FCSTD DOCUMENT  (FreeCAD 0.21R33668 +7 (Git))
Label: salorNodes_Oct23_2023
License: All rights reserved
LicenseURL: http://en.wikipedia.org/wiki/All_rights_reserved
objects: Part::Feature×157, Part::Cylinder×106, Part::MultiFuse×81, Sketcher::SketchObject×71, Part::Fillet×46, Part::Cut×34, Part::Extrusion×24, Part::Loft×22, App::Part×19, Part::Box×10, Part::FeaturePython×10, Part::Sphere×5, Part::Compound×2, Mesh::Feature×2, Part::Cone×2, PartDesign::Pad×2, PartDesign::Body×2, PartDesign::AdditiveBox×1, Part::Mirroring×1
note: 579 computed .brp shape members not serialized (recipe doc carries the construction recipe); baked Part::Feature solids carry a one-line shape summary decoded from their .brp

FEATURE [Part::Feature] Part__Feature  label="PH Pan head screw M2x0.40 x 6"
  Placement = pos=(101.945,-83.8381,-1.82512) rot=(0,0,1;3.14159rad)
  shape: bbox 4.006 x 4.006 x 7.57 mm, 32 faces (baked)
FEATURE [Part::Feature] Part__Feature001  label="Part 8"
  Placement = pos=(178.445,24.1619,-39.4251) rot=(0,1,0;3.14159rad)
  shape: bbox 166 x 27.4 x 2 mm, 14 faces (baked)
FEATURE [Part::Feature] Part__Feature002  label="event gore PMF100320"
  Placement = pos=(79.1369,-76.58,11.5741) rot=(0,-1,0;0.037482rad)
  shape: bbox 2.468 x 15.31 x 15.29 mm, 4 faces (baked)
FEATURE [Part::Feature] Part__Feature003  label="event gore PMF100321"
  Placement = pos=(79.1369,-76.58,11.5741) rot=(0,-1,0;0.037482rad)
  shape: bbox 15.95 x 18.27 x 18.26 mm, 114 faces (baked)
FEATURE [Part::Feature] Part__Feature004  label="PH Pan head screw M2x0.40 x 007"
  Placement = pos=(101.945,24.1619,-1.82512) rot=(0,0,1;0rad)
  shape: bbox 4.006 x 4.006 x 7.57 mm, 32 faces (baked)
FEATURE [Part::Feature] Part__Feature005  label="WPB20-28-7_3D"
  Placement = pos=(178.445,24.1619,30.5749) rot=(0,0,1;0rad)
  shape: bbox 200.6 x 280.6 x 46.01 mm, 1035 faces (baked)
FEATURE [Part::Feature] Part__Feature006  label="PH Pan head screw M2x0.40 x 008"
  Placement = pos=(254.945,-83.8381,-1.82512) rot=(0,0,1;3.14159rad)
  shape: bbox 4.006 x 4.006 x 7.57 mm, 32 faces (baked)
FEATURE [Part::Feature] Part__Feature007  label="Cable Gland PG7-PG19 Lock Nut_PG13.5"
  Placement = pos=(223.445,-112.627,11.6686) rot=(1,0,0;0.037482rad)
  shape: bbox 29.02 x 6.449 x 29 mm, 29 faces (baked)
FEATURE [Part::Feature] Part__Feature008  label="Cable Gland PG7-PG19 Body_PG13.5"
  Placement = pos=(223.445,-118.923,11.4325) rot=(0,-0.01874,0.999824;3.14159rad)
  shape: bbox 25.06 x 36.36 x 23.18 mm, 156 faces (baked)
FEATURE [Part::Feature] Part__Feature009  label="Cable Gland PG7-PG19 Washer_PG13.5"
  Placement = pos=(223.445,-115.725,11.5524) rot=(0,-0.01874,0.999824;3.14159rad)
  shape: bbox 25 x 2.136 x 25.03 mm, 4 faces (baked)
FEATURE [Part::Feature] Part__Feature010  label="Cable Gland PG7-PG19 Gland Nut_PG13.5"
  Placement = pos=(223.445,-132.014,10.9416) rot=(0.825324,-0.010582,0.56456;3.17253rad)
  shape: bbox 25.82 x 20.19 x 25.8 mm, 50 faces (baked)
FEATURE [Part::Feature] Part__Feature011  label="Cable Gland PG7-PG19 Sleeve_PG13.5"
  Placement = pos=(223.445,-137.51,10.7355) rot=(0,-0.01874,0.999824;3.14159rad)
  shape: bbox 15.7 x 8.583 x 15.99 mm, 4 faces (baked)
FEATURE [App::Part] Cable_Gland_PG7_PG19__PG13_5__1_  label="Cable Gland PG7-PG19, PG13.5 <1>"
  Group = -> [Part__Feature007,Part__Feature008,Part__Feature009,Part__Feature010,Part__Feature011]
  Origin = -> Origin
FEATURE [Part::Feature] Part__Feature012  label="WPMB-M4-2"
  Placement = pos=(178.445,24.1619,-13.4251) rot=(0,1,0;3.14159rad)
  shape: bbox 91.99 x 91.99 x 12.05 mm, 899 faces (baked)
FEATURE [Part::Feature] Part__Feature013  label="Micro_USB_Plug v10"
  Placement = pos=(255.557,33.7719,7.31475) rot=(0.577351,0.577352,-0.577348;4.18879rad)
  shape: bbox 4.78 x 0.2 x 0.4672 mm, 14 faces (baked)
FEATURE [Part::Feature] Part__Feature014  label="Micro_USB_Plug_Connector"
  Placement = pos=(255.557,33.7719,7.31475) rot=(0.577351,0.577352,-0.577348;4.18879rad)
  shape: bbox 7.5 x 6.85 x 1.85 mm, 68 faces (baked)
FEATURE [Part::Feature] Part__Feature015  label="Micro_USB_Plug v011"
  Placement = pos=(255.557,33.7719,7.31475) rot=(0.577351,0.577352,-0.577348;4.18879rad)
  shape: bbox 4.78 x 0.2 x 0.4672 mm, 14 faces (baked)
FEATURE [Part::Feature] Part__Feature016  label="Micro_USB_Plug_Connector001"
  Placement = pos=(255.557,33.7719,7.31475) rot=(0.577351,0.577352,-0.577348;4.18879rad)
  shape: bbox 4.574 x 0.32 x 1.625 mm, 11 faces (baked)
FEATURE [Part::Feature] Part__Feature017  label="micro_usb_plug rt angle"
  Placement = pos=(255.557,33.7719,7.31475) rot=(0.577351,0.577352,-0.577348;4.18879rad)
  shape: bbox 12.25 x 19.75 x 7.006 mm, 151 faces (baked)
FEATURE [Part::Feature] Part__Feature018  label="Micro_USB_Plug v012"
  Placement = pos=(255.557,33.7719,7.31475) rot=(0.577351,0.577352,-0.577348;4.18879rad)
  shape: bbox 4.78 x 0.2 x 0.4672 mm, 14 faces (baked)
FEATURE [Part::Feature] Part__Feature019  label="Micro_USB_Plug v013"
  Placement = pos=(255.557,33.7719,7.31475) rot=(0.577351,0.577352,-0.577348;4.18879rad)
  shape: bbox 4.78 x 0.2 x 0.4672 mm, 14 faces (baked)
FEATURE [Part::Feature] Part__Feature020  label="Wire"
  Placement = pos=(255.557,33.7719,7.31475) rot=(0.577351,0.577352,-0.577348;4.18879rad)
  shape: bbox 3.2 x 9.5 x 3.2 mm, 3 faces (baked)
FEATURE [Part::Feature] Part__Feature021  label="Micro_USB_Plug_Connector002"
  Placement = pos=(255.557,33.7719,7.31475) rot=(0.577351,0.577352,-0.577348;4.18879rad)
  shape: bbox 4.7 x 0.32 x 1.625 mm, 11 faces (baked)
FEATURE [Part::Feature] Part__Feature022  label="Micro_USB_Plug v014"
  Placement = pos=(255.557,33.7719,7.31475) rot=(0.577351,0.577352,-0.577348;4.18879rad)
  shape: bbox 4.78 x 0.2 x 0.4672 mm, 14 faces (baked)
FEATURE [Part::Feature] Part__Feature023  label="Micro_USB_Plug_Connector003"
  Placement = pos=(255.557,33.7719,7.31475) rot=(0.577351,0.577352,-0.577348;4.18879rad)
  shape: bbox 7.5 x 6.35 x 1.35 mm, 54 faces (baked)
FEATURE [Part::Feature] Part__Feature024  label="2_C_3_4_6_1_1"
  Placement = pos=(205.099,-19.2281,8.57488) rot=(-1,-3e-06,-3e-06;1.57079rad)
  shape: bbox 73.52 x 148.2 x 33.63 mm, 876 faces (baked)
FEATURE [Part::Feature] Part__Feature025  label="2_BAT_3_4_6_1_1"
  Placement = pos=(205.099,-19.2281,8.57488) rot=(-1,-3e-06,-3e-06;1.57079rad)
  shape: bbox 14.36 x 15.32 x 64.97 mm, 83 faces (baked)
FEATURE [Part::Feature] Part__Feature026  label="2_B_3_4_6_1_1"
  Placement = pos=(205.099,-19.2281,8.57488) rot=(-1,-3e-06,-3e-06;1.57079rad)
  shape: bbox 78.1 x 152 x 64.86 mm, 1086 faces (baked)
FEATURE [Part::Feature] Part__Feature027  label="2_A_3_4_6_2_1"
  Placement = pos=(205.099,-19.2281,8.57488) rot=(-1,-3e-06,-3e-06;1.57079rad)
  shape: bbox 73.51 x 148.2 x 58.23 mm, 268 faces (baked)
FEATURE [App::Part] V75_ASM__1_  label="V75 ASM <1>"
  Group = -> [Part__Feature013,Part__Feature014,Part__Feature015,Part__Feature016,Part__Feature017,Part__Feature018,Part__Feature019,Part__Feature020,Part__Feature021,Part__Feature022,Part__Feature023,Part__Feature024,Part__Feature025,Part__Feature026,Part__Feature027]
  Origin = -> Origin001
  Placement = pos=(6,15.97,20) rot=(0,0,1;0rad)
FEATURE [Part::Feature] Part__Feature028  label="PH Pan head screw M2x0.40 x 009"
  Placement = pos=(254.945,24.1619,-1.82512) rot=(0,0,1;0rad)
  shape: bbox 4.006 x 4.006 x 7.57 mm, 32 faces (baked)
FEATURE [Part::Feature] Part__Feature029  label="Part 009"
  Placement = pos=(178.445,-83.8381,-39.4251) rot=(1,0,0;3.14159rad)
  shape: bbox 166 x 27.4 x 2 mm, 14 faces (baked)
FEATURE [Part::Feature] Part__Feature030  label="WPC20-28_3D"
  Placement = pos=(178.435,24.1794,31.5749) rot=(0,0,1;0rad)
  shape: bbox 201.1 x 281.1 x 21.57 mm, 1217 faces (baked)
FEATURE [Part::Feature] Part__Feature031  label="Cable Gland PG7-PG19 Sleeve_PG9"
  Placement = pos=(133.445,-133.413,10.8891) rot=(0,-0.01874,0.999824;3.14159rad)
  shape: bbox 11 x 8.207 x 11.28 mm, 4 faces (baked)
FEATURE [Part::Feature] Part__Feature032  label="Cable Gland PG7-PG19 Washer_PG9"
  Placement = pos=(133.445,-115.725,11.5524) rot=(0,-0.01874,0.999824;3.14159rad)
  shape: bbox 19.7 x 1.937 x 19.73 mm, 4 faces (baked)
FEATURE [Part::Feature] Part__Feature033  label="Cable Gland PG7-PG19 Lock Nut_PG9"
  Placement = pos=(133.445,-112.627,11.6686) rot=(1,0,0;0.037482rad)
  shape: bbox 24.34 x 6.322 x 24.32 mm, 29 faces (baked)
FEATURE [Part::Feature] Part__Feature034  label="Cable Gland PG7-PG19 Body_PG9"
  Placement = pos=(133.445,-118.823,11.4362) rot=(0,-0.01874,0.999824;3.14159rad)
  shape: bbox 19.4 x 32.49 x 17.68 mm, 129 faces (baked)
FEATURE [Part::Feature] Part__Feature035  label="Cable Gland PG7-PG19 Gland Nut_PG9"
  Placement = pos=(133.445,-130.065,11.0147) rot=(0.825324,-0.010582,0.56456;3.17253rad)
  shape: bbox 20.81 x 16.04 x 20.8 mm, 48 faces (baked)
FEATURE [App::Part] Cable_Gland_PG7_PG19__PG9__1_  label="Cable Gland PG7-PG19, PG9 <1>"
  Group = -> [Part__Feature031,Part__Feature032,Part__Feature033,Part__Feature034,Part__Feature035]
  Origin = -> Origin002
FEATURE [App::Part] E305__20x28x7cm_  label="box"
  Group = -> [Part__Feature,Part__Feature001,Part__Feature002,Part__Feature003,Part__Feature004,Part__Feature005,Part__Feature006,Cable_Gland_PG7_PG19__PG13_5__1_,Part__Feature012,V75_ASM__1_,Part__Feature028,Part__Feature029,Part__Feature030,Cable_Gland_PG7_PG19__PG9__1_]
  Origin = -> Origin003
  Placement = pos=(175.533,-124.11,-130.152) rot=(0,-0.939693,-0.34202;3.14159rad)
FEATURE [Part::Feature] Part__Feature036  label="id2"
  shape: bbox 274 x 229.5 x 2.5 mm, 53 faces (baked)
FEATURE [Part::Feature] Part__Feature037  label="id5"
  shape: bbox 251.2 x 70.58 x 83.44 mm, 48 faces (baked)
FEATURE [Part::Feature] Part__Feature038  label="id8"
  shape: bbox 253.5 x 2.737 x 2.883 mm, 6 faces (baked)
FEATURE [Part::MultiFuse] Fusion  label="solarPanelMount"
  Placement = pos=(0,0,0) rot=(1,0,0;0.698132rad)
  Shapes = -> [Part__Feature036,Part__Feature037,Part__Feature038]
FEATURE [Part::Feature] Part__Feature039  label="Part 2"
  Placement = pos=(-0.595807,44.562,74.9733) rot=(1,0,0;3.14159rad)
  shape: bbox 272 x 434 x 1.1 mm, 24 faces (baked)
FEATURE [Part::Feature] Part__Feature041  label="id16"
  Placement = pos=(-0.595807,44.562,69.8733) rot=(0,0,1;0rad)
  shape: bbox 4 x 8.79 x 2 mm, 10 faces (baked)
FEATURE [Part::Feature] Part__Feature042  label="id21"
  Placement = pos=(-0.595807,44.562,69.8733) rot=(0,0,1;0rad)
  shape: bbox 125 x 42.28 x 0.1 mm, 8 faces (baked)
FEATURE [Part::Feature] Part__Feature043  label="id26"
  Placement = pos=(-0.595807,44.562,69.8733) rot=(0,0,1;0rad)
  shape: bbox 125 x 42.28 x 0.1 mm, 8 faces (baked)
FEATURE [Part::Feature] Part__Feature044  label="id31"
  Placement = pos=(-0.595807,44.562,69.8733) rot=(0,0,1;0rad)
  shape: bbox 4 x 8.79 x 2 mm, 10 faces (baked)
FEATURE [Part::Feature] Part__Feature045  label="id36"
  Placement = pos=(-0.595807,44.562,69.8733) rot=(0,0,1;0rad)
  shape: bbox 125 x 42.28 x 0.1 mm, 8 faces (baked)
FEATURE [Part::Feature] Part__Feature046  label="id41"
  Placement = pos=(-0.595807,44.562,69.8733) rot=(0,0,1;0rad)
  shape: bbox 4 x 4 x 2 mm, 4 faces (baked)
FEATURE [Part::Feature] Part__Feature047  label="id46"
  Placement = pos=(-0.595807,44.562,69.8733) rot=(0,0,1;0rad)
  shape: bbox 4 x 4 x 2 mm, 4 faces (baked)
FEATURE [Part::Feature] Part__Feature048  label="id51"
  Placement = pos=(-0.595807,44.562,69.8733) rot=(0,0,1;0rad)
  shape: bbox 125 x 42.28 x 0.1 mm, 8 faces (baked)
FEATURE [Part::Feature] Part__Feature049  label="id56"
  Placement = pos=(-0.595807,44.562,69.8733) rot=(0,0,1;0rad)
  shape: bbox 125 x 42.28 x 0.1 mm, 8 faces (baked)
FEATURE [Part::Feature] Part__Feature050  label="id61"
  Placement = pos=(-0.595807,44.562,69.8733) rot=(0,0,1;0rad)
  shape: bbox 4 x 4 x 2 mm, 4 faces (baked)
FEATURE [Part::Feature] Part__Feature051  label="id66"
  Placement = pos=(-0.595807,44.562,69.8733) rot=(0,0,1;0rad)
  shape: bbox 125 x 42.28 x 0.1 mm, 8 faces (baked)
FEATURE [Part::Feature] Part__Feature052  label="id71"
  Placement = pos=(-0.595807,44.562,69.8733) rot=(0,0,1;0rad)
  shape: bbox 125 x 40.44 x 0.1 mm, 6 faces (baked)
FEATURE [Part::Feature] Part__Feature053  label="id76"
  Placement = pos=(-0.595807,44.562,69.8733) rot=(0,0,1;0rad)
  shape: bbox 125 x 40.44 x 0.1 mm, 6 faces (baked)
FEATURE [Part::Feature] Part__Feature054  label="id81"
  Placement = pos=(-0.595807,44.562,69.8733) rot=(0,0,1;0rad)
  shape: bbox 125 x 42.28 x 0.1 mm, 8 faces (baked)
FEATURE [Part::Feature] Part__Feature055  label="id86"
  Placement = pos=(-0.595807,44.562,69.8733) rot=(0,0,1;0rad)
  shape: bbox 125 x 42.28 x 0.1 mm, 8 faces (baked)
FEATURE [Part::Feature] Part__Feature056  label="id91"
  Placement = pos=(-0.595807,44.562,69.8733) rot=(0,0,1;0rad)
  shape: bbox 125 x 42.28 x 0.1 mm, 8 faces (baked)
FEATURE [Part::Feature] Part__Feature057  label="id96"
  Placement = pos=(-0.595807,44.562,69.8733) rot=(0,0,1;0rad)
  shape: bbox 272 x 434 x 2 mm, 24 faces (baked)
FEATURE [Part::Feature] Part__Feature058  label="id101"
  Placement = pos=(-0.595807,44.562,69.8733) rot=(0,0,1;0rad)
  shape: bbox 125 x 42.28 x 0.1 mm, 8 faces (baked)
FEATURE [Part::Feature] Part__Feature059  label="id106"
  Placement = pos=(-0.595807,44.562,69.8733) rot=(0,0,1;0rad)
  shape: bbox 125 x 42.28 x 0.1 mm, 8 faces (baked)
FEATURE [Part::Feature] Part__Feature060  label="id111"
  Placement = pos=(-0.595807,44.562,69.8733) rot=(0,0,1;0rad)
  shape: bbox 125 x 42.28 x 0.1 mm, 8 faces (baked)
FEATURE [Part::Feature] Part__Feature061  label="id116"
  Placement = pos=(-0.595807,44.562,69.8733) rot=(0,0,1;0rad)
  shape: bbox 4 x 4 x 2 mm, 4 faces (baked)
FEATURE [Part::Feature] Part__Feature062  label="id121"
  Placement = pos=(-0.595807,44.562,69.8733) rot=(0,0,1;0rad)
  shape: bbox 4 x 4 x 2 mm, 4 faces (baked)
FEATURE [Part::Feature] Part__Feature063  label="id126"
  Placement = pos=(-0.595807,44.562,69.8733) rot=(0,0,1;0rad)
  shape: bbox 125 x 42.28 x 0.1 mm, 8 faces (baked)
FEATURE [Part::Feature] Part__Feature064  label="id131"
  Placement = pos=(-0.595807,44.562,69.8733) rot=(0,0,1;0rad)
  shape: bbox 4 x 4 x 2 mm, 4 faces (baked)
FEATURE [Part::Feature] Part__Feature065  label="id136"
  Placement = pos=(-0.595807,44.562,69.8733) rot=(0,0,1;0rad)
  shape: bbox 125 x 40.44 x 0.1 mm, 6 faces (baked)
FEATURE [Part::Feature] Part__Feature066  label="id141"
  Placement = pos=(-0.595807,44.562,69.8733) rot=(0,0,1;0rad)
  shape: bbox 274 x 436 x 2 mm, 18 faces (baked)
FEATURE [Part::Feature] Part__Feature067  label="id146"
  Placement = pos=(-0.595807,44.562,69.8733) rot=(0,0,1;0rad)
  shape: bbox 125 x 42.28 x 0.1 mm, 8 faces (baked)
FEATURE [Part::Feature] Part__Feature068  label="id151"
  Placement = pos=(-0.595807,44.562,69.8733) rot=(0,0,1;0rad)
  shape: bbox 125 x 42.28 x 0.1 mm, 8 faces (baked)
FEATURE [Part::Feature] Part__Feature069  label="id156"
  Placement = pos=(-0.595807,44.562,69.8733) rot=(0,0,1;0rad)
  shape: bbox 125 x 42.28 x 0.1 mm, 8 faces (baked)
FEATURE [Part::Feature] Part__Feature070  label="id161"
  Placement = pos=(-0.595807,44.562,69.8733) rot=(0,0,1;0rad)
  shape: bbox 125 x 40.44 x 0.1 mm, 6 faces (baked)
FEATURE [Part::Feature] Part__Feature076  label="Part 1"
  Placement = pos=(-0.595807,44.562,74.9733) rot=(1,0,0;3.14159rad)
  shape: bbox 274 x 436 x 1.1 mm, 18 faces (baked)
FEATURE [Part::Feature] Part__Feature077  label="JBox - 30 mm"
  Placement = pos=(-50.5959,-43.7114,69.8733) rot=(0,1,0;3.14159rad)
  shape: bbox 30.01 x 30.09 x 5.866 mm, 175 faces (baked)
FEATURE [App::Part] P120  label="solarPanel"
  Group = -> [Part__Feature039,Part__Feature041,Part__Feature042,Part__Feature043,Part__Feature044,Part__Feature045,Part__Feature046,Part__Feature047,Part__Feature048,Part__Feature049,Part__Feature050,Part__Feature051,Part__Feature052,Part__Feature053,Part__Feature054,Part__Feature055,Part__Feature056,Part__Feature057,Part__Feature058,Part__Feature059,Part__Feature060,Part__Feature061,Part__Feature062,+10 more]
  Origin = -> Origin004
  Placement = pos=(0.5,-120,-180) rot=(1,0,0;0.698132rad)
FEATURE [Part::Feature] Part__Feature078  label="Open CASCADE STEP translator 7.4 2.1.1"
  shape: bbox 8.3 x 1.9 x 1 mm, 10 faces, 0 solids (baked)
FEATURE [Part::Feature] Part__Feature079  label="Open CASCADE STEP translator 7.4 2.1.2"
  shape: bbox 12.5 x 10 x 1.5 mm, 6 faces, 0 solids (baked)
FEATURE [Part::Feature] Part__Feature080  label="Open CASCADE STEP translator 7.4 2.1.3"
  shape: bbox 12.5 x 10 x 1.5 mm, 6 faces, 0 solids (baked)
FEATURE [Part::Feature] Part__Feature081  label="Open CASCADE STEP translator 7.4 2.1.4"
  shape: bbox 12.5 x 10 x 1.5 mm, 6 faces, 0 solids (baked)
FEATURE [Part::Feature] Part__Feature082  label="Open CASCADE STEP translator 7.4 2.1.5"
  shape: bbox 12.5 x 10 x 1.5 mm, 6 faces, 0 solids (baked)
FEATURE [Part::Feature] Part__Feature083  label="Open CASCADE STEP translator 7.4 2.1.6"
  shape: bbox 89.5 x 57.1 x 20.65 mm, 2741 faces, 0 solids (baked)
FEATURE [App::Part] Open_CASCADE_STEP_translator_7_4_2_1  label="Open CASCADE STEP translator 7.4 2.1"
  Group = -> [Part__Feature078,Part__Feature079,Part__Feature080,Part__Feature081,Part__Feature082,Part__Feature083]
  Origin = -> Origin005
FEATURE [Part::Feature] Part__Feature084  label="m312mm"
  Placement = pos=(63.5,-7,61.5) rot=(0,0.707107,0.707107;3.14159rad)
  shape: bbox 6.201 x 15.54 x 6.201 mm, 70 faces (baked)
FEATURE [Part::Feature] Part__Feature085  label="m312mm001"
  Placement = pos=(14.5,-7,61.5) rot=(-1,0,0;1.5708rad)
  shape: bbox 6.201 x 15.54 x 6.201 mm, 70 faces (baked)
FEATURE [Part::MultiFuse] Fusion003
  Shapes = -> [Part__Feature085,Part__Feature084]
FEATURE [Part::Feature] Part__Feature086  label="m312mm002"
  Placement = pos=(14.5,-7,61.5) rot=(-1,0,0;1.5708rad)
  shape: bbox 6.201 x 15.54 x 6.201 mm, 70 faces (baked)
FEATURE [Part::Feature] Part__Feature087  label="m312mm003"
  Placement = pos=(63.5,-7,61.5) rot=(0,0.707107,0.707107;3.14159rad)
  shape: bbox 6.201 x 15.54 x 6.201 mm, 70 faces (baked)
FEATURE [Part::MultiFuse] Fusion004
  Placement = pos=(0,0,-58) rot=(0,0,1;0rad)
  Shapes = -> [Part__Feature086,Part__Feature087]
FEATURE [Part::MultiFuse] Fusion005  label="m3s"
  Placement = pos=(0.1,-1,0) rot=(0,0,1;0rad)
  Shapes = -> [Fusion004,Fusion003]
FEATURE [App::Part] Open_CASCADE_STEP_translator_7_4_2  label="C4"
  Group = -> [Open_CASCADE_STEP_translator_7_4_2_1,Part__Feature084,Part__Feature085,Fusion003,Part__Feature086,Part__Feature087,Fusion004,Fusion005]
  Origin = -> Origin006
  Placement = pos=(-15,-5,-224) rot=(0.57735,-0.57735,0.57735;2.0944rad)
FEATURE [Part::Feature] Part__Feature088  label="MainBoard"
  shape: bbox 50 x 23 x 1.8 mm, 90 faces (baked)
FEATURE [Part::Feature] Part__Feature089  label="USB Type C Port (SMD Type)"
  Placement = pos=(-18.7,0.12,3.4) rot=(0.707107,-0.707107,0;3.14159rad)
  shape: bbox 7.901 x 8.941 x 4.201 mm, 394 faces, 24 solids (baked)
FEATURE [Part::Feature] Part__Feature090  label="LoRaSTM32Chip"
  Placement = pos=(8.97,0,1.8) rot=(0,0,1;0rad)
  shape: bbox 12 x 12 x 2.5 mm, 68 faces (baked)
FEATURE [Part::Feature] Part__Feature091  label="E10_433M_SMA122"
  Placement = pos=(13,-2.15,1.4) rot=(0,0,1;0rad)
  shape: bbox 11.33 x 1.55 x 1.55 mm, 34 faces (baked)
FEATURE [Part::Feature] Part__Feature092  label="E10_433M_SMA123"
  Placement = pos=(13,-2.15,1.4) rot=(0,0,1;0rad)
  shape: bbox 13.33 x 6.493 x 6.493 mm, 59 faces (baked)
FEATURE [Part::Feature] Part__Feature093  label="CP2012"
  Placement = pos=(-8.75,0.13,1.82) rot=(0,0,1;0rad)
  shape: bbox 4 x 4 x 0.7 mm, 6 faces (baked)
FEATURE [Part::Feature] Part__Feature094  label="u.Fl Antenna Connector - 523-A-1JB"
  Placement = pos=(24.2,5.8,1.8) rot=(0,0.707107,0.707107;3.14159rad)
  shape: bbox 3.1 x 3 x 1.25 mm, 82 faces, 5 solids (baked)
FEATURE [Part::Feature] Part__Feature095  label="Top Traces"
  shape: bbox 49.4 x 23 x 0.02 mm, 7906 faces, 207 solids (baked)
FEATURE [App::Part] LoRa_E5_Mini  label="LoRa-E5-Mini"
  Group = -> [Part__Feature088,Part__Feature089,Part__Feature090,Part__Feature091,Part__Feature092,Part__Feature093,Part__Feature094,Part__Feature095]
  Origin = -> Origin007
  Placement = pos=(-44,0,-220) rot=(0.57735,0.57735,-0.57735;2.0944rad)
FEATURE [Part::Feature] Part__Feature096  label="nanoSupport001"
  Placement = pos=(-30,0,-97) rot=(0.57735,-0.57735,0.57735;2.0944rad)
  shape: bbox 56 x 30 x 43 mm, 8 faces (baked)
FEATURE [Sketcher::SketchObject] Sketch
  FullyConstrained = true
  MapMode = 3
  Placement = pos=(178.445,24.1619,-13.4251) rot=(0,0.707107,-0.707107;3.14159rad)
  Support = -> [Part__Feature012]
  sketch-geometry (32):
    g0: LineSegment StartX=99 StartY=265 StartZ=0 EndX=261 EndY=265 EndZ=0
    g1: LineSegment StartX=261 StartY=265 StartZ=0 EndX=261 EndY=40 EndZ=0
    g2: LineSegment StartX=261 StartY=40 StartZ=0 EndX=99 EndY=40 EndZ=0
    g3: LineSegment StartX=99 StartY=40 StartZ=0 EndX=99 EndY=265 EndZ=0
    g4: Circle CenterX=103.5 CenterY=260.4 CenterZ=0 NormalX=0 NormalY=0 NormalZ=1 AngleXU=0 Radius=1.25
    g5: Circle CenterX=256.5 CenterY=260.4 CenterZ=0 NormalX=0 NormalY=0 NormalZ=1 AngleXU=0 Radius=1.25
    g6: Circle CenterX=103.5 CenterY=152.4 CenterZ=0 NormalX=0 NormalY=0 NormalZ=1 AngleXU=0 Radius=1.25
    g7: Circle CenterX=103.5 CenterY=44.4 CenterZ=0 NormalX=0 NormalY=0 NormalZ=1 AngleXU=0 Radius=1.25
    g8: Circle CenterX=256.5 CenterY=44.4 CenterZ=0 NormalX=0 NormalY=0 NormalZ=1 AngleXU=0 Radius=1.25
    g9: Circle CenterX=256.5 CenterY=152.4 CenterZ=0 NormalX=0 NormalY=0 NormalZ=1 AngleXU=0 Radius=1.25
    g10: Circle CenterX=213.46 CenterY=229.1 CenterZ=0 NormalX=0 NormalY=0 NormalZ=1 AngleXU=0 Radius=1.25
    g11: Circle CenterX=231.46 CenterY=229.1 CenterZ=0 NormalX=0 NormalY=0 NormalZ=1 AngleXU=0 Radius=1.25
    g12: Circle CenterX=213.46 CenterY=194.1 CenterZ=0 NormalX=0 NormalY=0 NormalZ=1 AngleXU=0 Radius=1.25
    g13: Circle CenterX=231.46 CenterY=194.1 CenterZ=0 NormalX=0 NormalY=0 NormalZ=1 AngleXU=0 Radius=1.25
    g14: Circle CenterX=245.95 CenterY=207.08 CenterZ=0 NormalX=0 NormalY=0 NormalZ=1 AngleXU=0 Radius=1.625
    g15: Circle CenterX=196.95 CenterY=207.08 CenterZ=0 NormalX=0 NormalY=0 NormalZ=1 AngleXU=0 Radius=1.625
    g16: Circle CenterX=245.95 CenterY=149.08 CenterZ=0 NormalX=0 NormalY=0 NormalZ=1 AngleXU=0 Radius=1.625
    g17: Circle CenterX=196.95 CenterY=149.08 CenterZ=0 NormalX=0 NormalY=0 NormalZ=1 AngleXU=0 Radius=1.625
    g18: Circle CenterX=208.2 CenterY=101.58 CenterZ=0 NormalX=0 NormalY=0 NormalZ=1 AngleXU=0 Radius=1.25
    g19: Circle CenterX=208.2 CenterY=94.58 CenterZ=0 NormalX=0 NormalY=0 NormalZ=1 AngleXU=0 Radius=1.25
    g20: Circle CenterX=238.2 CenterY=101.58 CenterZ=0 NormalX=0 NormalY=0 NormalZ=1 AngleXU=0 Radius=1.25
    g21: Circle CenterX=246.2 CenterY=62.1 CenterZ=0 NormalX=0 NormalY=0 NormalZ=1 AngleXU=0 Radius=1.625
    g22: Circle CenterX=200.7 CenterY=62.1 CenterZ=0 NormalX=0 NormalY=0 NormalZ=1 AngleXU=0 Radius=1.625
    g23: Circle CenterX=238.2 CenterY=94.58 CenterZ=0 NormalX=0 NormalY=0 NormalZ=1 AngleXU=0 Radius=1.25
    g24: Circle CenterX=138 CenterY=105 CenterZ=0 NormalX=0 NormalY=0 NormalZ=1 AngleXU=0 Radius=5
    g25: Circle CenterX=156.7 CenterY=105 CenterZ=0 NormalX=0 NormalY=0 NormalZ=1 AngleXU=0 Radius=5
    g26: Circle CenterX=138 CenterY=255 CenterZ=0 NormalX=0 NormalY=0 NormalZ=1 AngleXU=0 Radius=5
    g27: Circle CenterX=156.7 CenterY=255 CenterZ=0 NormalX=0 NormalY=0 NormalZ=1 AngleXU=0 Radius=5
    g28: Circle CenterX=110 CenterY=220 CenterZ=0 NormalX=0 NormalY=0 NormalZ=1 AngleXU=0 Radius=5
    g29: Circle CenterX=184.8 CenterY=220 CenterZ=0 NormalX=0 NormalY=0 NormalZ=1 AngleXU=0 Radius=5
    g30: Circle CenterX=110 CenterY=170 CenterZ=0 NormalX=0 NormalY=0 NormalZ=1 AngleXU=0 Radius=5
    g31: Circle CenterX=184.8 CenterY=170 CenterZ=0 NormalX=0 NormalY=0 NormalZ=1 AngleXU=0 Radius=5
  constraints (86):
    c: Coincident(g0,g1)
    c: Coincident(g1,g2)
    c: Coincident(g2,g3)
    c: Coincident(g3,g0)
    c: Horizontal(g0)
    c: Horizontal(g2)
    c: Vertical(g1)
    c: Vertical(g3)
    c: DistanceX(g2) = 99
    c: DistanceX(g1) = 261
    c: DistanceY(g2) = 40
    c: DistanceY(g0) = 265
    c: Equal(g18,g19)
    c: Equal(g18,g20)
    c: Equal(g18,g23)
    c: Equal(g18,g9)
    c: Equal(g18, g4-g8) x5
    c: Equal(g18, g10-g13) x4
    c: Radius(g18) = 1.25
    c: DistanceX(g7) = 103.5
    c: DistanceY(g7) = 44.4
    c: DistanceX(g7,g6) = 0
    c: DistanceX(g4,g6) = 0
    c: DistanceX(g7,g8) = 153
    c: DistanceY(g7,g8) = 0
    c: DistanceY(g6,g9) = 0
    c: DistanceY(g5,g4) = 0
    c: DistanceX(g8,g9) = 0
    c: DistanceX(g9,g5) = 0
    c: DistanceX(g17) = 196.95
    c: DistanceY(g17) = 149.08
    c: Equal(g14,g16)
    c: Equal(g14,g17)
    c: Equal(g14,g15)
    c: Diameter(g14) = 3.25
    c: DistanceX(g17,g16) = 49
    c: DistanceY(g17,g16) = 0
    c: DistanceY(g17,g15) = 58
    c: DistanceX(g17,g15) = 0
    c: DistanceY(g14,g15) = 0
    c: DistanceX(g14,g16) = 0
    c: DistanceX(g12) = 213.46
    c: DistanceY(g12) = 194.1
    c: DistanceY(g13,g12) = 0
    c: DistanceX(g12,g13) = 18
    c: DistanceX(g10,g12) = 0
    c: DistanceX(g11,g13) = 0
    c: DistanceY(g12,g10) = 35
    c: DistanceY(g11,g10) = 0
    c: Equal(g24,g25)
    c: Equal(g24,g30)
    c: Equal(g24,g31)
    c: Equal(g24, g26-g29) x4
    c: Diameter(g24) = 10
    c: DistanceY(g24) = 105
    c: DistanceY(g25,g24) = 0
    c: DistanceX(g24) = 138
    c: DistanceX(g24,g25) = 18.7
    c: DistanceY(g24,g26) = 150
    c: DistanceX(g26,g24) = 0
    c: DistanceX(g27,g25) = 0
    c: DistanceY(g26,g27) = 0
    c: DistanceX(g30) = 110
    c: DistanceY(g30) = 170
    c: DistanceY(g30,g31) = 0
    c: DistanceX(g30,g31) = 74.8
    c: DistanceY(g30,g28) = 50
    c: DistanceY(g28,g29) = 0
    c: DistanceX(g28,g30) = 0
    c: DistanceX(g31,g29) = 0
    c: DistanceY(g7,g4) = 216
    c: DistanceX(g7,g22) = 97.2
    c: DistanceY(g22,g21) = 0
    c: DistanceX(g22,g21) = 45.5
    c: DistanceY(g22) = 62.1
    c: DistanceX(g7,g19) = 104.7
    c: DistanceY(g19) = 94.58
    c: DistanceX(g18,g19) = 0
    c: DistanceY(g19,g18) = 7
    c: DistanceX(g19,g23) = 30
    c: DistanceY(g23,g19) = 0
    c: DistanceX(g23,g20) = 0
    c: DistanceY(g18,g20) = 0
    c: Equal(g22,g21)
    c: Diameter(g22) = 3.25
    c: DistanceY(g7,g6) = 108
FEATURE [Part::Box] Box007  label="Cube007"
  AttacherType = Attacher::AttachEngine3D
  Height = 17
  Length = 36.5
  Width = 3
FEATURE [Part::Cylinder] Cylinder012  label="m2s"
  Angle = 360
  AttacherType = Attacher::AttachEngine3D
  FirstAngle = 0
  Height = 10
  Placement = pos=(0,0,0) rot=(1,0,0;1.5708rad)
  Radius = 1.2
  SecondAngle = 0
FEATURE [Part::Cylinder] Cylinder014  label="m2s001"
  Angle = 360
  AttacherType = Attacher::AttachEngine3D
  FirstAngle = 0
  Height = 10
  Placement = pos=(30,0,0) rot=(1,0,0;1.5708rad)
  Radius = 1.2
  SecondAngle = 0
FEATURE [Part::Cylinder] Cylinder015  label="m2s002"
  Angle = 360
  AttacherType = Attacher::AttachEngine3D
  FirstAngle = 0
  Height = 10
  Placement = pos=(0,0,0) rot=(1,0,0;1.5708rad)
  Radius = 1.2
  SecondAngle = 0
FEATURE [Part::Cylinder] Cylinder016  label="m2s003"
  Angle = 360
  AttacherType = Attacher::AttachEngine3D
  FirstAngle = 0
  Height = 10
  Placement = pos=(30,0,0) rot=(1,0,0;1.5708rad)
  Radius = 1.2
  SecondAngle = 0
FEATURE [Part::MultiFuse] Fusion017
  Placement = pos=(3.25,0,0) rot=(0,0,1;0rad)
  Shapes = -> [Cylinder014,Cylinder012]
FEATURE [Part::MultiFuse] Fusion018
  Placement = pos=(3.25,0,7) rot=(0,0,1;0rad)
  Shapes = -> [Cylinder016,Cylinder015]
FEATURE [Part::MultiFuse] Fusion019
  Placement = pos=(0,3,5) rot=(0,0,1;0rad)
  Shapes = -> [Fusion017,Fusion018]
FEATURE [Part::Cut] Cut003
  Base = -> Box007
  Tool = -> Fusion019
FEATURE [Part::Fillet] Fillet008  label="converterSupport"
  Base = -> Cut003
  Edges = 4 edges r=2: [Edge2,Edge4,Edge13,Edge20]
  Placement = pos=(-63,5,-120) rot=(0,0,1;0rad)
FEATURE [Part::Extrusion] Extrude
  Base = -> Sketch
  Dir = (0,-1,2e-16)
  DirMode = 2
  FaceMakerClass = Part::FaceMakerBullseye
  LengthFwd = 4
  LengthRev = 0
  Solid = true
  Symmetric = false
FEATURE [Part::Feature] Part__Feature097  label="WPMB-M4-003"
  Placement = pos=(178.445,24.1619,-13.4251) rot=(0,1,0;3.14159rad)
  shape: bbox 91.99 x 91.99 x 12.05 mm, 899 faces (baked)
FEATURE [Sketcher::SketchObject] Sketch001
  FullyConstrained = true
  MapMode = 3
  Placement = pos=(178.445,24.1619,-13.4251) rot=(0,0.707107,-0.707107;3.14159rad)
  Support = -> [Part__Feature097]
  sketch-geometry (32):
    g0: LineSegment StartX=99 StartY=265 StartZ=0 EndX=261 EndY=265 EndZ=0
    g1: LineSegment StartX=261 StartY=265 StartZ=0 EndX=261 EndY=40 EndZ=0
    g2: LineSegment StartX=261 StartY=40 StartZ=0 EndX=99 EndY=40 EndZ=0
    g3: LineSegment StartX=99 StartY=40 StartZ=0 EndX=99 EndY=265 EndZ=0
    g4: Circle CenterX=103.5 CenterY=260.4 CenterZ=0 NormalX=0 NormalY=0 NormalZ=1 AngleXU=0 Radius=1.25
    g5: Circle CenterX=256.5 CenterY=260.4 CenterZ=0 NormalX=0 NormalY=0 NormalZ=1 AngleXU=0 Radius=1.25
    g6: Circle CenterX=103.5 CenterY=152.4 CenterZ=0 NormalX=0 NormalY=0 NormalZ=1 AngleXU=0 Radius=1.25
    g7: Circle CenterX=103.5 CenterY=44.4 CenterZ=0 NormalX=0 NormalY=0 NormalZ=1 AngleXU=0 Radius=1.25
    g8: Circle CenterX=256.5 CenterY=44.4 CenterZ=0 NormalX=0 NormalY=0 NormalZ=1 AngleXU=0 Radius=1.25
    g9: Circle CenterX=256.5 CenterY=152.4 CenterZ=0 NormalX=0 NormalY=0 NormalZ=1 AngleXU=0 Radius=1.25
    g10: Circle CenterX=213.46 CenterY=229.1 CenterZ=0 NormalX=0 NormalY=0 NormalZ=1 AngleXU=0 Radius=1.25
    g11: Circle CenterX=231.46 CenterY=229.1 CenterZ=0 NormalX=0 NormalY=0 NormalZ=1 AngleXU=0 Radius=1.25
    g12: Circle CenterX=213.46 CenterY=194.1 CenterZ=0 NormalX=0 NormalY=0 NormalZ=1 AngleXU=0 Radius=1.25
    g13: Circle CenterX=231.46 CenterY=194.1 CenterZ=0 NormalX=0 NormalY=0 NormalZ=1 AngleXU=0 Radius=1.25
    g14: Circle CenterX=245.95 CenterY=207.08 CenterZ=0 NormalX=0 NormalY=0 NormalZ=1 AngleXU=0 Radius=1.625
    g15: Circle CenterX=196.95 CenterY=207.08 CenterZ=0 NormalX=0 NormalY=0 NormalZ=1 AngleXU=0 Radius=1.625
    g16: Circle CenterX=245.95 CenterY=149.08 CenterZ=0 NormalX=0 NormalY=0 NormalZ=1 AngleXU=0 Radius=1.625
    g17: Circle CenterX=196.95 CenterY=149.08 CenterZ=0 NormalX=0 NormalY=0 NormalZ=1 AngleXU=0 Radius=1.625
    g18: Circle CenterX=208.2 CenterY=101.58 CenterZ=0 NormalX=0 NormalY=0 NormalZ=1 AngleXU=0 Radius=1.25
    g19: Circle CenterX=208.2 CenterY=94.58 CenterZ=0 NormalX=0 NormalY=0 NormalZ=1 AngleXU=0 Radius=1.25
    g20: Circle CenterX=238.2 CenterY=101.58 CenterZ=0 NormalX=0 NormalY=0 NormalZ=1 AngleXU=0 Radius=1.25
    g21: Circle CenterX=246.2 CenterY=62.1 CenterZ=0 NormalX=0 NormalY=0 NormalZ=1 AngleXU=0 Radius=1.625
    g22: Circle CenterX=200.7 CenterY=62.1 CenterZ=0 NormalX=0 NormalY=0 NormalZ=1 AngleXU=0 Radius=1.625
    g23: Circle CenterX=238.2 CenterY=94.58 CenterZ=0 NormalX=0 NormalY=0 NormalZ=1 AngleXU=0 Radius=1.25
    g24: Circle CenterX=138 CenterY=105 CenterZ=0 NormalX=0 NormalY=0 NormalZ=1 AngleXU=0 Radius=5
    g25: Circle CenterX=156.7 CenterY=105 CenterZ=0 NormalX=0 NormalY=0 NormalZ=1 AngleXU=0 Radius=5
    g26: Circle CenterX=138 CenterY=255 CenterZ=0 NormalX=0 NormalY=0 NormalZ=1 AngleXU=0 Radius=5
    g27: Circle CenterX=156.7 CenterY=255 CenterZ=0 NormalX=0 NormalY=0 NormalZ=1 AngleXU=0 Radius=5
    g28: Circle CenterX=110 CenterY=220 CenterZ=0 NormalX=0 NormalY=0 NormalZ=1 AngleXU=0 Radius=5
    g29: Circle CenterX=184.8 CenterY=220 CenterZ=0 NormalX=0 NormalY=0 NormalZ=1 AngleXU=0 Radius=5
    g30: Circle CenterX=110 CenterY=170 CenterZ=0 NormalX=0 NormalY=0 NormalZ=1 AngleXU=0 Radius=5
    g31: Circle CenterX=184.8 CenterY=170 CenterZ=0 NormalX=0 NormalY=0 NormalZ=1 AngleXU=0 Radius=5
  constraints (86):
    c: Coincident(g0,g1)
    c: Coincident(g1,g2)
    c: Coincident(g2,g3)
    c: Coincident(g3,g0)
    c: Horizontal(g0)
    c: Horizontal(g2)
    c: Vertical(g1)
    c: Vertical(g3)
    c: DistanceX(g2) = 99
    c: DistanceX(g1) = 261
    c: DistanceY(g2) = 40
    c: DistanceY(g0) = 265
    c: Equal(g18,g19)
    c: Equal(g18,g20)
    c: Equal(g18,g23)
    c: Equal(g18,g9)
    c: Equal(g18, g4-g8) x5
    c: Equal(g18, g10-g13) x4
    c: Radius(g18) = 1.25
    c: DistanceX(g7) = 103.5
    c: DistanceY(g7) = 44.4
    c: DistanceX(g7,g6) = 0
    c: DistanceX(g4,g6) = 0
    c: DistanceX(g7,g8) = 153
    c: DistanceY(g7,g8) = 0
    c: DistanceY(g6,g9) = 0
    c: DistanceY(g5,g4) = 0
    c: DistanceX(g8,g9) = 0
    c: DistanceX(g9,g5) = 0
    c: DistanceX(g17) = 196.95
    c: DistanceY(g17) = 149.08
    c: Equal(g14,g16)
    c: Equal(g14,g17)
    c: Equal(g14,g15)
    c: Diameter(g14) = 3.25
    c: DistanceX(g17,g16) = 49
    c: DistanceY(g17,g16) = 0
    c: DistanceY(g17,g15) = 58
    c: DistanceX(g17,g15) = 0
    c: DistanceY(g14,g15) = 0
    c: DistanceX(g14,g16) = 0
    c: DistanceX(g12) = 213.46
    c: DistanceY(g12) = 194.1
    c: DistanceY(g13,g12) = 0
    c: DistanceX(g12,g13) = 18
    c: DistanceX(g10,g12) = 0
    c: DistanceX(g11,g13) = 0
    c: DistanceY(g12,g10) = 35
    c: DistanceY(g11,g10) = 0
    c: Equal(g24,g25)
    c: Equal(g24,g30)
    c: Equal(g24,g31)
    c: Equal(g24, g26-g29) x4
    c: Diameter(g24) = 10
    c: DistanceY(g24) = 105
    c: DistanceY(g25,g24) = 0
    c: DistanceX(g24) = 138
    c: DistanceX(g24,g25) = 18.7
    c: DistanceY(g24,g26) = 150
    c: DistanceX(g26,g24) = 0
    c: DistanceX(g27,g25) = 0
    c: DistanceY(g26,g27) = 0
    c: DistanceX(g30) = 110
    c: DistanceY(g30) = 170
    c: DistanceY(g30,g31) = 0
    c: DistanceX(g30,g31) = 74.8
    c: DistanceY(g30,g28) = 50
    c: DistanceY(g28,g29) = 0
    c: DistanceX(g28,g30) = 0
    c: DistanceX(g31,g29) = 0
    c: DistanceY(g7,g4) = 216
    c: DistanceX(g7,g22) = 97.2
    c: DistanceY(g22,g21) = 0
    c: DistanceX(g22,g21) = 45.5
    c: DistanceY(g22) = 62.1
    c: DistanceX(g7,g19) = 104.7
    c: DistanceY(g19) = 94.58
    c: DistanceX(g18,g19) = 0
    c: DistanceY(g19,g18) = 7
    c: DistanceX(g19,g23) = 30
    c: DistanceY(g23,g19) = 0
    c: DistanceX(g23,g20) = 0
    c: DistanceY(g18,g20) = 0
    c: Equal(g22,g21)
    c: Diameter(g22) = 3.25
    c: DistanceY(g7,g6) = 108
FEATURE [Part::Extrusion] Extrude001
  Base = -> Sketch001
  Dir = (0,-1,-2e-16)
  DirMode = 2
  FaceMakerClass = Part::FaceMakerBullseye
  LengthFwd = 4
  LengthRev = 0
  Placement = pos=(0,0,0) rot=(1,0,0;1.5708rad)
  Solid = true
  Symmetric = false
FEATURE [Part::Feature] Part__Feature098  label="47065T801_T-Slotted Framing001"
  Placement = pos=(0,0,-360) rot=(1,0,0;1.5708rad)
  shape: bbox 25.4 x 152.4 x 25.4 mm, 108 faces (baked)
FEATURE [Part::Feature] Part__Feature099  label="47065T801_T-Slotted Framing002"
  Placement = pos=(0,-300,-360) rot=(1,0,0;1.5708rad)
  shape: bbox 25.4 x 152.4 x 25.4 mm, 108 faces (baked)
FEATURE [Part::Feature] Part__Feature100  label="47065T801_T-Slotted Framing003"
  Placement = pos=(0,-151,-360) rot=(1,0,0;1.5708rad)
  shape: bbox 25.4 x 152.4 x 25.4 mm, 108 faces (baked)
FEATURE [Part::MultiFuse] Fusion020  label="tSlotFrame"
  Placement = pos=(0,0,40) rot=(0,0,1;0rad)
  Shapes = -> [Part__Feature100,Part__Feature098,Part__Feature099]
FEATURE [Part::Box] Box041  label="Cube029"
  AttacherType = Attacher::AttachEngine3D
  Height = 15
  Length = 28
  Placement = pos=(60,-103.5,-81) rot=(0,0,1;0rad)
  Width = 54
FEATURE [Part::Cylinder] Cylinder055
  Angle = 360
  AttacherType = Attacher::AttachEngine3D
  FirstAngle = 0
  Height = 15
  Placement = pos=(73.5,-135,-81) rot=(0,0,1;0rad)
  Radius = 35
  SecondAngle = 0
FEATURE [Part::Sphere] Sphere002  label="rainDome"
  Angle1 = -90
  Angle2 = 90
  Angle3 = 180
  AttacherType = Attacher::AttachEngine3D
  Placement = pos=(73.5,-135,-66) rot=(0.57735,0.57735,0.57735;2.0944rad)
  Radius = 35
FEATURE [Part::MultiFuse] Fusion034  label="rainModule"
  Placement = pos=(300.11,179.11,0) rot=(0,0,1;0.785398rad)
  Shapes = -> [Sphere002,Cylinder055,Box041]
FEATURE [Part::Sphere] Sphere  label="lightDome"
  Angle1 = -90
  Angle2 = 90
  Angle3 = 180
  AttacherType = Attacher::AttachEngine3D
  Placement = pos=(0,-379,-299) rot=(1,0,0;1.5708rad)
  Radius = 30
FEATURE [Part::Feature] Part__Feature101  label="ANT-868-PW-QW-UFL-BODY001"
  shape: bbox 15.69 x 84 x 15.69 mm, 56 faces (baked)
FEATURE [Part::Feature] Part__Feature102  label="Screw001"
  Placement = pos=(0,-7.05,0) rot=(0,0,1;0rad)
  shape: bbox 7.002 x 7.052 x 7.002 mm, 20 faces (baked)
FEATURE [Part::Feature] Part__Feature103  label="Ring001"
  shape: bbox 9.2 x 6 x 9.2 mm, 8 faces, 2 solids (baked)
FEATURE [Part::Compound] Compound002  label="loraAntenna"
  Links = -> [Part__Feature103,Part__Feature101,Part__Feature102]
  Placement = pos=(-0.5,-512,-305.5) rot=(0.57735,-0.57735,-0.57735;2.0944rad)
FEATURE [Part::Feature] Part__Feature104  label="ips7100"
  Placement = pos=(-24,0,222) rot=(0.999993,-0.003655,0;3.14159rad)
  shape: bbox 48.14 x 14.05 x 44.14 mm, 1935 faces (baked)
FEATURE [Part::Compound] Compound  label="ips7100s"
  Links = -> [Part__Feature104]
  Placement = pos=(24,-268,-308) rot=(0,0,1;0.006109rad)
FEATURE [Part::Feature] Part__Feature105  label="Printed Circuit Board"
  shape: bbox 25.4 x 17.78 x 1.6 mm, 42 faces (baked)
FEATURE [Part::Feature] Part__Feature106  label="EAHC2835WD6"
  shape: bbox 3.513 x 2.813 x 0.7485 mm, 108 faces, 4 solids (baked)
FEATURE [Part::Feature] Part__Feature107  label="AS7341 v2"
  Placement = pos=(0,-0.339822,1.6) rot=(0,0,1;0rad)
  shape: bbox 2 x 3.1 x 1.1 mm, 267 faces, 26 solids (baked)
FEATURE [Part::Feature] Part__Feature108  label="CAPC-0805-T0.95-BN v1"
  Placement = pos=(-5.01759,-3.15294,1.6) rot=(0,0,1;0rad)
  shape: bbox 2.1 x 1.35 x 0.95 mm, 42 faces (baked)
FEATURE [Part::Feature] Part__Feature109  label="CAPC-0805-T0.95-BN v002"
  Placement = pos=(-5.48627,2.66154,1.6) rot=(0,0,-1;1.5708rad)
  shape: bbox 1.35 x 2.1 x 0.95 mm, 42 faces (baked)
FEATURE [Part::Feature] Part__Feature110  label="CAPC-0805-T0.95-BN v003"
  Placement = pos=(-3.43627,2.66154,1.6) rot=(0,0,-1;1.5708rad)
  shape: bbox 1.35 x 2.1 x 0.95 mm, 42 faces (baked)
FEATURE [Part::Feature] Part__Feature111  label="CAPC-0603-T0.9-BN v1"
  Placement = pos=(-1.69987,-3.28475,1.6) rot=(0,0,1;0rad)
  shape: bbox 1.7 x 0.9 x 0.9 mm, 42 faces (baked)
FEATURE [Part::Feature] Part__Feature112  label="BODY_MF06A"
  Placement = pos=(0,0,0.762) rot=(0.57735,-0.57735,-0.57735;2.0944rad)
  shape: bbox 1.601 x 2.921 x 1.016 mm, 42 faces (baked)
FEATURE [Part::Feature] Part__Feature113  label="LEAD_MF06A"
  Placement = pos=(-0.9652,-0.9525,0.1016) rot=(0.57735,-0.57735,-0.57735;2.0944rad)
  shape: bbox 0.6223 x 0.3749 x 0.8636 mm, 14 faces (baked)
FEATURE [Part::Feature] Part__Feature114  label="LEAD_MF06A001"
  Placement = pos=(-0.9652,0,0.1016) rot=(0.57735,-0.57735,-0.57735;2.0944rad)
  shape: bbox 0.6223 x 0.3749 x 0.8636 mm, 14 faces (baked)
FEATURE [Part::Feature] Part__Feature115  label="LEAD_MF06A002"
  Placement = pos=(-0.9652,0.9525,0.1016) rot=(0.57735,-0.57735,-0.57735;2.0944rad)
  shape: bbox 0.6223 x 0.3749 x 0.8636 mm, 14 faces (baked)
FEATURE [Part::Feature] Part__Feature116  label="LEAD_MF06A003"
  Placement = pos=(0.9652,-0.9525,0.1016) rot=(0.57735,0.57735,0.57735;2.0944rad)
  shape: bbox 0.6223 x 0.3749 x 0.8636 mm, 14 faces (baked)
FEATURE [Part::Feature] Part__Feature117  label="LEAD_MF06A004"
  Placement = pos=(0.9652,0,0.1016) rot=(0.57735,0.57735,0.57735;2.0944rad)
  shape: bbox 0.6223 x 0.3749 x 0.8636 mm, 14 faces (baked)
FEATURE [Part::Feature] Part__Feature118  label="LEAD_MF06A005"
  Placement = pos=(0.9652,0.9525,0.1016) rot=(0.57735,0.57735,0.57735;2.0944rad)
  shape: bbox 0.6223 x 0.3749 x 0.8636 mm, 14 faces (baked)
FEATURE [Part::Feature] Part__Feature119  label="SOT363 v2"
  Placement = pos=(4.97054,-0.645171,1.675) rot=(0,0,1;3.14159rad)
  shape: bbox 2.1 x 2 x 1.1 mm, 94 faces, 7 solids (baked)
FEATURE [Part::Feature] Part__Feature120  label="LED 0603 single color v1"
  Placement = pos=(-9.18406,3.72778,1.60762) rot=(0,0,1;1.5708rad)
  shape: bbox 1.961 x 0.7932 x 0.7145 mm, 63 faces, 5 solids (baked)
FEATURE [Part::Feature] Part__Feature121  label="RESC-0603 v1"
  Placement = pos=(4.83432,-3.67461,1.6) rot=(0,0,1;0rad)
  shape: bbox 1.7 x 0.9 x 0.55 mm, 52 faces, 3 solids (baked)
FEATURE [Part::Feature] Part__Feature122  label="RESC-0603 v002"
  Placement = pos=(-7.14949,3.61248,1.6) rot=(0,0,-1;1.5708rad)
  shape: bbox 0.9 x 1.7 x 0.55 mm, 52 faces, 3 solids (baked)
FEATURE [Part::Feature] Part__Feature123  label="YC164_RESPACK v1"
  Placement = pos=(2.99591,1.52916,1.6) rot=(0,0,1;0rad)
  shape: bbox 3.2 x 1.6 x 0.61 mm, 172 faces (baked)
FEATURE [Part::Feature] Part__Feature124  label="qwicc v2"
  Placement = pos=(-10.8364,0.0607456,1.65) rot=(0,0,-1;1.5708rad)
  shape: bbox 4.95 x 6 x 2.96 mm, 229 faces, 7 solids (baked)
FEATURE [Part::Feature] Part__Feature125  label="qwicc v003"
  Placement = pos=(10.8256,0.00556102,1.65) rot=(0,0,1;1.5708rad)
  shape: bbox 4.95 x 6 x 2.96 mm, 229 faces, 7 solids (baked)
FEATURE [Part::Feature] Part__Feature126  label="scd30"
  Placement = pos=(-23,-300.5,-288) rot=(0.707107,0,-0.707107;3.14159rad)
  shape: bbox 23.02 x 7.027 x 35.11 mm, 2292 faces, 25 solids (baked)
FEATURE [App::Part] sot_23_6_v2  label="sot-23-6 v2"
  Group = -> [Part__Feature112,Part__Feature113,Part__Feature114,Part__Feature115,Part__Feature116,Part__Feature117,Part__Feature118]
  Origin = -> Origin008
  Placement = pos=(-4.47945,-0.603742,1.69152) rot=(0,0,1;0rad)
FEATURE [App::Part] Adafruit_AS7341_STEMMA_QT_v2  label="bme280"
  Group = -> [Part__Feature105,Part__Feature106,Part__Feature107,Part__Feature108,Part__Feature109,Part__Feature110,Part__Feature111,sot_23_6_v2,Part__Feature119,Part__Feature120,Part__Feature121,Part__Feature122,Part__Feature123,Part__Feature124,Part__Feature125]
  Origin = -> Origin009
  Placement = pos=(10,-301,-298) rot=(-1,0,0;4.71239rad)
FEATURE [Part::Feature] Part__Feature127  label="Board"
  shape: bbox 25.4 x 25.4 x 1.57 mm, 211 faces (baked)
FEATURE [Part::Feature] Part__Feature128  label="QFN24_4MM"
  Placement = pos=(12.1412,14.4526,1.57) rot=(0,0,1;3.92699rad)
  shape: bbox 5.657 x 5.657 x 0.9 mm, 172 faces (baked)
FEATURE [Part::Feature] Part__Feature129  label="Part 5"
  shape: bbox 0.48 x 0.6603 x 0.6 mm, 14 faces (baked)
FEATURE [Part::Feature] Part__Feature130  label="Part 6"
  shape: bbox 0.48 x 0.6603 x 0.6 mm, 14 faces (baked)
FEATURE [Part::Feature] Part__Feature131  label="Part 4"
  shape: bbox 0.48 x 0.6603 x 0.6 mm, 14 faces (baked)
FEATURE [Part::Feature] Part__Feature132  label="Part 3"
  shape: bbox 0.48 x 0.6603 x 0.6 mm, 14 faces (baked)
FEATURE [Part::Feature] Part__Feature133  label="Part 010"
  shape: bbox 0.48 x 0.6603 x 0.6 mm, 14 faces (baked)
FEATURE [Part::Feature] Part__Feature134  label="Part 011"
  shape: bbox 3 x 1.4 x 1 mm, 10 faces (baked)
FEATURE [Part::Feature] Part__Feature135  label="Pin1"
  shape: bbox 0.6224 x 1.252 x 1.252 mm, 37 faces (baked)
FEATURE [Part::Feature] Part__Feature136  label="Pin2"
  shape: bbox 0.6224 x 1.252 x 1.252 mm, 37 faces (baked)
FEATURE [Part::Feature] Part__Feature137  label="CeramicBody"
  shape: bbox 1.8 x 1.23 x 1.23 mm, 10 faces (baked)
FEATURE [Part::Feature] Part__Feature138  label="0603-NO (1)"
  Placement = pos=(23.241,6.223,1.57) rot=(0,0,1;0rad)
  shape: bbox 1.7 x 0.9 x 0.55 mm, 52 faces, 3 solids (baked)
FEATURE [Part::Feature] Part__Feature139  label="0603-NO (2)"
  Placement = pos=(13.3858,8.4328,1.57) rot=(0,0,1;0rad)
  shape: bbox 1.7 x 0.9 x 0.55 mm, 52 faces, 3 solids (baked)
FEATURE [Part::Feature] Part__Feature140  label="0603-NO (3)"
  Placement = pos=(1.905,18.923,1.57) rot=(0,0,1;3.14159rad)
  shape: bbox 1.7 x 0.9 x 0.55 mm, 52 faces, 3 solids (baked)
FEATURE [Part::Feature] Part__Feature141  label="Pin1 (1)"
  shape: bbox 0.6224 x 1.252 x 1.252 mm, 37 faces (baked)
FEATURE [Part::Feature] Part__Feature142  label="Pin2 (1)"
  shape: bbox 0.6224 x 1.252 x 1.252 mm, 37 faces (baked)
FEATURE [Part::Feature] Part__Feature040  label="CeramicBody (1)"
  shape: bbox 1.8 x 1.23 x 1.23 mm, 10 faces (baked)
FEATURE [Part::Feature] Part__Feature143  label="Pin1 (2)"
  shape: bbox 0.6224 x 1.252 x 1.252 mm, 37 faces (baked)
FEATURE [Part::Feature] Part__Feature144  label="Pin2 (2)"
  shape: bbox 0.6224 x 1.252 x 1.252 mm, 37 faces (baked)
FEATURE [Part::Feature] Part__Feature145  label="CeramicBody (2)"
  shape: bbox 1.8 x 1.23 x 1.23 mm, 10 faces (baked)
FEATURE [Part::Feature] Part__Feature146  label="CHIPLED_0603_NOOUTLINE"
  Placement = pos=(23.368,8.509,1.57) rot=(0,0,1;1.5708rad)
  shape: bbox 1.616 x 0.8 x 0.4 mm, 133 faces (baked)
FEATURE [Part::Feature] Part__Feature147  label="CHIPLED_0603_NOOUTLINE (1)"
  Placement = pos=(1.905,16.764,1.57) rot=(0,0,-1;1.5708rad)
  shape: bbox 1.616 x 0.8 x 0.4 mm, 133 faces (baked)
FEATURE [Part::Feature] Part__Feature148  label="JST_SH4"
  Placement = pos=(22.86,12.7,1.57) rot=(0,0,1;1.5708rad)
  shape: bbox 4.95 x 6 x 2.96 mm, 229 faces, 7 solids (baked)
FEATURE [Part::Feature] Part__Feature149  label="JST_SH4 (1)"
  Placement = pos=(2.54,12.7,1.57) rot=(0,0,-1;1.5708rad)
  shape: bbox 4.95 x 6 x 2.96 mm, 229 faces, 7 solids (baked)
FEATURE [Part::Feature] Part__Feature150  label="NEO3535_REVERSE"
  Placement = pos=(12.7,23.114,0) rot=(0,1,0;3.14159rad)
  shape: bbox 5.88 x 2.8 x 1.78 mm, 41 faces, 5 solids (baked)
FEATURE [Part::Feature] Part__Feature151  label="RESPACK_4X0603"
  Placement = pos=(22.86,18.415,1.57) rot=(0,0,1;3.14159rad)
  shape: bbox 3.2 x 1.6 x 0.61 mm, 172 faces (baked)
FEATURE [Part::Feature] Part__Feature152  label="SOT363"
  Placement = pos=(17.399,12.192,1.57) rot=(0,0,-1;1.5708rad)
  shape: bbox 2.208 x 2.208 x 1.121 mm, 178 faces, 4 solids (baked)
FEATURE [App::Part] _603_NO  label="0603-NO"
  Group = -> [Part__Feature135,Part__Feature136,Part__Feature137]
  Origin = -> Origin012
  Placement = pos=(16.51,8.382,1.57) rot=(0,0,1;0rad)
FEATURE [App::Part] _6700497  label="36700497"
  Group = -> [Part__Feature129,Part__Feature130,Part__Feature131,Part__Feature132,Part__Feature133,Part__Feature134]
  Origin = -> Origin010
  Placement = pos=(0,0,0) rot=(0,0,1;3.14159rad)
FEATURE [App::Part] SOT23_5  label="SOT23-5"
  Group = -> [_6700497]
  Origin = -> Origin011
  Placement = pos=(2.54,6.985,1.57) rot=(0,0,1;3.14159rad)
FEATURE [App::Part] _805_NO  label="0805-NO"
  Group = -> [Part__Feature141,Part__Feature142,Part__Feature040]
  Origin = -> Origin013
  Placement = pos=(7.874,13.589,1.57) rot=(0,0,1;1.5708rad)
FEATURE [App::Part] _805_NO__1_  label="0805-NO (1)"
  Group = -> [Part__Feature143,Part__Feature144,Part__Feature145]
  Origin = -> Origin014
  Placement = pos=(12.827,6.223,1.57) rot=(0,0,1;3.14159rad)
FEATURE [App::Part] Packages
  Group = -> [Part__Feature128,SOT23_5,_603_NO,Part__Feature138,Part__Feature139,Part__Feature140,_805_NO,_805_NO__1_,Part__Feature146,Part__Feature147,Part__Feature148,Part__Feature149,Part__Feature150,Part__Feature151,Part__Feature152]
  Origin = -> Origin015
FEATURE [App::Part] Adafruit_I2C_QT_Rotary_Encoder_v2  label="gps"
  Group = -> [Part__Feature127,Packages]
  Origin = -> Origin016
  Placement = pos=(-16,-306,-258) rot=(0,0,1;0rad)
FEATURE [Sketcher::SketchObject] Sketch003  label="inner"
  FullyConstrained = true
  Placement = pos=(0,0,-259.26) rot=(0,0,1;0rad)
  sketch-geometry (4):
    g0: LineSegment StartX=-36 StartY=-277 StartZ=0 EndX=-36 EndY=-327 EndZ=0
    g1: LineSegment StartX=-36 StartY=-327 StartZ=0 EndX=36 EndY=-327 EndZ=0
    g2: LineSegment StartX=36 StartY=-327 StartZ=0 EndX=36 EndY=-277 EndZ=0
    g3: LineSegment StartX=36 StartY=-277 StartZ=0 EndX=-36 EndY=-277 EndZ=0
  constraints (12):
    c: Vertical(g0)
    c: Coincident(g1,g0)
    c: Horizontal(g1)
    c: Coincident(g2,g1)
    c: Vertical(g2)
    c: Coincident(g3,g2)
    c: Coincident(g3,g0)
    c: Horizontal(g3)
    c: DistanceX(g0) = -36
    c: DistanceX(g1) = 36
    c: DistanceY(g0) = -327
    c: DistanceY(g0,g0) = 50
FEATURE [Sketcher::SketchObject] Sketch004  label="outer"
  FullyConstrained = true
  Placement = pos=(0,0,-281.2) rot=(0,0,1;0rad)
  sketch-geometry (4):
    g0: LineSegment StartX=-65 StartY=-252 StartZ=0 EndX=-65 EndY=-352 EndZ=0
    g1: LineSegment StartX=-65 StartY=-352 StartZ=0 EndX=65 EndY=-352 EndZ=0
    g2: LineSegment StartX=65 StartY=-352 StartZ=0 EndX=65 EndY=-252 EndZ=0
    g3: LineSegment StartX=65 StartY=-252 StartZ=0 EndX=-65 EndY=-252 EndZ=0
  constraints (12):
    c: Vertical(g0)
    c: Coincident(g1,g0)
    c: Horizontal(g1)
    c: Coincident(g2,g1)
    c: Vertical(g2)
    c: Coincident(g3,g2)
    c: Coincident(g3,g0)
    c: Horizontal(g3)
    c: DistanceX(g0) = -65
    c: DistanceX(g1) = 65
    c: DistanceY(g0) = -352
    c: DistanceY(g0,g0) = 100
FEATURE [Part::Loft] Loft
  Closed = false
  MaxDegree = 5
  Ruled = false
  Sections = -> [Sketch003,Sketch004]
  Solid = true
FEATURE [Part::Fillet] Fillet
  Base = -> Loft
  Edges = 12 edges r=3: [Edge1,Edge2,Edge3,Edge4,Edge5,Edge6,Edge7,Edge8,Edge9,Edge10,Edge11,Edge12]
FEATURE [Sketcher::SketchObject] Sketch005  label="inner001"
  FullyConstrained = true
  Placement = pos=(0,0,-259.26) rot=(0,0,1;0rad)
  sketch-geometry (4):
    g0: LineSegment StartX=-36 StartY=-277 StartZ=0 EndX=-36 EndY=-327 EndZ=0
    g1: LineSegment StartX=-36 StartY=-327 StartZ=0 EndX=36 EndY=-327 EndZ=0
    g2: LineSegment StartX=36 StartY=-327 StartZ=0 EndX=36 EndY=-277 EndZ=0
    g3: LineSegment StartX=36 StartY=-277 StartZ=0 EndX=-36 EndY=-277 EndZ=0
  constraints (12):
    c: Vertical(g0)
    c: Coincident(g1,g0)
    c: Horizontal(g1)
    c: Coincident(g2,g1)
    c: Vertical(g2)
    c: Coincident(g3,g2)
    c: Coincident(g3,g0)
    c: Horizontal(g3)
    c: DistanceX(g0) = -36
    c: DistanceX(g1) = 36
    c: DistanceY(g0) = -327
    c: DistanceY(g0,g0) = 50
FEATURE [Sketcher::SketchObject] Sketch006  label="outer001"
  FullyConstrained = true
  Placement = pos=(0,0,-281.2) rot=(0,0,1;0rad)
  sketch-geometry (4):
    g0: LineSegment StartX=-65 StartY=-252 StartZ=0 EndX=-65 EndY=-352 EndZ=0
    g1: LineSegment StartX=-65 StartY=-352 StartZ=0 EndX=65 EndY=-352 EndZ=0
    g2: LineSegment StartX=65 StartY=-352 StartZ=0 EndX=65 EndY=-252 EndZ=0
    g3: LineSegment StartX=65 StartY=-252 StartZ=0 EndX=-65 EndY=-252 EndZ=0
  constraints (12):
    c: Vertical(g0)
    c: Coincident(g1,g0)
    c: Horizontal(g1)
    c: Coincident(g2,g1)
    c: Vertical(g2)
    c: Coincident(g3,g2)
    c: Coincident(g3,g0)
    c: Horizontal(g3)
    c: DistanceX(g0) = -65
    c: DistanceX(g1) = 65
    c: DistanceY(g0) = -352
    c: DistanceY(g0,g0) = 100
FEATURE [Part::Loft] Loft001
  Closed = false
  MaxDegree = 5
  Ruled = false
  Sections = -> [Sketch005,Sketch006]
  Solid = true
FEATURE [Part::Fillet] Fillet009
  Base = -> Loft001
  Edges = 12 edges r=3: [Edge1,Edge2,Edge3,Edge4,Edge5,Edge6,Edge7,Edge8,Edge9,Edge10,Edge11,Edge12]
  Placement = pos=(0,0,-4) rot=(0,0,1;0rad)
FEATURE [Part::Cut] Cut  label="sls01"
  Base = -> Fillet
  Tool = -> Fillet009
FEATURE [Sketcher::SketchObject] Sketch007  label="inner002"
  FullyConstrained = true
  Placement = pos=(0,0,-259.26) rot=(0,0,1;0rad)
  sketch-geometry (4):
    g0: LineSegment StartX=-36 StartY=-277 StartZ=0 EndX=-36 EndY=-327 EndZ=0
    g1: LineSegment StartX=-36 StartY=-327 StartZ=0 EndX=36 EndY=-327 EndZ=0
    g2: LineSegment StartX=36 StartY=-327 StartZ=0 EndX=36 EndY=-277 EndZ=0
    g3: LineSegment StartX=36 StartY=-277 StartZ=0 EndX=-36 EndY=-277 EndZ=0
  constraints (12):
    c: Vertical(g0)
    c: Coincident(g1,g0)
    c: Horizontal(g1)
    c: Coincident(g2,g1)
    c: Vertical(g2)
    c: Coincident(g3,g2)
    c: Coincident(g3,g0)
    c: Horizontal(g3)
    c: DistanceX(g0) = -36
    c: DistanceX(g1) = 36
    c: DistanceY(g0) = -327
    c: DistanceY(g0,g0) = 50
FEATURE [Sketcher::SketchObject] Sketch008  label="outer002"
  FullyConstrained = true
  Placement = pos=(0,0,-281.2) rot=(0,0,1;0rad)
  sketch-geometry (4):
    g0: LineSegment StartX=-65 StartY=-252 StartZ=0 EndX=-65 EndY=-352 EndZ=0
    g1: LineSegment StartX=-65 StartY=-352 StartZ=0 EndX=65 EndY=-352 EndZ=0
    g2: LineSegment StartX=65 StartY=-352 StartZ=0 EndX=65 EndY=-252 EndZ=0
    g3: LineSegment StartX=65 StartY=-252 StartZ=0 EndX=-65 EndY=-252 EndZ=0
  constraints (12):
    c: Vertical(g0)
    c: Coincident(g1,g0)
    c: Horizontal(g1)
    c: Coincident(g2,g1)
    c: Vertical(g2)
    c: Coincident(g3,g2)
    c: Coincident(g3,g0)
    c: Horizontal(g3)
    c: DistanceX(g0) = -65
    c: DistanceX(g1) = 65
    c: DistanceY(g0) = -352
    c: DistanceY(g0,g0) = 100
FEATURE [Part::Loft] Loft002
  Closed = false
  MaxDegree = 5
  Ruled = false
  Sections = -> [Sketch007,Sketch008]
  Solid = true
FEATURE [Part::Fillet] Fillet010
  Base = -> Loft002
  Edges = 12 edges r=3: [Edge1,Edge2,Edge3,Edge4,Edge5,Edge6,Edge7,Edge8,Edge9,Edge10,Edge11,Edge12]
FEATURE [Sketcher::SketchObject] Sketch009  label="inner003"
  FullyConstrained = true
  Placement = pos=(0,0,-259.26) rot=(0,0,1;0rad)
  sketch-geometry (4):
    g0: LineSegment StartX=-36 StartY=-277 StartZ=0 EndX=-36 EndY=-327 EndZ=0
    g1: LineSegment StartX=-36 StartY=-327 StartZ=0 EndX=36 EndY=-327 EndZ=0
    g2: LineSegment StartX=36 StartY=-327 StartZ=0 EndX=36 EndY=-277 EndZ=0
    g3: LineSegment StartX=36 StartY=-277 StartZ=0 EndX=-36 EndY=-277 EndZ=0
  constraints (12):
    c: Vertical(g0)
    c: Coincident(g1,g0)
    c: Horizontal(g1)
    c: Coincident(g2,g1)
    c: Vertical(g2)
    c: Coincident(g3,g2)
    c: Coincident(g3,g0)
    c: Horizontal(g3)
    c: DistanceX(g0) = -36
    c: DistanceX(g1) = 36
    c: DistanceY(g0) = -327
    c: DistanceY(g0,g0) = 50
FEATURE [Sketcher::SketchObject] Sketch010  label="outer003"
  FullyConstrained = true
  Placement = pos=(0,0,-281.2) rot=(0,0,1;0rad)
  sketch-geometry (4):
    g0: LineSegment StartX=-65 StartY=-252 StartZ=0 EndX=-65 EndY=-352 EndZ=0
    g1: LineSegment StartX=-65 StartY=-352 StartZ=0 EndX=65 EndY=-352 EndZ=0
    g2: LineSegment StartX=65 StartY=-352 StartZ=0 EndX=65 EndY=-252 EndZ=0
    g3: LineSegment StartX=65 StartY=-252 StartZ=0 EndX=-65 EndY=-252 EndZ=0
  constraints (12):
    c: Vertical(g0)
    c: Coincident(g1,g0)
    c: Horizontal(g1)
    c: Coincident(g2,g1)
    c: Vertical(g2)
    c: Coincident(g3,g2)
    c: Coincident(g3,g0)
    c: Horizontal(g3)
    c: DistanceX(g0) = -65
    c: DistanceX(g1) = 65
    c: DistanceY(g0) = -352
    c: DistanceY(g0,g0) = 100
FEATURE [Part::Loft] Loft003
  Closed = false
  MaxDegree = 5
  Ruled = false
  Sections = -> [Sketch009,Sketch010]
  Solid = true
FEATURE [Part::Fillet] Fillet011
  Base = -> Loft003
  Edges = 12 edges r=3: [Edge1,Edge2,Edge3,Edge4,Edge5,Edge6,Edge7,Edge8,Edge9,Edge10,Edge11,Edge12]
  Placement = pos=(0,0,-4) rot=(0,0,1;0rad)
FEATURE [Part::Cut] Cut004  label="sls002"
  Base = -> Fillet010
  Placement = pos=(0,0,-16) rot=(0,0,1;0rad)
  Tool = -> Fillet011
FEATURE [Sketcher::SketchObject] Sketch011  label="inner004"
  FullyConstrained = true
  Placement = pos=(0,0,-259.26) rot=(0,0,1;0rad)
  sketch-geometry (4):
    g0: LineSegment StartX=-36 StartY=-277 StartZ=0 EndX=-36 EndY=-327 EndZ=0
    g1: LineSegment StartX=-36 StartY=-327 StartZ=0 EndX=36 EndY=-327 EndZ=0
    g2: LineSegment StartX=36 StartY=-327 StartZ=0 EndX=36 EndY=-277 EndZ=0
    g3: LineSegment StartX=36 StartY=-277 StartZ=0 EndX=-36 EndY=-277 EndZ=0
  constraints (12):
    c: Vertical(g0)
    c: Coincident(g1,g0)
    c: Horizontal(g1)
    c: Coincident(g2,g1)
    c: Vertical(g2)
    c: Coincident(g3,g2)
    c: Coincident(g3,g0)
    c: Horizontal(g3)
    c: DistanceX(g0) = -36
    c: DistanceX(g1) = 36
    c: DistanceY(g0) = -327
    c: DistanceY(g0,g0) = 50
FEATURE [Sketcher::SketchObject] Sketch012  label="outer004"
  FullyConstrained = true
  Placement = pos=(0,0,-281.2) rot=(0,0,1;0rad)
  sketch-geometry (4):
    g0: LineSegment StartX=-65 StartY=-252 StartZ=0 EndX=-65 EndY=-352 EndZ=0
    g1: LineSegment StartX=-65 StartY=-352 StartZ=0 EndX=65 EndY=-352 EndZ=0
    g2: LineSegment StartX=65 StartY=-352 StartZ=0 EndX=65 EndY=-252 EndZ=0
    g3: LineSegment StartX=65 StartY=-252 StartZ=0 EndX=-65 EndY=-252 EndZ=0
  constraints (12):
    c: Vertical(g0)
    c: Coincident(g1,g0)
    c: Horizontal(g1)
    c: Coincident(g2,g1)
    c: Vertical(g2)
    c: Coincident(g3,g2)
    c: Coincident(g3,g0)
    c: Horizontal(g3)
    c: DistanceX(g0) = -65
    c: DistanceX(g1) = 65
    c: DistanceY(g0) = -352
    c: DistanceY(g0,g0) = 100
FEATURE [Part::Loft] Loft004
  Closed = false
  MaxDegree = 5
  Ruled = false
  Sections = -> [Sketch011,Sketch012]
  Solid = true
FEATURE [Part::Fillet] Fillet012
  Base = -> Loft004
  Edges = 12 edges r=3: [Edge1,Edge2,Edge3,Edge4,Edge5,Edge6,Edge7,Edge8,Edge9,Edge10,Edge11,Edge12]
FEATURE [Sketcher::SketchObject] Sketch013  label="inner005"
  FullyConstrained = true
  Placement = pos=(0,0,-259.26) rot=(0,0,1;0rad)
  sketch-geometry (4):
    g0: LineSegment StartX=-36 StartY=-277 StartZ=0 EndX=-36 EndY=-327 EndZ=0
    g1: LineSegment StartX=-36 StartY=-327 StartZ=0 EndX=36 EndY=-327 EndZ=0
    g2: LineSegment StartX=36 StartY=-327 StartZ=0 EndX=36 EndY=-277 EndZ=0
    g3: LineSegment StartX=36 StartY=-277 StartZ=0 EndX=-36 EndY=-277 EndZ=0
  constraints (12):
    c: Vertical(g0)
    c: Coincident(g1,g0)
    c: Horizontal(g1)
    c: Coincident(g2,g1)
    c: Vertical(g2)
    c: Coincident(g3,g2)
    c: Coincident(g3,g0)
    c: Horizontal(g3)
    c: DistanceX(g0) = -36
    c: DistanceX(g1) = 36
    c: DistanceY(g0) = -327
    c: DistanceY(g0,g0) = 50
FEATURE [Sketcher::SketchObject] Sketch014  label="outer005"
  FullyConstrained = true
  Placement = pos=(0,0,-281.2) rot=(0,0,1;0rad)
  sketch-geometry (4):
    g0: LineSegment StartX=-65 StartY=-252 StartZ=0 EndX=-65 EndY=-352 EndZ=0
    g1: LineSegment StartX=-65 StartY=-352 StartZ=0 EndX=65 EndY=-352 EndZ=0
    g2: LineSegment StartX=65 StartY=-352 StartZ=0 EndX=65 EndY=-252 EndZ=0
    g3: LineSegment StartX=65 StartY=-252 StartZ=0 EndX=-65 EndY=-252 EndZ=0
  constraints (12):
    c: Vertical(g0)
    c: Coincident(g1,g0)
    c: Horizontal(g1)
    c: Coincident(g2,g1)
    c: Vertical(g2)
    c: Coincident(g3,g2)
    c: Coincident(g3,g0)
    c: Horizontal(g3)
    c: DistanceX(g0) = -65
    c: DistanceX(g1) = 65
    c: DistanceY(g0) = -352
    c: DistanceY(g0,g0) = 100
FEATURE [Part::Loft] Loft005
  Closed = false
  MaxDegree = 5
  Ruled = false
  Sections = -> [Sketch013,Sketch014]
  Solid = true
FEATURE [Part::Fillet] Fillet013
  Base = -> Loft005
  Edges = 12 edges r=3: [Edge1,Edge2,Edge3,Edge4,Edge5,Edge6,Edge7,Edge8,Edge9,Edge10,Edge11,Edge12]
  Placement = pos=(0,0,-4) rot=(0,0,1;0rad)
FEATURE [Part::Cut] Cut005  label="sls003"
  Base = -> Fillet012
  Placement = pos=(0,0,-32) rot=(0,0,1;0rad)
  Tool = -> Fillet013
FEATURE [Sketcher::SketchObject] Sketch015  label="inner006"
  FullyConstrained = true
  Placement = pos=(0,0,-259.26) rot=(0,0,1;0rad)
  sketch-geometry (4):
    g0: LineSegment StartX=-36 StartY=-277 StartZ=0 EndX=-36 EndY=-327 EndZ=0
    g1: LineSegment StartX=-36 StartY=-327 StartZ=0 EndX=36 EndY=-327 EndZ=0
    g2: LineSegment StartX=36 StartY=-327 StartZ=0 EndX=36 EndY=-277 EndZ=0
    g3: LineSegment StartX=36 StartY=-277 StartZ=0 EndX=-36 EndY=-277 EndZ=0
  constraints (12):
    c: Vertical(g0)
    c: Coincident(g1,g0)
    c: Horizontal(g1)
    c: Coincident(g2,g1)
    c: Vertical(g2)
    c: Coincident(g3,g2)
    c: Coincident(g3,g0)
    c: Horizontal(g3)
    c: DistanceX(g0) = -36
    c: DistanceX(g1) = 36
    c: DistanceY(g0) = -327
    c: DistanceY(g0,g0) = 50
FEATURE [Sketcher::SketchObject] Sketch016  label="outer006"
  FullyConstrained = true
  Placement = pos=(0,0,-281.2) rot=(0,0,1;0rad)
  sketch-geometry (4):
    g0: LineSegment StartX=-65 StartY=-252 StartZ=0 EndX=-65 EndY=-352 EndZ=0
    g1: LineSegment StartX=-65 StartY=-352 StartZ=0 EndX=65 EndY=-352 EndZ=0
    g2: LineSegment StartX=65 StartY=-352 StartZ=0 EndX=65 EndY=-252 EndZ=0
    g3: LineSegment StartX=65 StartY=-252 StartZ=0 EndX=-65 EndY=-252 EndZ=0
  constraints (12):
    c: Vertical(g0)
    c: Coincident(g1,g0)
    c: Horizontal(g1)
    c: Coincident(g2,g1)
    c: Vertical(g2)
    c: Coincident(g3,g2)
    c: Coincident(g3,g0)
    c: Horizontal(g3)
    c: DistanceX(g0) = -65
    c: DistanceX(g1) = 65
    c: DistanceY(g0) = -352
    c: DistanceY(g0,g0) = 100
FEATURE [Part::Loft] Loft006
  Closed = false
  MaxDegree = 5
  Ruled = false
  Sections = -> [Sketch015,Sketch016]
  Solid = true
FEATURE [Part::Fillet] Fillet014
  Base = -> Loft006
  Edges = 12 edges r=3: [Edge1,Edge2,Edge3,Edge4,Edge5,Edge6,Edge7,Edge8,Edge9,Edge10,Edge11,Edge12]
FEATURE [Sketcher::SketchObject] Sketch017  label="inner007"
  FullyConstrained = true
  Placement = pos=(0,0,-259.26) rot=(0,0,1;0rad)
  sketch-geometry (4):
    g0: LineSegment StartX=-36 StartY=-277 StartZ=0 EndX=-36 EndY=-327 EndZ=0
    g1: LineSegment StartX=-36 StartY=-327 StartZ=0 EndX=36 EndY=-327 EndZ=0
    g2: LineSegment StartX=36 StartY=-327 StartZ=0 EndX=36 EndY=-277 EndZ=0
    g3: LineSegment StartX=36 StartY=-277 StartZ=0 EndX=-36 EndY=-277 EndZ=0
  constraints (12):
    c: Vertical(g0)
    c: Coincident(g1,g0)
    c: Horizontal(g1)
    c: Coincident(g2,g1)
    c: Vertical(g2)
    c: Coincident(g3,g2)
    c: Coincident(g3,g0)
    c: Horizontal(g3)
    c: DistanceX(g0) = -36
    c: DistanceX(g1) = 36
    c: DistanceY(g0) = -327
    c: DistanceY(g0,g0) = 50
FEATURE [Sketcher::SketchObject] Sketch018  label="outer007"
  FullyConstrained = true
  Placement = pos=(0,0,-281.2) rot=(0,0,1;0rad)
  sketch-geometry (4):
    g0: LineSegment StartX=-65 StartY=-252 StartZ=0 EndX=-65 EndY=-352 EndZ=0
    g1: LineSegment StartX=-65 StartY=-352 StartZ=0 EndX=65 EndY=-352 EndZ=0
    g2: LineSegment StartX=65 StartY=-352 StartZ=0 EndX=65 EndY=-252 EndZ=0
    g3: LineSegment StartX=65 StartY=-252 StartZ=0 EndX=-65 EndY=-252 EndZ=0
  constraints (12):
    c: Vertical(g0)
    c: Coincident(g1,g0)
    c: Horizontal(g1)
    c: Coincident(g2,g1)
    c: Vertical(g2)
    c: Coincident(g3,g2)
    c: Coincident(g3,g0)
    c: Horizontal(g3)
    c: DistanceX(g0) = -65
    c: DistanceX(g1) = 65
    c: DistanceY(g0) = -352
    c: DistanceY(g0,g0) = 100
FEATURE [Part::Loft] Loft007
  Closed = false
  MaxDegree = 5
  Ruled = false
  Sections = -> [Sketch017,Sketch018]
  Solid = true
FEATURE [Part::Fillet] Fillet015
  Base = -> Loft007
  Edges = 12 edges r=3: [Edge1,Edge2,Edge3,Edge4,Edge5,Edge6,Edge7,Edge8,Edge9,Edge10,Edge11,Edge12]
  Placement = pos=(0,0,-4) rot=(0,0,1;0rad)
FEATURE [Part::Cut] Cut006  label="sls004"
  Base = -> Fillet014
  Placement = pos=(0,0,-48) rot=(0,0,1;0rad)
  Tool = -> Fillet015
FEATURE [Part::Feature] Part__Feature153  label="logoTopCut"
  Placement = pos=(-30.8,-333,-323.9) rot=(0,0,1;0rad)
  shape: bbox 22.79 x 8 x 17.08 mm, 886 faces (baked)
FEATURE [Mesh::Feature] mintsLogo80P___90CutBase  label="mintsLogo80P - 90CutBase"
  Placement = pos=(0.5,-323,-309) rot=(1,0,0;1.5708rad)
FEATURE [Sketcher::SketchObject] Sketch019
  FullyConstrained = true
  Placement = pos=(0,0,0) rot=(1,0,0;1.5708rad)
  sketch-geometry (12):
    g0: LineSegment StartX=28 StartY=-324 StartZ=0 EndX=28 EndY=-316 EndZ=0
    g1: LineSegment StartX=28 StartY=-316 StartZ=0 EndX=-8 EndY=-316 EndZ=0
    g2: LineSegment StartX=-19 StartY=-316 StartZ=0 EndX=-34 EndY=-316 EndZ=0
    g3: LineSegment StartX=-34 StartY=-316 StartZ=0 EndX=-34 EndY=-324 EndZ=0
    g4: LineSegment StartX=-34 StartY=-324 StartZ=0 EndX=28 EndY=-324 EndZ=0
    g5: LineSegment StartX=-19 StartY=-316 StartZ=0 EndX=-19 EndY=-278 EndZ=0
    g6: LineSegment StartX=-19 StartY=-278 StartZ=0 EndX=-8 EndY=-278 EndZ=0
    g7: LineSegment StartX=-8 StartY=-278 StartZ=0 EndX=-8 EndY=-316 EndZ=0
    g8: Circle CenterX=-29.8 CenterY=-320.46 CenterZ=0 NormalX=0 NormalY=0 NormalZ=1 AngleXU=0 Radius=1.125
    g9: Circle CenterX=-13.58 CenterY=-288.46 CenterZ=0 NormalX=0 NormalY=0 NormalZ=1 AngleXU=0 Radius=1.125
    g10: Circle CenterX=-0.15 CenterY=-319.37 CenterZ=0 NormalX=0 NormalY=0 NormalZ=1 AngleXU=0 Radius=1.625
    g11: Circle CenterX=20.15 CenterY=-319.37 CenterZ=0 NormalX=0 NormalY=0 NormalZ=1 AngleXU=0 Radius=1.625
  constraints (36):
    c: Vertical(g0)
    c: Horizontal(g1)
    c: Horizontal(g2)
    c: Coincident(g3,g2)
    c: Vertical(g3)
    c: Coincident(g4,g3)
    c: Coincident(g4,g0)
    c: Horizontal(g4)
    c: DistanceX(g0) = 28
    c: DistanceY(g3) = -324
    c: Coincident(g0,g1)
    c: DistanceX(g1) = -8
    c: DistanceY(g3,g2) = 8
    c: DistanceX(g2,g2) = 15
    c: Coincident(g5,g2)
    c: Vertical(g5)
    c: Coincident(g6,g5)
    c: Horizontal(g6)
    c: Coincident(g7,g6)
    c: Coincident(g7,g1)
    c: Vertical(g7)
    c: DistanceY(g3,g5) = 46
    c: DistanceX(g3) = -34
    c: DistanceY(g2,g1) = 0
    c: Equal(g8,g9)
    c: Diameter(g8) = 2.25
    c: Equal(g11,g10)
    c: Diameter(g11) = 3.25
    c: DistanceX(g8) = -29.8
    c: DistanceY(g8) = -320.46
    c: DistanceY(g8,g9) = 32
    c: DistanceX(g8,g9) = 16.22
    c: DistanceX(g3,g10) = 33.85
    c: DistanceY(g3,g10) = 4.63
    c: DistanceY(g10,g11) = 0
    c: DistanceX(g10,g11) = 20.3
FEATURE [Part::Extrusion] Extrude003  label="i2cHold"
  Base = -> Sketch019
  Dir = (0,-1,-3e-16)
  DirMode = 2
  FaceMakerClass = Part::FaceMakerBullseye
  LengthFwd = 5
  LengthRev = 0
  Placement = pos=(0,-312,0) rot=(0,0,1;0rad)
  Solid = true
  Symmetric = false
FEATURE [Sketcher::SketchObject] Sketch020
  FullyConstrained = true
  sketch-geometry (6):
    g0: LineSegment StartX=-19 StartY=-295 StartZ=0 EndX=-8 EndY=-295 EndZ=0
    g1: LineSegment StartX=-19 StartY=-295 StartZ=0 EndX=-19 EndY=-325 EndZ=0
    g2: LineSegment StartX=-19 StartY=-325 StartZ=0 EndX=-8 EndY=-325 EndZ=0
    g3: LineSegment StartX=-8 StartY=-325 StartZ=0 EndX=-8 EndY=-295 EndZ=0
    g4: Circle CenterX=-13.45 CenterY=-300.1 CenterZ=0 NormalX=0 NormalY=0 NormalZ=1 AngleXU=0 Radius=1.625
    g5: Circle CenterX=-13.45 CenterY=-320.5 CenterZ=0 NormalX=0 NormalY=0 NormalZ=1 AngleXU=0 Radius=1.625
  constraints (18):
    c: Horizontal(g0)
    c: Coincident(g1,g0)
    c: Vertical(g1)
    c: Coincident(g2,g1)
    c: Horizontal(g2)
    c: Coincident(g3,g2)
    c: Coincident(g3,g0)
    c: Vertical(g3)
    c: DistanceX(g1) = -19
    c: DistanceY(g1) = -325
    c: DistanceX(g1,g2) = 11
    c: DistanceY(g1,g0) = 30
    c: Equal(g5,g4)
    c: Diameter(g5) = 3.25
    c: DistanceX(g5) = -13.45
    c: DistanceY(g5) = -320.5
    c: DistanceY(g5,g4) = 20.4
    c: DistanceX(g5,g4) = 0
FEATURE [Part::Extrusion] Extrude004  label="gpsHold"
  Base = -> Sketch020
  Dir = (0,0,1)
  DirMode = 2
  FaceMakerClass = Part::FaceMakerBullseye
  LengthFwd = 5
  LengthRev = 0
  Placement = pos=(0,0,-278) rot=(0,0,1;0rad)
  Solid = true
  Symmetric = false
FEATURE [Sketcher::SketchObject] Sketch021
  FullyConstrained = true
  MapMode = 3
  Placement = pos=(0,-312,0) rot=(1,0,0;1.5708rad)
  Support = -> [Extrude003]
  sketch-geometry (8):
    g0: LineSegment StartX=-25 StartY=-324 StartZ=0 EndX=-25 EndY=-316 EndZ=0
    g1: LineSegment StartX=-25 StartY=-316 StartZ=0 EndX=16.5 EndY=-316 EndZ=0
    g2: LineSegment StartX=16.5 StartY=-316 StartZ=0 EndX=16.5 EndY=-278 EndZ=0
    g3: LineSegment StartX=16.5 StartY=-278 StartZ=0 EndX=24.5 EndY=-278 EndZ=0
    g4: LineSegment StartX=24.5 StartY=-278 StartZ=0 EndX=24.5 EndY=-324 EndZ=0
    g5: LineSegment StartX=-25 StartY=-324 StartZ=0 EndX=24.5 EndY=-324 EndZ=0
    g6: Circle CenterX=-20.4 CenterY=-319.4 CenterZ=0 NormalX=0 NormalY=0 NormalZ=1 AngleXU=0 Radius=1.125
    g7: Circle CenterX=20.4 CenterY=-282.6 CenterZ=0 NormalX=0 NormalY=0 NormalZ=1 AngleXU=0 Radius=1.125
  constraints (24):
    c: Vertical(g0)
    c: Coincident(g1,g0)
    c: Horizontal(g1)
    c: Coincident(g2,g1)
    c: Vertical(g2)
    c: Coincident(g3,g2)
    c: Horizontal(g3)
    c: Coincident(g4,g3)
    c: Vertical(g4)
    c: Coincident(g5,g0)
    c: Coincident(g5,g4)
    c: Horizontal(g5)
    c: DistanceX(g0) = -25
    c: DistanceY(g0) = -324
    c: DistanceY(g0,g0) = 8
    c: DistanceX(g0,g1) = 41.5
    c: DistanceX(g1,g3) = 8
    c: DistanceY(g1,g2) = 38
    c: Equal(g7,g6)
    c: Diameter(g7) = 2.25
    c: DistanceX(g0,g6) = 4.6
    c: DistanceX(g6,g7) = 40.8
    c: DistanceY(g6,g7) = 36.8
    c: DistanceY(g0,g6) = 4.6
FEATURE [Part::Extrusion] Extrude005  label="ipsHold"
  Base = -> Sketch021
  Dir = (0,-1,2e-16)
  DirMode = 2
  FaceMakerClass = Part::FaceMakerBullseye
  LengthFwd = 5
  LengthRev = 0
  Placement = pos=(0,32,0) rot=(0,0,1;0rad)
  Solid = true
  Symmetric = false
FEATURE [Sketcher::SketchObject] Sketch022
  FullyConstrained = true
  MapMode = 45
  Placement = pos=(4.42608e-08,-302,-283.455) rot=(0,0,1;1.5708rad)
  Support = -> [Cut005,Cut,Cut004]
  sketch-geometry (4):
    g0: LineSegment StartX=36 StartY=49 StartZ=0 EndX=-36 EndY=49 EndZ=0
    g1: LineSegment StartX=-36 StartY=49 StartZ=0 EndX=-36 EndY=-49 EndZ=0
    g2: LineSegment StartX=-36 StartY=-49 StartZ=0 EndX=36 EndY=-49 EndZ=0
    g3: LineSegment StartX=36 StartY=-49 StartZ=0 EndX=36 EndY=49 EndZ=0
  constraints (12):
    c: Horizontal(g0)
    c: Coincident(g1,g0)
    c: Vertical(g1)
    c: Coincident(g2,g1)
    c: Horizontal(g2)
    c: Coincident(g3,g0)
    c: Vertical(g3)
    c: DistanceX(g0) = -36
    c: DistanceY(g0) = 49
    c: DistanceX(g0) = 36
    c: DistanceY(g1) = -49
    c: Coincident(g2,g3)
FEATURE [Part::Extrusion] Extrude006  label="base"
  Base = -> Sketch022
  Dir = (6.08852e-10,-8.7778e-10,1)
  DirMode = 2
  FaceMakerClass = Part::FaceMakerBullseye
  LengthFwd = 4.5
  LengthRev = 0
  Placement = pos=(0,0,-44.75) rot=(0,0,1;0rad)
  Solid = true
  Symmetric = false
FEATURE [Sketcher::SketchObject] Sketch023
  FullyConstrained = true
  sketch-geometry (4):
    g0: Circle CenterX=-42 CenterY=-332 CenterZ=0 NormalX=0 NormalY=0 NormalZ=1 AngleXU=0 Radius=5.5
    g1: Circle CenterX=42 CenterY=-332 CenterZ=0 NormalX=0 NormalY=0 NormalZ=1 AngleXU=0 Radius=5.5
    g2: Circle CenterX=42 CenterY=-272 CenterZ=0 NormalX=0 NormalY=0 NormalZ=1 AngleXU=0 Radius=5.5
    g3: Circle CenterX=-42 CenterY=-272 CenterZ=0 NormalX=0 NormalY=0 NormalZ=1 AngleXU=0 Radius=5.5
  constraints (12):
    c: DistanceX(g0) = -42
    c: DistanceY(g0) = -332
    c: Equal(g0,g3)
    c: Equal(g0,g2)
    c: Equal(g0,g1)
    c: Diameter(g0) = 11
    c: DistanceX(g3,g0) = 0
    c: DistanceY(g0,g3) = 60
    c: DistanceY(g2,g3) = 0
    c: DistanceX(g0,g1) = 84
    c: DistanceY(g0,g1) = 0
    c: DistanceX(g2,g1) = 0
FEATURE [Part::Extrusion] Extrude007  label="stands"
  Base = -> Sketch023
  Dir = (0,0,1)
  DirMode = 2
  FaceMakerClass = Part::FaceMakerBullseye
  LengthFwd = 69
  LengthRev = 0
  Placement = pos=(0,0,-323) rot=(0,0,1;0rad)
  Solid = true
  Symmetric = false
FEATURE [Sketcher::SketchObject] Sketch024  label="inner008"
  FullyConstrained = true
  Placement = pos=(0,0,-259.26) rot=(0,0,1;0rad)
  sketch-geometry (4):
    g0: LineSegment StartX=-36 StartY=-277 StartZ=0 EndX=-36 EndY=-327 EndZ=0
    g1: LineSegment StartX=-36 StartY=-327 StartZ=0 EndX=36 EndY=-327 EndZ=0
    g2: LineSegment StartX=36 StartY=-327 StartZ=0 EndX=36 EndY=-277 EndZ=0
    g3: LineSegment StartX=36 StartY=-277 StartZ=0 EndX=-36 EndY=-277 EndZ=0
  constraints (12):
    c: Vertical(g0)
    c: Coincident(g1,g0)
    c: Horizontal(g1)
    c: Coincident(g2,g1)
    c: Vertical(g2)
    c: Coincident(g3,g2)
    c: Coincident(g3,g0)
    c: Horizontal(g3)
    c: DistanceX(g0) = -36
    c: DistanceX(g1) = 36
    c: DistanceY(g0) = -327
    c: DistanceY(g0,g0) = 50
FEATURE [Sketcher::SketchObject] Sketch025  label="outer008"
  FullyConstrained = true
  Placement = pos=(0,0,-281.2) rot=(0,0,1;0rad)
  sketch-geometry (4):
    g0: LineSegment StartX=-65 StartY=-252 StartZ=0 EndX=-65 EndY=-352 EndZ=0
    g1: LineSegment StartX=-65 StartY=-352 StartZ=0 EndX=65 EndY=-352 EndZ=0
    g2: LineSegment StartX=65 StartY=-352 StartZ=0 EndX=65 EndY=-252 EndZ=0
    g3: LineSegment StartX=65 StartY=-252 StartZ=0 EndX=-65 EndY=-252 EndZ=0
  constraints (12):
    c: Vertical(g0)
    c: Coincident(g1,g0)
    c: Horizontal(g1)
    c: Coincident(g2,g1)
    c: Vertical(g2)
    c: Coincident(g3,g2)
    c: Coincident(g3,g0)
    c: Horizontal(g3)
    c: DistanceX(g0) = -65
    c: DistanceX(g1) = 65
    c: DistanceY(g0) = -352
    c: DistanceY(g0,g0) = 100
FEATURE [Part::Loft] Loft008
  Closed = false
  MaxDegree = 5
  Ruled = false
  Sections = -> [Sketch024,Sketch025]
  Solid = true
FEATURE [Part::Fillet] Fillet016
  Base = -> Loft008
  Edges = 12 edges r=3: [Edge1,Edge2,Edge3,Edge4,Edge5,Edge6,Edge7,Edge8,Edge9,Edge10,Edge11,Edge12]
FEATURE [Sketcher::SketchObject] Sketch026  label="inner009"
  FullyConstrained = true
  Placement = pos=(0,0,-259.26) rot=(0,0,1;0rad)
  sketch-geometry (4):
    g0: LineSegment StartX=-36 StartY=-277 StartZ=0 EndX=-36 EndY=-327 EndZ=0
    g1: LineSegment StartX=-36 StartY=-327 StartZ=0 EndX=36 EndY=-327 EndZ=0
    g2: LineSegment StartX=36 StartY=-327 StartZ=0 EndX=36 EndY=-277 EndZ=0
    g3: LineSegment StartX=36 StartY=-277 StartZ=0 EndX=-36 EndY=-277 EndZ=0
  constraints (12):
    c: Vertical(g0)
    c: Coincident(g1,g0)
    c: Horizontal(g1)
    c: Coincident(g2,g1)
    c: Vertical(g2)
    c: Coincident(g3,g2)
    c: Coincident(g3,g0)
    c: Horizontal(g3)
    c: DistanceX(g0) = -36
    c: DistanceX(g1) = 36
    c: DistanceY(g0) = -327
    c: DistanceY(g0,g0) = 50
FEATURE [Sketcher::SketchObject] Sketch027  label="outer009"
  FullyConstrained = true
  Placement = pos=(0,0,-281.2) rot=(0,0,1;0rad)
  sketch-geometry (4):
    g0: LineSegment StartX=-65 StartY=-252 StartZ=0 EndX=-65 EndY=-352 EndZ=0
    g1: LineSegment StartX=-65 StartY=-352 StartZ=0 EndX=65 EndY=-352 EndZ=0
    g2: LineSegment StartX=65 StartY=-352 StartZ=0 EndX=65 EndY=-252 EndZ=0
    g3: LineSegment StartX=65 StartY=-252 StartZ=0 EndX=-65 EndY=-252 EndZ=0
  constraints (12):
    c: Vertical(g0)
    c: Coincident(g1,g0)
    c: Horizontal(g1)
    c: Coincident(g2,g1)
    c: Vertical(g2)
    c: Coincident(g3,g2)
    c: Coincident(g3,g0)
    c: Horizontal(g3)
    c: DistanceX(g0) = -65
    c: DistanceX(g1) = 65
    c: DistanceY(g0) = -352
    c: DistanceY(g0,g0) = 100
FEATURE [Part::Loft] Loft009
  Closed = false
  MaxDegree = 5
  Ruled = false
  Sections = -> [Sketch026,Sketch027]
  Solid = true
FEATURE [Part::Fillet] Fillet017
  Base = -> Loft009
  Edges = 12 edges r=3: [Edge1,Edge2,Edge3,Edge4,Edge5,Edge6,Edge7,Edge8,Edge9,Edge10,Edge11,Edge12]
  Placement = pos=(0,0,-4) rot=(0,0,1;0rad)
FEATURE [Part::Cut] Cut007  label="sls005"
  Base = -> Fillet016
  Placement = pos=(0,0,4) rot=(0,0,1;0rad)
  Tool = -> Fillet017
FEATURE [Sketcher::SketchObject] Sketch028  label="inner010"
  FullyConstrained = true
  Placement = pos=(0,0,-259.26) rot=(0,0,1;0rad)
  sketch-geometry (4):
    g0: LineSegment StartX=-36 StartY=-277 StartZ=0 EndX=-36 EndY=-327 EndZ=0
    g1: LineSegment StartX=-36 StartY=-327 StartZ=0 EndX=36 EndY=-327 EndZ=0
    g2: LineSegment StartX=36 StartY=-327 StartZ=0 EndX=36 EndY=-277 EndZ=0
    g3: LineSegment StartX=36 StartY=-277 StartZ=0 EndX=-36 EndY=-277 EndZ=0
  constraints (12):
    c: Vertical(g0)
    c: Coincident(g1,g0)
    c: Horizontal(g1)
    c: Coincident(g2,g1)
    c: Vertical(g2)
    c: Coincident(g3,g2)
    c: Coincident(g3,g0)
    c: Horizontal(g3)
    c: DistanceX(g0) = -36
    c: DistanceX(g1) = 36
    c: DistanceY(g0) = -327
    c: DistanceY(g0,g0) = 50
FEATURE [Sketcher::SketchObject] Sketch029  label="outer010"
  FullyConstrained = true
  Placement = pos=(0,0,-281.2) rot=(0,0,1;0rad)
  sketch-geometry (4):
    g0: LineSegment StartX=-65 StartY=-252 StartZ=0 EndX=-65 EndY=-352 EndZ=0
    g1: LineSegment StartX=-65 StartY=-352 StartZ=0 EndX=65 EndY=-352 EndZ=0
    g2: LineSegment StartX=65 StartY=-352 StartZ=0 EndX=65 EndY=-252 EndZ=0
    g3: LineSegment StartX=65 StartY=-252 StartZ=0 EndX=-65 EndY=-252 EndZ=0
  constraints (12):
    c: Vertical(g0)
    c: Coincident(g1,g0)
    c: Horizontal(g1)
    c: Coincident(g2,g1)
    c: Vertical(g2)
    c: Coincident(g3,g2)
    c: Coincident(g3,g0)
    c: Horizontal(g3)
    c: DistanceX(g0) = -65
    c: DistanceX(g1) = 65
    c: DistanceY(g0) = -352
    c: DistanceY(g0,g0) = 100
FEATURE [Part::Loft] Loft010
  Closed = false
  MaxDegree = 5
  Ruled = false
  Sections = -> [Sketch028,Sketch029]
  Solid = true
FEATURE [Part::Fillet] Fillet018
  Base = -> Loft010
  Edges = 12 edges r=3: [Edge1,Edge2,Edge3,Edge4,Edge5,Edge6,Edge7,Edge8,Edge9,Edge10,Edge11,Edge12]
FEATURE [Sketcher::SketchObject] Sketch030  label="inner011"
  FullyConstrained = true
  Placement = pos=(0,0,-259.26) rot=(0,0,1;0rad)
  sketch-geometry (4):
    g0: LineSegment StartX=-36 StartY=-277 StartZ=0 EndX=-36 EndY=-327 EndZ=0
    g1: LineSegment StartX=-36 StartY=-327 StartZ=0 EndX=36 EndY=-327 EndZ=0
    g2: LineSegment StartX=36 StartY=-327 StartZ=0 EndX=36 EndY=-277 EndZ=0
    g3: LineSegment StartX=36 StartY=-277 StartZ=0 EndX=-36 EndY=-277 EndZ=0
  constraints (12):
    c: Vertical(g0)
    c: Coincident(g1,g0)
    c: Horizontal(g1)
    c: Coincident(g2,g1)
    c: Vertical(g2)
    c: Coincident(g3,g2)
    c: Coincident(g3,g0)
    c: Horizontal(g3)
    c: DistanceX(g0) = -36
    c: DistanceX(g1) = 36
    c: DistanceY(g0) = -327
    c: DistanceY(g0,g0) = 50
FEATURE [Sketcher::SketchObject] Sketch031  label="outer011"
  FullyConstrained = true
  Placement = pos=(0,0,-281.2) rot=(0,0,1;0rad)
  sketch-geometry (4):
    g0: LineSegment StartX=-65 StartY=-252 StartZ=0 EndX=-65 EndY=-352 EndZ=0
    g1: LineSegment StartX=-65 StartY=-352 StartZ=0 EndX=65 EndY=-352 EndZ=0
    g2: LineSegment StartX=65 StartY=-352 StartZ=0 EndX=65 EndY=-252 EndZ=0
    g3: LineSegment StartX=65 StartY=-252 StartZ=0 EndX=-65 EndY=-252 EndZ=0
  constraints (12):
    c: Vertical(g0)
    c: Coincident(g1,g0)
    c: Horizontal(g1)
    c: Coincident(g2,g1)
    c: Vertical(g2)
    c: Coincident(g3,g2)
    c: Coincident(g3,g0)
    c: Horizontal(g3)
    c: DistanceX(g0) = -65
    c: DistanceX(g1) = 65
    c: DistanceY(g0) = -352
    c: DistanceY(g0,g0) = 100
FEATURE [Part::Loft] Loft011
  Closed = false
  MaxDegree = 5
  Ruled = false
  Sections = -> [Sketch030,Sketch031]
  Solid = true
FEATURE [Part::Fillet] Fillet019
  Base = -> Loft011
  Edges = 12 edges r=3: [Edge1,Edge2,Edge3,Edge4,Edge5,Edge6,Edge7,Edge8,Edge9,Edge10,Edge11,Edge12]
  Placement = pos=(0,0,-4) rot=(0,0,1;0rad)
FEATURE [Part::Cut] Cut008  label="sls006"
  Base = -> Fillet018
  Placement = pos=(0,0,7) rot=(0,0,1;0rad)
  Tool = -> Fillet019
FEATURE [Sketcher::SketchObject] Sketch033
  FullyConstrained = true
  Placement = pos=(0,0,0) rot=(1,0,0;1.5708rad)
  sketch-geometry (4):
    g0: LineSegment StartX=-22 StartY=-275.2 StartZ=0 EndX=22 EndY=-275.2 EndZ=0
    g1: LineSegment StartX=22 StartY=-275.2 StartZ=0 EndX=22 EndY=-323.5 EndZ=0
    g2: LineSegment StartX=22 StartY=-323.5 StartZ=0 EndX=-22 EndY=-323.5 EndZ=0
    g3: LineSegment StartX=-22 StartY=-323.5 StartZ=0 EndX=-22 EndY=-275.2 EndZ=0
  constraints (12):
    c: Coincident(g0,g1)
    c: Coincident(g1,g2)
    c: Coincident(g2,g3)
    c: Coincident(g3,g0)
    c: Horizontal(g0)
    c: Horizontal(g2)
    c: Vertical(g1)
    c: Vertical(g3)
    c: DistanceX(g1) = 22
    c: DistanceX(g0) = -22
    c: DistanceY(g0) = -275.2
    c: DistanceY(g2) = -323.5
FEATURE [Part::Extrusion] Extrude009  label="face"
  Base = -> Sketch033
  Dir = (0,-1,2e-16)
  DirMode = 2
  FaceMakerClass = Part::FaceMakerBullseye
  LengthFwd = 2
  LengthRev = 0
  Placement = pos=(0,-325.87,0) rot=(0,0,1;0rad)
  Solid = true
  Symmetric = false
FEATURE [Sketcher::SketchObject] Sketch034
  FullyConstrained = true
  sketch-geometry (4):
    g0: Circle CenterX=-42 CenterY=-332 CenterZ=0 NormalX=0 NormalY=0 NormalZ=1 AngleXU=0 Radius=2
    g1: Circle CenterX=42 CenterY=-332 CenterZ=0 NormalX=0 NormalY=0 NormalZ=1 AngleXU=0 Radius=2
    g2: Circle CenterX=42 CenterY=-272 CenterZ=0 NormalX=0 NormalY=0 NormalZ=1 AngleXU=0 Radius=2
    g3: Circle CenterX=-42 CenterY=-272 CenterZ=0 NormalX=0 NormalY=0 NormalZ=1 AngleXU=0 Radius=2
  constraints (12):
    c: DistanceX(g0) = -42
    c: DistanceY(g0) = -332
    c: Equal(g0,g3)
    c: Equal(g0,g2)
    c: Equal(g0,g1)
    c: Diameter(g0) = 4
    c: DistanceX(g3,g0) = 0
    c: DistanceY(g0,g3) = 60
    c: DistanceY(g2,g3) = 0
    c: DistanceX(g0,g1) = 84
    c: DistanceY(g0,g1) = 0
    c: DistanceX(g2,g1) = 0
FEATURE [Part::Extrusion] Extrude010  label="slsCuts"
  Base = -> Sketch034
  Dir = (0,0,1)
  DirMode = 2
  FaceMakerClass = Part::FaceMakerBullseye
  LengthFwd = 20
  LengthRev = 0
  Placement = pos=(0,0,-323) rot=(0,0,1;0rad)
  Solid = true
  Symmetric = false
FEATURE [Sketcher::SketchObject] Sketch035
  FullyConstrained = true
  sketch-geometry (4):
    g0: Circle CenterX=-42 CenterY=-332 CenterZ=0 NormalX=0 NormalY=0 NormalZ=1 AngleXU=0 Radius=1.625
    g1: Circle CenterX=42 CenterY=-332 CenterZ=0 NormalX=0 NormalY=0 NormalZ=1 AngleXU=0 Radius=1.625
    g2: Circle CenterX=42 CenterY=-272 CenterZ=0 NormalX=0 NormalY=0 NormalZ=1 AngleXU=0 Radius=1.625
    g3: Circle CenterX=-42 CenterY=-272 CenterZ=0 NormalX=0 NormalY=0 NormalZ=1 AngleXU=0 Radius=1.625
  constraints (12):
    c: DistanceX(g0) = -42
    c: DistanceY(g0) = -332
    c: Equal(g0,g3)
    c: Equal(g0,g2)
    c: Equal(g0,g1)
    c: Diameter(g0) = 3.25
    c: DistanceX(g3,g0) = 0
    c: DistanceY(g0,g3) = 60
    c: DistanceY(g2,g3) = 0
    c: DistanceX(g0,g1) = 84
    c: DistanceY(g0,g1) = 0
    c: DistanceX(g2,g1) = 0
FEATURE [Part::Extrusion] Extrude011  label="baseCuts001"
  Base = -> Sketch035
  Dir = (0,0,1)
  DirMode = 2
  FaceMakerClass = Part::FaceMakerBullseye
  LengthFwd = 20
  LengthRev = 0
  Placement = pos=(0,0,-329) rot=(0,0,1;0rad)
  Solid = true
  Symmetric = false
FEATURE [Part::MultiFuse] Fusion036  label="slsBottom"
  Shapes = -> [Cut006,Cut005]
FEATURE [Sketcher::SketchObject] Sketch036
  FullyConstrained = true
  MapMode = 2
  sketch-geometry (4):
    g0: LineSegment StartX=-28 StartY=-347.85 StartZ=0 EndX=28 EndY=-347.85 EndZ=0
    g1: LineSegment StartX=18 StartY=-327.85 StartZ=0 EndX=28 EndY=-347.85 EndZ=0
    g2: LineSegment StartX=-28 StartY=-347.85 StartZ=0 EndX=-18 EndY=-327.85 EndZ=0
    g3: LineSegment StartX=-18 StartY=-327.85 StartZ=0 EndX=18 EndY=-327.85 EndZ=0
  constraints (12):
    c: Horizontal(g0)
    c: Coincident(g1,g0)
    c: Coincident(g2,g0)
    c: Coincident(g3,g2)
    c: Coincident(g3,g1)
    c: Horizontal(g3)
    c: DistanceX(g2) = -18
    c: DistanceX(g1) = 18
    c: DistanceX(g0,g2) = 10
    c: DistanceY(g2) = -327.85
    c: DistanceY(g0,g2) = 20
    c: DistanceX(g1,g0) = 10
FEATURE [Part::Extrusion] Extrude012
  Base = -> Sketch036
  Dir = (0,0,1)
  DirMode = 2
  FaceMakerClass = Part::FaceMakerBullseye
  LengthFwd = 40
  LengthRev = 0
  Placement = pos=(0,0,-329) rot=(0,0,1;0rad)
  Solid = true
  Symmetric = false
FEATURE [Part::Cut] Cut011  label="slsBottom001"
  Base = -> Fusion036
  Tool = -> Extrude012
FEATURE [Sketcher::SketchObject] Sketch037
  FullyConstrained = true
  sketch-geometry (4):
    g0: LineSegment StartX=-34.9 StartY=-278.2 StartZ=0 EndX=34.9 EndY=-278.2 EndZ=0
    g1: LineSegment StartX=34.9 StartY=-278.2 StartZ=0 EndX=34.9 EndY=-325.8 EndZ=0
    g2: LineSegment StartX=34.9 StartY=-325.8 StartZ=0 EndX=-34.9 EndY=-325.8 EndZ=0
    g3: LineSegment StartX=-34.9 StartY=-325.8 StartZ=0 EndX=-34.9 EndY=-278.2 EndZ=0
  constraints (12):
    c: Coincident(g0,g1)
    c: Coincident(g1,g2)
    c: Coincident(g2,g3)
    c: Coincident(g3,g0)
    c: Horizontal(g0)
    c: Horizontal(g2)
    c: Vertical(g1)
    c: Vertical(g3)
    c: DistanceX(g2) = -34.9
    c: DistanceX(g1) = 34.9
    c: DistanceY(g2) = -325.8
    c: DistanceY(g2,g0) = 47.6
FEATURE [Part::Extrusion] Extrude013  label="slsCut"
  Base = -> Sketch037
  Dir = (0,0,1)
  DirMode = 2
  FaceMakerClass = Part::FaceMakerBullseye
  LengthFwd = 60
  LengthRev = 0
  Placement = pos=(0,0,-329) rot=(0,0,1;0rad)
  Solid = true
  Symmetric = false
FEATURE [Part::MultiFuse] Fusion037  label="sls"
  Shapes = -> [Cut011,Extrude009,Extrude007,Cut004,Cut]
FEATURE [Part::MultiFuse] Fusion038  label="base001"
  Shapes = -> [Extrude005,Extrude004,Extrude006,Extrude003]
FEATURE [Part::Cut] Cut012  label="sls007"
  Base = -> Fusion037
  Tool = -> Extrude013
FEATURE [Sketcher::SketchObject] Sketch038  label="inner012"
  FullyConstrained = true
  Placement = pos=(0,0,-259.26) rot=(0,0,1;0rad)
  sketch-geometry (4):
    g0: LineSegment StartX=-36 StartY=-277 StartZ=0 EndX=-36 EndY=-327 EndZ=0
    g1: LineSegment StartX=-36 StartY=-327 StartZ=0 EndX=36 EndY=-327 EndZ=0
    g2: LineSegment StartX=36 StartY=-327 StartZ=0 EndX=36 EndY=-277 EndZ=0
    g3: LineSegment StartX=36 StartY=-277 StartZ=0 EndX=-36 EndY=-277 EndZ=0
  constraints (12):
    c: Vertical(g0)
    c: Coincident(g1,g0)
    c: Horizontal(g1)
    c: Coincident(g2,g1)
    c: Vertical(g2)
    c: Coincident(g3,g2)
    c: Coincident(g3,g0)
    c: Horizontal(g3)
    c: DistanceX(g0) = -36
    c: DistanceX(g1) = 36
    c: DistanceY(g0) = -327
    c: DistanceY(g0,g0) = 50
FEATURE [Sketcher::SketchObject] Sketch039  label="outer012"
  FullyConstrained = true
  Placement = pos=(0,0,-281.2) rot=(0,0,1;0rad)
  sketch-geometry (4):
    g0: LineSegment StartX=-65 StartY=-252 StartZ=0 EndX=-65 EndY=-352 EndZ=0
    g1: LineSegment StartX=-65 StartY=-352 StartZ=0 EndX=65 EndY=-352 EndZ=0
    g2: LineSegment StartX=65 StartY=-352 StartZ=0 EndX=65 EndY=-252 EndZ=0
    g3: LineSegment StartX=65 StartY=-252 StartZ=0 EndX=-65 EndY=-252 EndZ=0
  constraints (12):
    c: Vertical(g0)
    c: Coincident(g1,g0)
    c: Horizontal(g1)
    c: Coincident(g2,g1)
    c: Vertical(g2)
    c: Coincident(g3,g2)
    c: Coincident(g3,g0)
    c: Horizontal(g3)
    c: DistanceX(g0) = -65
    c: DistanceX(g1) = 65
    c: DistanceY(g0) = -352
    c: DistanceY(g0,g0) = 100
FEATURE [Part::Loft] Loft012
  Closed = false
  MaxDegree = 5
  Ruled = false
  Sections = -> [Sketch038,Sketch039]
  Solid = true
FEATURE [Part::Fillet] Fillet020
  Base = -> Loft012
  Edges = 12 edges r=3: [Edge1,Edge2,Edge3,Edge4,Edge5,Edge6,Edge7,Edge8,Edge9,Edge10,Edge11,Edge12]
FEATURE [Sketcher::SketchObject] Sketch040  label="inner013"
  FullyConstrained = true
  Placement = pos=(0,0,-259.26) rot=(0,0,1;0rad)
  sketch-geometry (4):
    g0: LineSegment StartX=-36 StartY=-277 StartZ=0 EndX=-36 EndY=-327 EndZ=0
    g1: LineSegment StartX=-36 StartY=-327 StartZ=0 EndX=36 EndY=-327 EndZ=0
    g2: LineSegment StartX=36 StartY=-327 StartZ=0 EndX=36 EndY=-277 EndZ=0
    g3: LineSegment StartX=36 StartY=-277 StartZ=0 EndX=-36 EndY=-277 EndZ=0
  constraints (12):
    c: Vertical(g0)
    c: Coincident(g1,g0)
    c: Horizontal(g1)
    c: Coincident(g2,g1)
    c: Vertical(g2)
    c: Coincident(g3,g2)
    c: Coincident(g3,g0)
    c: Horizontal(g3)
    c: DistanceX(g0) = -36
    c: DistanceX(g1) = 36
    c: DistanceY(g0) = -327
    c: DistanceY(g0,g0) = 50
FEATURE [Sketcher::SketchObject] Sketch041  label="outer013"
  FullyConstrained = true
  Placement = pos=(0,0,-281.2) rot=(0,0,1;0rad)
  sketch-geometry (4):
    g0: LineSegment StartX=-65 StartY=-252 StartZ=0 EndX=-65 EndY=-352 EndZ=0
    g1: LineSegment StartX=-65 StartY=-352 StartZ=0 EndX=65 EndY=-352 EndZ=0
    g2: LineSegment StartX=65 StartY=-352 StartZ=0 EndX=65 EndY=-252 EndZ=0
    g3: LineSegment StartX=65 StartY=-252 StartZ=0 EndX=-65 EndY=-252 EndZ=0
  constraints (12):
    c: Vertical(g0)
    c: Coincident(g1,g0)
    c: Horizontal(g1)
    c: Coincident(g2,g1)
    c: Vertical(g2)
    c: Coincident(g3,g2)
    c: Coincident(g3,g0)
    c: Horizontal(g3)
    c: DistanceX(g0) = -65
    c: DistanceX(g1) = 65
    c: DistanceY(g0) = -352
    c: DistanceY(g0,g0) = 100
FEATURE [Part::Loft] Loft013
  Closed = false
  MaxDegree = 5
  Ruled = false
  Sections = -> [Sketch040,Sketch041]
  Solid = true
FEATURE [Part::Fillet] Fillet021
  Base = -> Loft013
  Edges = 12 edges r=3: [Edge1,Edge2,Edge3,Edge4,Edge5,Edge6,Edge7,Edge8,Edge9,Edge10,Edge11,Edge12]
  Placement = pos=(0,0,-4) rot=(0,0,1;0rad)
FEATURE [Part::Cut] Cut013  label="sls008"
  Base = -> Fillet020
  Placement = pos=(0,0,10) rot=(0,0,1;0rad)
  Tool = -> Fillet021
FEATURE [Part::MultiFuse] Fusion039
  Shapes = -> [Cut013,Cut008,Cut007]
FEATURE [Sketcher::SketchObject] Sketch042  label="inner014"
  FullyConstrained = true
  Placement = pos=(0,0,-259.26) rot=(0,0,1;0rad)
  sketch-geometry (4):
    g0: LineSegment StartX=-36 StartY=-277 StartZ=0 EndX=-36 EndY=-327 EndZ=0
    g1: LineSegment StartX=-36 StartY=-327 StartZ=0 EndX=36 EndY=-327 EndZ=0
    g2: LineSegment StartX=36 StartY=-327 StartZ=0 EndX=36 EndY=-277 EndZ=0
    g3: LineSegment StartX=36 StartY=-277 StartZ=0 EndX=-36 EndY=-277 EndZ=0
  constraints (12):
    c: Vertical(g0)
    c: Coincident(g1,g0)
    c: Horizontal(g1)
    c: Coincident(g2,g1)
    c: Vertical(g2)
    c: Coincident(g3,g2)
    c: Coincident(g3,g0)
    c: Horizontal(g3)
    c: DistanceX(g0) = -36
    c: DistanceX(g1) = 36
    c: DistanceY(g0) = -327
    c: DistanceY(g0,g0) = 50
FEATURE [Sketcher::SketchObject] Sketch043  label="outer014"
  FullyConstrained = true
  Placement = pos=(0,0,-281.2) rot=(0,0,1;0rad)
  sketch-geometry (4):
    g0: LineSegment StartX=-65 StartY=-252 StartZ=0 EndX=-65 EndY=-352 EndZ=0
    g1: LineSegment StartX=-65 StartY=-352 StartZ=0 EndX=65 EndY=-352 EndZ=0
    g2: LineSegment StartX=65 StartY=-352 StartZ=0 EndX=65 EndY=-252 EndZ=0
    g3: LineSegment StartX=65 StartY=-252 StartZ=0 EndX=-65 EndY=-252 EndZ=0
  constraints (12):
    c: Vertical(g0)
    c: Coincident(g1,g0)
    c: Horizontal(g1)
    c: Coincident(g2,g1)
    c: Vertical(g2)
    c: Coincident(g3,g2)
    c: Coincident(g3,g0)
    c: Horizontal(g3)
    c: DistanceX(g0) = -65
    c: DistanceX(g1) = 65
    c: DistanceY(g0) = -352
    c: DistanceY(g0,g0) = 100
FEATURE [Part::Loft] Loft014
  Closed = false
  MaxDegree = 5
  Ruled = false
  Sections = -> [Sketch042,Sketch043]
  Solid = true
FEATURE [Part::Fillet] Fillet022
  Base = -> Loft014
  Edges = 12 edges r=3: [Edge1,Edge2,Edge3,Edge4,Edge5,Edge6,Edge7,Edge8,Edge9,Edge10,Edge11,Edge12]
FEATURE [Sketcher::SketchObject] Sketch044  label="inner015"
  FullyConstrained = true
  Placement = pos=(0,0,-259.26) rot=(0,0,1;0rad)
  sketch-geometry (4):
    g0: LineSegment StartX=-36 StartY=-277 StartZ=0 EndX=-36 EndY=-327 EndZ=0
    g1: LineSegment StartX=-36 StartY=-327 StartZ=0 EndX=36 EndY=-327 EndZ=0
    g2: LineSegment StartX=36 StartY=-327 StartZ=0 EndX=36 EndY=-277 EndZ=0
    g3: LineSegment StartX=36 StartY=-277 StartZ=0 EndX=-36 EndY=-277 EndZ=0
  constraints (12):
    c: Vertical(g0)
    c: Coincident(g1,g0)
    c: Horizontal(g1)
    c: Coincident(g2,g1)
    c: Vertical(g2)
    c: Coincident(g3,g2)
    c: Coincident(g3,g0)
    c: Horizontal(g3)
    c: DistanceX(g0) = -36
    c: DistanceX(g1) = 36
    c: DistanceY(g0) = -327
    c: DistanceY(g0,g0) = 50
FEATURE [Sketcher::SketchObject] Sketch045  label="outer015"
  FullyConstrained = true
  Placement = pos=(0,0,-281.2) rot=(0,0,1;0rad)
  sketch-geometry (4):
    g0: LineSegment StartX=-65 StartY=-252 StartZ=0 EndX=-65 EndY=-352 EndZ=0
    g1: LineSegment StartX=-65 StartY=-352 StartZ=0 EndX=65 EndY=-352 EndZ=0
    g2: LineSegment StartX=65 StartY=-352 StartZ=0 EndX=65 EndY=-252 EndZ=0
    g3: LineSegment StartX=65 StartY=-252 StartZ=0 EndX=-65 EndY=-252 EndZ=0
  constraints (12):
    c: Vertical(g0)
    c: Coincident(g1,g0)
    c: Horizontal(g1)
    c: Coincident(g2,g1)
    c: Vertical(g2)
    c: Coincident(g3,g2)
    c: Coincident(g3,g0)
    c: Horizontal(g3)
    c: DistanceX(g0) = -65
    c: DistanceX(g1) = 65
    c: DistanceY(g0) = -352
    c: DistanceY(g0,g0) = 100
FEATURE [Part::Loft] Loft015
  Closed = false
  MaxDegree = 5
  Ruled = false
  Sections = -> [Sketch044,Sketch045]
  Solid = true
FEATURE [Part::Fillet] Fillet023
  Base = -> Loft015
  Edges = 12 edges r=3: [Edge1,Edge2,Edge3,Edge4,Edge5,Edge6,Edge7,Edge8,Edge9,Edge10,Edge11,Edge12]
  Placement = pos=(0,0,-4) rot=(0,0,1;0rad)
FEATURE [Part::Cut] Cut014  label="sls009"
  Base = -> Fillet022
  Placement = pos=(0,0,4) rot=(0,0,1;0rad)
  Tool = -> Fillet023
FEATURE [Sketcher::SketchObject] Sketch046  label="inner016"
  FullyConstrained = true
  Placement = pos=(0,0,-259.26) rot=(0,0,1;0rad)
  sketch-geometry (4):
    g0: LineSegment StartX=-36 StartY=-277 StartZ=0 EndX=-36 EndY=-327 EndZ=0
    g1: LineSegment StartX=-36 StartY=-327 StartZ=0 EndX=36 EndY=-327 EndZ=0
    g2: LineSegment StartX=36 StartY=-327 StartZ=0 EndX=36 EndY=-277 EndZ=0
    g3: LineSegment StartX=36 StartY=-277 StartZ=0 EndX=-36 EndY=-277 EndZ=0
  constraints (12):
    c: Vertical(g0)
    c: Coincident(g1,g0)
    c: Horizontal(g1)
    c: Coincident(g2,g1)
    c: Vertical(g2)
    c: Coincident(g3,g2)
    c: Coincident(g3,g0)
    c: Horizontal(g3)
    c: DistanceX(g0) = -36
    c: DistanceX(g1) = 36
    c: DistanceY(g0) = -327
    c: DistanceY(g0,g0) = 50
FEATURE [Sketcher::SketchObject] Sketch047  label="outer016"
  FullyConstrained = true
  Placement = pos=(0,0,-281.2) rot=(0,0,1;0rad)
  sketch-geometry (4):
    g0: LineSegment StartX=-65 StartY=-252 StartZ=0 EndX=-65 EndY=-352 EndZ=0
    g1: LineSegment StartX=-65 StartY=-352 StartZ=0 EndX=65 EndY=-352 EndZ=0
    g2: LineSegment StartX=65 StartY=-352 StartZ=0 EndX=65 EndY=-252 EndZ=0
    g3: LineSegment StartX=65 StartY=-252 StartZ=0 EndX=-65 EndY=-252 EndZ=0
  constraints (12):
    c: Vertical(g0)
    c: Coincident(g1,g0)
    c: Horizontal(g1)
    c: Coincident(g2,g1)
    c: Vertical(g2)
    c: Coincident(g3,g2)
    c: Coincident(g3,g0)
    c: Horizontal(g3)
    c: DistanceX(g0) = -65
    c: DistanceX(g1) = 65
    c: DistanceY(g0) = -352
    c: DistanceY(g0,g0) = 100
FEATURE [Part::Loft] Loft016
  Closed = false
  MaxDegree = 5
  Ruled = false
  Sections = -> [Sketch046,Sketch047]
  Solid = true
FEATURE [Part::Fillet] Fillet024
  Base = -> Loft016
  Edges = 12 edges r=3: [Edge1,Edge2,Edge3,Edge4,Edge5,Edge6,Edge7,Edge8,Edge9,Edge10,Edge11,Edge12]
FEATURE [Sketcher::SketchObject] Sketch048  label="inner017"
  FullyConstrained = true
  Placement = pos=(0,0,-259.26) rot=(0,0,1;0rad)
  sketch-geometry (4):
    g0: LineSegment StartX=-36 StartY=-277 StartZ=0 EndX=-36 EndY=-327 EndZ=0
    g1: LineSegment StartX=-36 StartY=-327 StartZ=0 EndX=36 EndY=-327 EndZ=0
    g2: LineSegment StartX=36 StartY=-327 StartZ=0 EndX=36 EndY=-277 EndZ=0
    g3: LineSegment StartX=36 StartY=-277 StartZ=0 EndX=-36 EndY=-277 EndZ=0
  constraints (12):
    c: Vertical(g0)
    c: Coincident(g1,g0)
    c: Horizontal(g1)
    c: Coincident(g2,g1)
    c: Vertical(g2)
    c: Coincident(g3,g2)
    c: Coincident(g3,g0)
    c: Horizontal(g3)
    c: DistanceX(g0) = -36
    c: DistanceX(g1) = 36
    c: DistanceY(g0) = -327
    c: DistanceY(g0,g0) = 50
FEATURE [Sketcher::SketchObject] Sketch049  label="outer017"
  FullyConstrained = true
  Placement = pos=(0,0,-281.2) rot=(0,0,1;0rad)
  sketch-geometry (4):
    g0: LineSegment StartX=-65 StartY=-252 StartZ=0 EndX=-65 EndY=-352 EndZ=0
    g1: LineSegment StartX=-65 StartY=-352 StartZ=0 EndX=65 EndY=-352 EndZ=0
    g2: LineSegment StartX=65 StartY=-352 StartZ=0 EndX=65 EndY=-252 EndZ=0
    g3: LineSegment StartX=65 StartY=-252 StartZ=0 EndX=-65 EndY=-252 EndZ=0
  constraints (12):
    c: Vertical(g0)
    c: Coincident(g1,g0)
    c: Horizontal(g1)
    c: Coincident(g2,g1)
    c: Vertical(g2)
    c: Coincident(g3,g2)
    c: Coincident(g3,g0)
    c: Horizontal(g3)
    c: DistanceX(g0) = -65
    c: DistanceX(g1) = 65
    c: DistanceY(g0) = -352
    c: DistanceY(g0,g0) = 100
FEATURE [Part::Loft] Loft017
  Closed = false
  MaxDegree = 5
  Ruled = false
  Sections = -> [Sketch048,Sketch049]
  Solid = true
FEATURE [Part::Fillet] Fillet025
  Base = -> Loft017
  Edges = 12 edges r=3: [Edge1,Edge2,Edge3,Edge4,Edge5,Edge6,Edge7,Edge8,Edge9,Edge10,Edge11,Edge12]
  Placement = pos=(0,0,-4) rot=(0,0,1;0rad)
FEATURE [Part::Cut] Cut015  label="sls010"
  Base = -> Fillet024
  Placement = pos=(0,0,7) rot=(0,0,1;0rad)
  Tool = -> Fillet025
FEATURE [Sketcher::SketchObject] Sketch050  label="inner018"
  FullyConstrained = true
  Placement = pos=(0,0,-259.26) rot=(0,0,1;0rad)
  sketch-geometry (4):
    g0: LineSegment StartX=-36 StartY=-277 StartZ=0 EndX=-36 EndY=-327 EndZ=0
    g1: LineSegment StartX=-36 StartY=-327 StartZ=0 EndX=36 EndY=-327 EndZ=0
    g2: LineSegment StartX=36 StartY=-327 StartZ=0 EndX=36 EndY=-277 EndZ=0
    g3: LineSegment StartX=36 StartY=-277 StartZ=0 EndX=-36 EndY=-277 EndZ=0
  constraints (12):
    c: Vertical(g0)
    c: Coincident(g1,g0)
    c: Horizontal(g1)
    c: Coincident(g2,g1)
    c: Vertical(g2)
    c: Coincident(g3,g2)
    c: Coincident(g3,g0)
    c: Horizontal(g3)
    c: DistanceX(g0) = -36
    c: DistanceX(g1) = 36
    c: DistanceY(g0) = -327
    c: DistanceY(g0,g0) = 50
FEATURE [Sketcher::SketchObject] Sketch051  label="outer018"
  FullyConstrained = true
  Placement = pos=(0,0,-281.2) rot=(0,0,1;0rad)
  sketch-geometry (4):
    g0: LineSegment StartX=-65 StartY=-252 StartZ=0 EndX=-65 EndY=-352 EndZ=0
    g1: LineSegment StartX=-65 StartY=-352 StartZ=0 EndX=65 EndY=-352 EndZ=0
    g2: LineSegment StartX=65 StartY=-352 StartZ=0 EndX=65 EndY=-252 EndZ=0
    g3: LineSegment StartX=65 StartY=-252 StartZ=0 EndX=-65 EndY=-252 EndZ=0
  constraints (12):
    c: Vertical(g0)
    c: Coincident(g1,g0)
    c: Horizontal(g1)
    c: Coincident(g2,g1)
    c: Vertical(g2)
    c: Coincident(g3,g2)
    c: Coincident(g3,g0)
    c: Horizontal(g3)
    c: DistanceX(g0) = -65
    c: DistanceX(g1) = 65
    c: DistanceY(g0) = -352
    c: DistanceY(g0,g0) = 100
FEATURE [Part::Loft] Loft018
  Closed = false
  MaxDegree = 5
  Ruled = false
  Sections = -> [Sketch050,Sketch051]
  Solid = true
FEATURE [Part::Fillet] Fillet026
  Base = -> Loft018
  Edges = 12 edges r=3: [Edge1,Edge2,Edge3,Edge4,Edge5,Edge6,Edge7,Edge8,Edge9,Edge10,Edge11,Edge12]
FEATURE [Sketcher::SketchObject] Sketch052  label="inner019"
  FullyConstrained = true
  Placement = pos=(0,0,-259.26) rot=(0,0,1;0rad)
  sketch-geometry (4):
    g0: LineSegment StartX=-36 StartY=-277 StartZ=0 EndX=-36 EndY=-327 EndZ=0
    g1: LineSegment StartX=-36 StartY=-327 StartZ=0 EndX=36 EndY=-327 EndZ=0
    g2: LineSegment StartX=36 StartY=-327 StartZ=0 EndX=36 EndY=-277 EndZ=0
    g3: LineSegment StartX=36 StartY=-277 StartZ=0 EndX=-36 EndY=-277 EndZ=0
  constraints (12):
    c: Vertical(g0)
    c: Coincident(g1,g0)
    c: Horizontal(g1)
    c: Coincident(g2,g1)
    c: Vertical(g2)
    c: Coincident(g3,g2)
    c: Coincident(g3,g0)
    c: Horizontal(g3)
    c: DistanceX(g0) = -36
    c: DistanceX(g1) = 36
    c: DistanceY(g0) = -327
    c: DistanceY(g0,g0) = 50
FEATURE [Sketcher::SketchObject] Sketch053  label="outer019"
  FullyConstrained = true
  Placement = pos=(0,0,-281.2) rot=(0,0,1;0rad)
  sketch-geometry (4):
    g0: LineSegment StartX=-65 StartY=-252 StartZ=0 EndX=-65 EndY=-352 EndZ=0
    g1: LineSegment StartX=-65 StartY=-352 StartZ=0 EndX=65 EndY=-352 EndZ=0
    g2: LineSegment StartX=65 StartY=-352 StartZ=0 EndX=65 EndY=-252 EndZ=0
    g3: LineSegment StartX=65 StartY=-252 StartZ=0 EndX=-65 EndY=-252 EndZ=0
  constraints (12):
    c: Vertical(g0)
    c: Coincident(g1,g0)
    c: Horizontal(g1)
    c: Coincident(g2,g1)
    c: Vertical(g2)
    c: Coincident(g3,g2)
    c: Coincident(g3,g0)
    c: Horizontal(g3)
    c: DistanceX(g0) = -65
    c: DistanceX(g1) = 65
    c: DistanceY(g0) = -352
    c: DistanceY(g0,g0) = 100
FEATURE [Part::Loft] Loft019
  Closed = false
  MaxDegree = 5
  Ruled = false
  Sections = -> [Sketch052,Sketch053]
  Solid = true
FEATURE [Part::Fillet] Fillet027
  Base = -> Loft019
  Edges = 12 edges r=3: [Edge1,Edge2,Edge3,Edge4,Edge5,Edge6,Edge7,Edge8,Edge9,Edge10,Edge11,Edge12]
  Placement = pos=(0,0,-4) rot=(0,0,1;0rad)
FEATURE [Part::Cut] Cut016  label="sls011"
  Base = -> Fillet026
  Placement = pos=(0,0,10) rot=(0,0,1;0rad)
  Tool = -> Fillet027
FEATURE [Part::MultiFuse] Fusion040
  Placement = pos=(0,0,5) rot=(0,0,1;0rad)
  Shapes = -> [Cut016,Cut015,Cut014]
FEATURE [Part::MultiFuse] Fusion041  label="slsCUts"
  Shapes = -> [Fusion040,Fusion039]
FEATURE [Part::MultiFuse] Fusion042  label="slsCUts001"
  Shapes = -> [Fusion041,Extrude010]
FEATURE [Part::Cut] Cut017  label="sls012"
  Base = -> Cut012
  Tool = -> Fusion042
FEATURE [Part::Cut] Cut018  label="sls013"
  Base = -> Cut017
  Placement = pos=(0,17,15) rot=(0,0,1;0rad)
  Tool = -> Part__Feature153
FEATURE [Part::Cut] Cut019  label="base002"
  Base = -> Fusion038
  Placement = pos=(0,17,15) rot=(0,0,1;0rad)
  Tool = -> Extrude011
FEATURE [Sketcher::SketchObject] Sketch054
  FullyConstrained = true
  MapMode = 2
  Placement = pos=(-0.5,-512,-305.5) rot=(0.57735,-0.57735,-0.57735;2.0944rad)
  Support = -> [Compound002]
  sketch-geometry (8):
    g0: LineSegment StartX=-225.068 StartY=76.4427 StartZ=0 EndX=-228.265 EndY=72.5985 EndZ=0
    g1: LineSegment StartX=-228.265 StartY=72.5985 StartZ=0 EndX=-209.044 EndY=56.6125 EndZ=0
    g2: LineSegment StartX=-185 StartY=46.25 StartZ=0 EndX=-212.066 EndY=69.9864 EndZ=0
    g3: LineSegment StartX=-214.208 StartY=67.4108 StartZ=0 EndX=-212.066 EndY=69.9864 EndZ=0
    g4: LineSegment StartX=-214.208 StartY=67.4108 StartZ=0 EndX=-225.068 EndY=76.4427 EndZ=0
    g5: LineSegment StartX=-185 StartY=46.25 StartZ=0 EndX=-185 EndY=40.7882 EndZ=0
    g6: LineSegment StartX=-185 StartY=40.7882 StartZ=0 EndX=-203.044 EndY=56.6125 EndZ=0
    g7: LineSegment StartX=-203.044 StartY=56.6125 StartZ=0 EndX=-209.044 EndY=56.6125 EndZ=0
  constraints (24):
    c: Coincident(g0,g1)
    c: Coincident(g2,g3)
    c: Coincident(g4,g3)
    c: Coincident(g4,g0)
    c: Coincident(g5,g2)
    c: Coincident(g6,g5)
    c: Coincident(g7,g6)
    c: Horizontal(g7)
    c: Coincident(g1,g7)
    c: Parallel(g2,g6)
    c: Angle(g3,g2) = 1.54462
    c: Angle(g0,g4) = 1.5708
    c: Angle(g3,g4) = 1.5708
    c: DistanceX(g2) = -185
    c: DistanceY(g2) = 46.25
    c: Vertical(g5)
    c: Angle(g2,g5) = 2.29074
    c: Distance(g2) = 36
    c: Distance(g3) = 3.35
    c: Distance(g0) = 5
    c: Parallel(g4,g1)
    c: DistanceX(g7,g7) = 6
    c: Distance(g1) = 25
    c: Distance(g6) = 24
FEATURE [Part::Extrusion] Extrude014
  Base = -> Sketch054
  Dir = (-1,0,0)
  DirMode = 2
  FaceMakerClass = Part::FaceMakerBullseye
  LengthFwd = 69
  LengthRev = 0
  Placement = pos=(35,0,0) rot=(0,0,1;0rad)
  Solid = true
  Symmetric = false
FEATURE [Part::Cylinder] Cylinder
  Angle = 360
  AttacherType = Attacher::AttachEngine3D
  FirstAngle = 0
  Height = 15
  Placement = pos=(0,-287.79,-239.75) rot=(1,0,0;0.698132rad)
  Radius = 1.63
  SecondAngle = 0
FEATURE [Part::Cut] Cut020
  Base = -> Extrude014
  Tool = -> Cylinder
FEATURE [Part::MultiFuse] Fusion043  label="sls014"
  Shapes = -> [Cut020,Cut018]
FEATURE [Part::Feature] Part__Feature154  label="Body"
  shape: bbox 15.5 x 16.75 x 29 mm, 21 faces (baked)
FEATURE [Part::Feature] Part__Feature155  label="Body001"
  Placement = pos=(0,0,2) rot=(0,0,1;0rad)
  shape: bbox 17.44 x 17.44 x 14.25 mm, 14 faces (baked)
FEATURE [Part::Feature] Part__Feature156  label="Body002"
  Placement = pos=(0,0,-2.9) rot=(0,0,1;0rad)
  shape: bbox 19 x 19 x 4.75 mm, 25 faces (baked)
FEATURE [Part::Feature] Part__Feature157  label="Body003"
  shape: bbox 16.75 x 16.75 x 0.9 mm, 4 faces (baked)
FEATURE [App::Part] PG7_Gland1
  Group = -> [Part__Feature154,Part__Feature155,Part__Feature156,Part__Feature157]
  Origin = -> Origin017
  Placement = pos=(36,-274,-311.5) rot=(0,1,0;3.14159rad)
FEATURE [Part::Cone] Cone001
  Angle = 360
  AttacherType = Attacher::AttachEngine3D
  Height = 2
  Placement = pos=(0,0,26) rot=(0,0,1;0rad)
  Radius1 = 4
  Radius2 = 3.5
FEATURE [Part::Cylinder] Cylinder082
  Angle = 360
  AttacherType = Attacher::AttachEngine3D
  FirstAngle = 0
  Height = 28
  Radius = 2
  SecondAngle = 0
FEATURE [Part::Cylinder] Cylinder083
  Angle = 360
  AttacherType = Attacher::AttachEngine3D
  FirstAngle = 0
  Height = 2
  Placement = pos=(0,0,5) rot=(0,0,1;0rad)
  Radius = 3.75
  SecondAngle = 0
FEATURE [Part::Cylinder] Cylinder084
  Angle = 360
  AttacherType = Attacher::AttachEngine3D
  FirstAngle = 0
  Height = 1
  Placement = pos=(0,0,11) rot=(0,0,1;0rad)
  Radius = 3.75
  SecondAngle = 0
FEATURE [Part::Cylinder] Cylinder085
  Angle = 360
  AttacherType = Attacher::AttachEngine3D
  FirstAngle = 0
  Height = 8
  Placement = pos=(0,0,12) rot=(0,0,1;0rad)
  Radius = 3
  SecondAngle = 0
FEATURE [Part::Cylinder] Cylinder086
  Angle = 360
  AttacherType = Attacher::AttachEngine3D
  FirstAngle = 0
  Height = 6
  Placement = pos=(0,0,20) rot=(0,0,1;0rad)
  Radius = 4
  SecondAngle = 0
FEATURE [Part::Cylinder] Cylinder087
  Angle = 360
  AttacherType = Attacher::AttachEngine3D
  FirstAngle = 0
  Height = 2
  Placement = pos=(0,0,-2) rot=(0,0,1;0rad)
  Radius = 1
  SecondAngle = 0
FEATURE [Part::MultiFuse] Fusion025
  Shapes = -> [Cone001,Cylinder082,Cylinder083,Cylinder084,Cylinder085,Cylinder086]
FEATURE [Part::MultiFuse] Fusion026  label="micCut"
  Placement = pos=(0,-289,-301.5) rot=(0,1,0;3.14159rad)
  Shapes = -> [Cylinder087,Fusion025]
FEATURE [Part::Cone] Cone
  Angle = 360
  AttacherType = Attacher::AttachEngine3D
  Height = 2
  Placement = pos=(0,0,26) rot=(0,0,1;0rad)
  Radius1 = 4
  Radius2 = 3.5
FEATURE [Part::Cylinder] Cylinder020
  Angle = 360
  AttacherType = Attacher::AttachEngine3D
  FirstAngle = 0
  Height = 28
  Radius = 2
  SecondAngle = 0
FEATURE [Part::Cylinder] Cylinder021
  Angle = 360
  AttacherType = Attacher::AttachEngine3D
  FirstAngle = 0
  Height = 2
  Placement = pos=(0,0,5) rot=(0,0,1;0rad)
  Radius = 3.75
  SecondAngle = 0
FEATURE [Part::Cylinder] Cylinder022
  Angle = 360
  AttacherType = Attacher::AttachEngine3D
  FirstAngle = 0
  Height = 1
  Placement = pos=(0,0,11) rot=(0,0,1;0rad)
  Radius = 3.75
  SecondAngle = 0
FEATURE [Part::Cylinder] Cylinder023
  Angle = 360
  AttacherType = Attacher::AttachEngine3D
  FirstAngle = 0
  Height = 8
  Placement = pos=(0,0,12) rot=(0,0,1;0rad)
  Radius = 3
  SecondAngle = 0
FEATURE [Part::Cylinder] Cylinder024
  Angle = 360
  AttacherType = Attacher::AttachEngine3D
  FirstAngle = 0
  Height = 6
  Placement = pos=(0,0,20) rot=(0,0,1;0rad)
  Radius = 4
  SecondAngle = 0
FEATURE [Part::Cylinder] Cylinder025
  Angle = 360
  AttacherType = Attacher::AttachEngine3D
  FirstAngle = 0
  Height = 2
  Placement = pos=(0,0,-2) rot=(0,0,1;0rad)
  Radius = 1
  SecondAngle = 0
FEATURE [Part::MultiFuse] Fusion002
  Shapes = -> [Cone,Cylinder020,Cylinder021,Cylinder022,Cylinder023,Cylinder024]
FEATURE [Part::MultiFuse] Fusion044  label="mic"
  Placement = pos=(0,-289,-301.5) rot=(0,1,0;3.14159rad)
  Shapes = -> [Cylinder025,Fusion002]
FEATURE [Part::Feature] Part__Feature162  label="Body007"
  shape: bbox 15.5 x 16.75 x 29 mm, 21 faces (baked)
FEATURE [Part::Feature] Part__Feature163  label="Body008"
  Placement = pos=(0,0,2) rot=(0,0,1;0rad)
  shape: bbox 17.44 x 17.44 x 14.25 mm, 14 faces (baked)
FEATURE [Part::Feature] Part__Feature164  label="Body009"
  Placement = pos=(0,0,-2.9) rot=(0,0,1;0rad)
  shape: bbox 19 x 19 x 4.75 mm, 25 faces (baked)
FEATURE [Part::Feature] Part__Feature165  label="Body010"
  shape: bbox 16.75 x 16.75 x 0.9 mm, 4 faces (baked)
FEATURE [App::Part] PG7_Gland002
  Group = -> [Part__Feature162,Part__Feature163,Part__Feature164,Part__Feature165]
  Origin = -> Origin019
  Placement = pos=(-36,-274,-311.5) rot=(0,1,0;3.14159rad)
FEATURE [Sketcher::SketchObject] Sketch055
  FullyConstrained = true
  sketch-geometry (6):
    g0: Circle CenterX=-36 CenterY=-274 CenterZ=0 NormalX=0 NormalY=0 NormalZ=1 AngleXU=0 Radius=6.3
    g1: Circle CenterX=36 CenterY=-274 CenterZ=0 NormalX=0 NormalY=0 NormalZ=1 AngleXU=0 Radius=6.3
    g2: ArcOfCircle CenterX=0 CenterY=-289 CenterZ=0 NormalX=0 NormalY=0 NormalZ=1 AngleXU=0 Radius=2.125 StartAngle=1.2261 EndAngle=5.05709
    g3: LineSegment StartX=0.71807 StartY=-287 StartZ=0 EndX=4 EndY=-286.875 EndZ=0
    g4: LineSegment StartX=0.71807 StartY=-291 StartZ=0 EndX=4 EndY=-291.125 EndZ=0
    g5: ArcOfCircle CenterX=8.52597 CenterY=-289 CenterZ=0 NormalX=0 NormalY=0 NormalZ=1 AngleXU=0 Radius=5 StartAngle=3.58055 EndAngle=8.98582
  constraints (20):
    c: DistanceY(g0,g1) = 0
    c: DistanceY(g0) = -274
    c: DistanceX(g0) = -36
    c: DistanceX(g1) = 36
    c: Equal(g0,g1)
    c: Diameter(g0) = 12.6
    c: Diameter(g2) = 4.25
    c: Coincident(g3,g2)
    c: Coincident(g4,g2)
    c: DistanceY(g2) = -289
    c: DistanceX(g2) = 0
    c: DistanceY(g2,g3) = 0.125
    c: DistanceY(g4,g2) = 0.125
    c: DistanceX(g2,g2) = 0
    c: DistanceY(g2,g2) = 4
    c: DistanceX(g4) = 4
    c: Coincident(g5,g3)
    c: Diameter(g5) = 10
    c: DistanceY(g5,g2) = 0
    c: Coincident(g4,g5)
FEATURE [Part::Extrusion] Extrude015  label="baseCuts"
  Base = -> Sketch055
  Dir = (0,0,1)
  DirMode = 2
  FaceMakerClass = Part::FaceMakerBullseye
  LengthFwd = 6
  LengthRev = 0
  Placement = pos=(0,0,-314) rot=(0,0,1;0rad)
  Solid = true
  Symmetric = false
FEATURE [Sketcher::SketchObject] Sketch056
  FullyConstrained = true
  sketch-geometry (4):
    g0: ArcOfCircle CenterX=0 CenterY=-289 CenterZ=0 NormalX=0 NormalY=0 NormalZ=1 AngleXU=0 Radius=4.5 StartAngle=1.5708 EndAngle=4.71239
    g1: ArcOfCircle CenterX=8 CenterY=-289 CenterZ=0 NormalX=0 NormalY=0 NormalZ=1 AngleXU=0 Radius=4.5 StartAngle=4.71239 EndAngle=7.85398
    g2: LineSegment StartX=-8e-16 StartY=-293.5 StartZ=0 EndX=8 EndY=-293.5 EndZ=0
    g3: LineSegment StartX=8 StartY=-284.5 StartZ=0 EndX=-5.3e-15 EndY=-284.5 EndZ=0
  constraints (10):
    c: Tangent(g0,g2) = -1.5708
    c: Tangent(g2,g1) = -1.5708
    c: Tangent(g1,g3) = -1.5708
    c: Tangent(g3,g0) = -1.5708
    c: Equal(g0,g1)
    c: Horizontal(g2)
    c: DistanceY(g0) = -289
    c: Radius(g0) = 4.5
    c: DistanceX(g0,g1) = 8
    c: DistanceX(g0) = 0
FEATURE [Part::Extrusion] Extrude016  label="baseCuts002"
  Base = -> Sketch056
  Dir = (0,0,1)
  DirMode = 2
  FaceMakerClass = Part::FaceMakerBullseye
  LengthFwd = 6
  LengthRev = 0
  Placement = pos=(0,0,-318.25) rot=(0,0,1;0rad)
  Solid = true
  Symmetric = false
FEATURE [Part::MultiFuse] Fusion045  label="baseCuts003"
  Shapes = -> [Extrude015,Extrude016]
FEATURE [Sketcher::SketchObject] Sketch057
  FullyConstrained = true
  sketch-geometry (1):
    g0: Circle CenterX=0 CenterY=-289 CenterZ=0 NormalX=0 NormalY=0 NormalZ=1 AngleXU=0 Radius=18
  constraints (3):
    c: DistanceX(g0) = 0
    c: Radius(g0) = 18
    c: DistanceY(g0) = -289
FEATURE [Sketcher::SketchObject] Sketch058
  FullyConstrained = true
  Placement = pos=(0,0,-15) rot=(0,0,1;0rad)
  sketch-geometry (1):
    g0: Circle CenterX=0 CenterY=-289 CenterZ=0 NormalX=0 NormalY=0 NormalZ=1 AngleXU=0 Radius=22
  constraints (3):
    c: DistanceX(g0) = 0
    c: Radius(g0) = 22
    c: DistanceY(g0) = -289
FEATURE [Part::Loft] Loft020
  Closed = false
  MaxDegree = 5
  Placement = pos=(0,0,-312.5) rot=(0,0,1;0rad)
  Ruled = false
  Sections = -> [Sketch057,Sketch058]
  Solid = true
FEATURE [Sketcher::SketchObject] Sketch059
  FullyConstrained = true
  sketch-geometry (1):
    g0: Circle CenterX=0 CenterY=-289 CenterZ=0 NormalX=0 NormalY=0 NormalZ=1 AngleXU=0 Radius=14
  constraints (3):
    c: DistanceX(g0) = 0
    c: Radius(g0) = 14
    c: DistanceY(g0) = -289
FEATURE [Sketcher::SketchObject] Sketch060
  FullyConstrained = true
  Placement = pos=(0,0,-15) rot=(0,0,1;0rad)
  sketch-geometry (1):
    g0: Circle CenterX=0 CenterY=-289 CenterZ=0 NormalX=0 NormalY=0 NormalZ=1 AngleXU=0 Radius=18
  constraints (3):
    c: DistanceX(g0) = 0
    c: Radius(g0) = 18
    c: DistanceY(g0) = -289
FEATURE [Part::Loft] Loft021
  Closed = false
  MaxDegree = 5
  Placement = pos=(0,0,-312.5) rot=(0,0,1;0rad)
  Ruled = false
  Sections = -> [Sketch059,Sketch060]
  Solid = true
FEATURE [Part::Cut] Cut021  label="micSlot"
  Base = -> Loft020
  Tool = -> Loft021
FEATURE [Part::MultiFuse] Fusion046  label="base003"
  Shapes = -> [Cut019,Cut021]
FEATURE [Part::Cut] Cut022  label="base004"
  Base = -> Fusion046
  Tool = -> Fusion045
FEATURE [Sketcher::SketchObject] Sketch061
  FullyConstrained = true
  Placement = pos=(0,0,0) rot=(0.57735,0.57735,0.57735;2.0944rad)
  sketch-geometry (4):
    g0: LineSegment StartX=-112 StartY=-91 StartZ=0 EndX=-108.786 EndY=-94.8302 EndZ=0
    g1: LineSegment StartX=-112 StartY=-91 StartZ=0 EndX=-39.9918 EndY=-30.578 EndZ=0
    g2: LineSegment StartX=-39.9918 StartY=-30.578 StartZ=0 EndX=-36.7779 EndY=-34.4082 EndZ=0
    g3: LineSegment StartX=-36.7779 StartY=-34.4082 StartZ=0 EndX=-108.786 EndY=-94.8302 EndZ=0
  constraints (12):
    c: Coincident(g1,g0)
    c: Coincident(g2,g1)
    c: Coincident(g3,g2)
    c: Coincident(g3,g0)
    c: DistanceX(g0) = -112
    c: Angle(g1) = 0.698132
    c: Parallel(g1,g3)
    c: Angle(g0,g1) = 1.5708
    c: Angle(g1,g2) = 1.5708
    c: Distance(g1) = 94
    c: Distance(g0,g0) = 5
    c: DistanceY(g0) = -91
FEATURE [Part::Extrusion] Extrude017
  Base = -> Sketch061
  Dir = (1,0,0)
  DirMode = 2
  FaceMakerClass = Part::FaceMakerBullseye
  LengthFwd = 15
  LengthRev = 0
  Placement = pos=(-138.75,0,0) rot=(0,0,1;0rad)
  Solid = true
  Symmetric = false
FEATURE [Part::Box] Box004  label="Cube002"
  AttacherType = Attacher::AttachEngine3D
  Height = 14.5
  Length = 31
  Placement = pos=(134,-34,55) rot=(0,0,1;0rad)
  Width = 68
FEATURE [Part::Box] Box006  label="wireGuardCut"
  AttacherType = Attacher::AttachEngine3D
  Height = 10
  Length = 15
  Placement = pos=(127,30.1,65) rot=(1,0,0;3.14159rad)
  Width = 10
FEATURE [Part::Cylinder] Cylinder088
  Angle = 360
  AttacherType = Attacher::AttachEngine3D
  FirstAngle = 0
  Height = 5.82
  Placement = pos=(0,-21,0) rot=(0,0,1;0rad)
  Radius = 5
  SecondAngle = 0
FEATURE [Part::Cylinder] Cylinder089
  Angle = 360
  AttacherType = Attacher::AttachEngine3D
  FirstAngle = 0
  Height = 5.82
  Placement = pos=(20.5,-21,0) rot=(0,0,1;0rad)
  Radius = 5
  SecondAngle = 0
  expr: Radius = 5
FEATURE [Part::Cylinder] Cylinder090
  Angle = 360
  AttacherType = Attacher::AttachEngine3D
  FirstAngle = 0
  Height = 5.82
  Placement = pos=(0,-21,0) rot=(0,0,1;0rad)
  Radius = 5
  SecondAngle = 0
FEATURE [Part::Cylinder] Cylinder091
  Angle = 360
  AttacherType = Attacher::AttachEngine3D
  FirstAngle = 0
  Height = 5.82
  Placement = pos=(20.5,-21,0) rot=(0,0,1;0rad)
  Radius = 5
  SecondAngle = 0
FEATURE [Part::Cylinder] Cylinder026  label="base006"
  Angle = 360
  AttacherType = Attacher::AttachEngine3D
  FirstAngle = 0
  Height = 4.5
  Placement = pos=(136,0,65) rot=(0,0,1;0rad)
  Radius = 40
  SecondAngle = 0
FEATURE [Part::Cylinder] Cylinder027  label="baseCut"
  Angle = 360
  AttacherType = Attacher::AttachEngine3D
  FirstAngle = 0
  Height = 7
  Placement = pos=(5,0,74) rot=(0,0,1;0rad)
  Radius = 24
  SecondAngle = 0
FEATURE [Part::Cylinder] Cylinder032  label="m2HeatSetInsets"
  Angle = 360
  AttacherType = Attacher::AttachEngine3D
  FirstAngle = 0
  Height = 10
  Placement = pos=(-30,0,65) rot=(0,0,1;0rad)
  Radius = 2
  SecondAngle = 0
  expr: Radius = 2
FEATURE [Part::Cylinder] Cylinder033  label="m2HeatSetInsets001"
  Angle = 360
  AttacherType = Attacher::AttachEngine3D
  FirstAngle = 0
  Height = 10
  Placement = pos=(40,0,65) rot=(0,0,1;0rad)
  Radius = 2
  SecondAngle = 0
FEATURE [Part::Cylinder] Cylinder034  label="m2HeatSetInsets002"
  Angle = 360
  AttacherType = Attacher::AttachEngine3D
  FirstAngle = 0
  Height = 10
  Placement = pos=(5,35,65) rot=(0,0,1;0rad)
  Radius = 2
  SecondAngle = 0
FEATURE [Part::Cylinder] Cylinder035  label="m2HeatSetInsets003"
  Angle = 360
  AttacherType = Attacher::AttachEngine3D
  FirstAngle = 0
  Height = 10
  Placement = pos=(5,-35,65) rot=(0,0,1;0rad)
  Radius = 2
  SecondAngle = 0
  expr: Radius = 2
FEATURE [Part::Cylinder] Cylinder036
  Angle = 360
  AttacherType = Attacher::AttachEngine3D
  FirstAngle = 0
  Height = 10
  Placement = pos=(0,-21,0) rot=(0,0,1;0rad)
  Radius = 2
  SecondAngle = 0
FEATURE [Part::Cylinder] Cylinder037
  Angle = 360
  AttacherType = Attacher::AttachEngine3D
  FirstAngle = 0
  Height = 10
  Placement = pos=(20.5,-21,0) rot=(0,0,1;0rad)
  Radius = 2
  SecondAngle = 0
FEATURE [Part::Cylinder] Cylinder038
  Angle = 360
  AttacherType = Attacher::AttachEngine3D
  FirstAngle = 0
  Height = 10
  Placement = pos=(0,-21,0) rot=(0,0,1;0rad)
  Radius = 2
  SecondAngle = 0
FEATURE [Part::Cylinder] Cylinder039
  Angle = 360
  AttacherType = Attacher::AttachEngine3D
  FirstAngle = 0
  Height = 10
  Placement = pos=(20.5,-21,0) rot=(0,0,1;0rad)
  Radius = 2
  SecondAngle = 0
FEATURE [Part::Cylinder] Cylinder044  label="m3Cut002"
  Angle = 360
  AttacherType = Attacher::AttachEngine3D
  FirstAngle = 0
  Height = 7
  Placement = pos=(-4.5,-22,62.5) rot=(0,0,1;0rad)
  Radius = 1.8
  SecondAngle = 0
FEATURE [Part::Cylinder] Cylinder045  label="m3Cut003"
  Angle = 360
  AttacherType = Attacher::AttachEngine3D
  FirstAngle = 0
  Height = 7
  Placement = pos=(-4.5,-22,67.5) rot=(0,0,1;0rad)
  Radius = 3
  SecondAngle = 0
FEATURE [Part::Cylinder] Cylinder046
  Angle = 360
  AttacherType = Attacher::AttachEngine3D
  FirstAngle = 0
  Height = 14.5
  Placement = pos=(134,32.6,55) rot=(0,0,1;0rad)
  Radius = 5.5
  SecondAngle = 0
FEATURE [Part::Cylinder] Cylinder047  label="WireCut"
  Angle = 360
  AttacherType = Attacher::AttachEngine3D
  FirstAngle = 0
  Height = 60
  Placement = pos=(134,32.6,20) rot=(0,0,1;0rad)
  Radius = 2.5
  SecondAngle = 0
FEATURE [Part::Cylinder] Cylinder048  label="m3_5Add001"
  Angle = 360
  AttacherType = Attacher::AttachEngine3D
  FirstAngle = 0
  Height = 3
  Placement = pos=(150.5,22,62.5) rot=(0,0,1;0rad)
  Radius = 3
  SecondAngle = 0
FEATURE [Part::Cylinder] Cylinder050  label="m3Cut004"
  Angle = 360
  AttacherType = Attacher::AttachEngine3D
  FirstAngle = 0
  Height = 2
  Placement = pos=(150.5,-22,65) rot=(0,0,1;0rad)
  Radius = 3.2
  SecondAngle = 0
FEATURE [Part::Fillet] Fillet005
  Base = -> Box004
  Edges = 1 edges r=10: [Edge5]
FEATURE [Part::Fillet] Fillet006
  Base = -> Fillet005
  Edges = 1 edges r=10: [Edge4]
FEATURE [Part::MultiFuse] Fusion010  label="m3HeatSetCuts"
  Placement = pos=(-5,39,70) rot=(0,0,1;0rad)
  Shapes = -> [Cylinder089,Cylinder088]
FEATURE [Part::MultiFuse] Fusion011  label="m3HeatSetCuts001"
  Placement = pos=(-5,3,70) rot=(0,0,1;0rad)
  Shapes = -> [Cylinder091,Cylinder090]
FEATURE [Part::MultiFuse] Fusion012  label="m3HeatSetCuts002"
  Placement = pos=(128.75,10,-1) rot=(0,0,1;0rad)
  Shapes = -> [Fusion011,Fusion010]
FEATURE [Part::MultiFuse] Fusion016
  Placement = pos=(129,10,0) rot=(0,0,1;0rad)
  Shapes = -> [Cylinder032,Cylinder033,Cylinder034,Cylinder035]
FEATURE [Part::MultiFuse] Fusion048  label="m3HeatSetCuts003"
  Placement = pos=(-5,39,70) rot=(0,0,1;0rad)
  Shapes = -> [Cylinder037,Cylinder036]
FEATURE [Part::MultiFuse] Fusion049  label="m3HeatSetCuts004"
  Placement = pos=(-5,3,70) rot=(0,0,1;0rad)
  Shapes = -> [Cylinder039,Cylinder038]
FEATURE [Part::MultiFuse] Fusion021  label="m3HeatSetCuts005"
  Placement = pos=(128.75,10,-1) rot=(0,0,1;0rad)
  Shapes = -> [Fusion049,Fusion048]
FEATURE [Part::MultiFuse] Fusion050  label="cutScrew"
  Placement = pos=(155,44,0) rot=(0,0,1;0rad)
  Shapes = -> [Cylinder045,Cylinder044]
FEATURE [Part::MultiFuse] Fusion028  label="cuts"
  Shapes = -> [Cylinder047,Fusion016,Fusion021,Fusion050]
FEATURE [Sketcher::SketchObject] Sketch062
  FullyConstrained = false
  MapMode = 5
  Support = -> [XY_Plane020]
  sketch-geometry (49):
    g0: GeomPoint X=44.5093 Y=-30.668 Z=0
    g1: GeomPoint X=85.7303 Y=-30.7001 Z=0
    g2: GeomPoint X=87.2659 Y=-30.5404 Z=0
    g3: GeomPoint X=91.8923 Y=-26.8165 Z=0
    g4: GeomPoint X=92.4288 Y=-25.33 Z=0
    g5: GeomPoint X=93.1446 Y=-20.5457 Z=0
    g6: GeomPoint X=93.6599 Y=-16.0974 Z=0
    g7: GeomPoint X=93.9312 Y=-11.8931 Z=0
    g8: GeomPoint X=93.9312 Y=6.25646 Z=0
    g9: GeomPoint X=93.9401 Y=8.91625 Z=0
    g10: GeomPoint X=93.8644 Y=12.7559 Z=0
    g11: GeomPoint X=93.2714 Y=19.6725 Z=0
    g12: GeomPoint X=92.3963 Y=25.2341 Z=0
    g13: GeomPoint X=91.8282 Y=26.7962 Z=0
    g14: GeomPoint X=91.1285 Y=27.9983 Z=0
    g15: GeomPoint X=90.1597 Y=29.0389 Z=0
    g16: GeomPoint X=88.8662 Y=29.8509 Z=0
    g17: GeomPoint X=87.4629 Y=30.4081 Z=0
    g18: GeomPoint X=85.8119 Y=30.6351 Z=0
    g19: GeomPoint X=79.1753 Y=30.6351 Z=0
    g20: GeomPoint X=78.6575 Y=30.0897 Z=0
    g21: GeomPoint X=44.5006 Y=30.0897 Z=0
    g22: LineSegment StartX=44.5093 StartY=-30.668 StartZ=0 EndX=85.7303 EndY=-30.7001 EndZ=0
    g23: LineSegment StartX=85.7303 StartY=-30.7001 StartZ=0 EndX=87.2659 EndY=-30.5404 EndZ=0
    g24: LineSegment StartX=91.0945 StartY=-28.018 StartZ=0 EndX=91.8923 EndY=-26.8165 EndZ=0
    g25: LineSegment StartX=91.8923 StartY=-26.8165 StartZ=0 EndX=92.4288 EndY=-25.33 EndZ=0
    g26: LineSegment StartX=92.4288 StartY=-25.33 StartZ=0 EndX=93.1446 EndY=-20.5457 EndZ=0
    g27: LineSegment StartX=93.1446 StartY=-20.5457 StartZ=0 EndX=93.6599 EndY=-16.0974 EndZ=0
    g28: LineSegment StartX=93.6599 StartY=-16.0974 StartZ=0 EndX=93.9312 EndY=-11.8931 EndZ=0
    g29: LineSegment StartX=93.9312 StartY=-11.8931 StartZ=0 EndX=93.9312 EndY=6.25646 EndZ=0
    g30: LineSegment StartX=93.9312 StartY=6.25646 StartZ=0 EndX=93.9401 EndY=8.91625 EndZ=0
    g31: GeomPoint X=93.5743 Y=16.1437 Z=0
    g32: LineSegment StartX=93.9401 StartY=8.91625 StartZ=0 EndX=93.8644 EndY=12.7559 EndZ=0
    g33: LineSegment StartX=93.8644 StartY=12.7559 StartZ=0 EndX=93.5743 EndY=16.1437 EndZ=0
    g34: LineSegment StartX=93.5743 StartY=16.1437 StartZ=0 EndX=93.2714 EndY=19.6725 EndZ=0
    g35: LineSegment StartX=93.2714 StartY=19.6725 StartZ=0 EndX=92.3963 EndY=25.2341 EndZ=0
    g36: LineSegment StartX=92.3963 StartY=25.2341 StartZ=0 EndX=91.8282 EndY=26.7962 EndZ=0
    g37: LineSegment StartX=91.8282 StartY=26.7962 StartZ=0 EndX=91.1285 EndY=27.9983 EndZ=0
    g38: LineSegment StartX=91.1285 StartY=27.9983 StartZ=0 EndX=90.1597 EndY=29.0389 EndZ=0
    g39: LineSegment StartX=90.1597 StartY=29.0389 StartZ=0 EndX=88.8662 EndY=29.8509 EndZ=0
    g40: LineSegment StartX=88.8662 StartY=29.8509 StartZ=0 EndX=87.4629 EndY=30.4081 EndZ=0
    g41: LineSegment StartX=87.4629 StartY=30.4081 StartZ=0 EndX=85.8119 EndY=30.6351 EndZ=0
    g42: LineSegment StartX=85.8119 StartY=30.6351 StartZ=0 EndX=79.1753 EndY=30.6351 EndZ=0
    g43: LineSegment StartX=79.1753 StartY=30.6351 StartZ=0 EndX=78.6575 EndY=30.0897 EndZ=0
    g44: LineSegment StartX=78.6575 StartY=30.0897 StartZ=0 EndX=44.5006 EndY=30.0897 EndZ=0
    g45: LineSegment StartX=44.5093 StartY=-30.668 StartZ=0 EndX=44.5006 EndY=30.0897 EndZ=0
    g46: LineSegment StartX=87.2659 StartY=-30.5404 StartZ=0 EndX=88.7273 EndY=-30.0287 EndZ=0
    g47: LineSegment StartX=88.7273 StartY=-30.0287 StartZ=0 EndX=90.018 EndY=-29.1936 EndZ=0
    g48: LineSegment StartX=90.018 StartY=-29.1936 StartZ=0 EndX=91.0945 EndY=-28.018 EndZ=0
  constraints (42):
    c: Coincident(g22,g0)
    c: Coincident(g22,g1)
    c: Coincident(g23,g22)
    c: Coincident(g23,g2)
    c: Coincident(g24,g3)
    c: Coincident(g25,g24)
    c: Coincident(g25,g4)
    c: Coincident(g26,g25)
    c: Coincident(g26,g5)
    c: Coincident(g27,g26)
    c: Coincident(g27,g6)
    c: Coincident(g28,g27)
    c: Coincident(g28,g7)
    c: Coincident(g29,g28)
    c: Coincident(g29,g8)
    c: Coincident(g30,g29)
    c: Coincident(g30,g9)
    c: Coincident(g32,g30)
    c: Coincident(g32,g10)
    c: Coincident(g33,g32)
    c: Coincident(g33,g31)
    c: Coincident(g34,g11)
    c: Coincident(g35,g34)
    c: Coincident(g35,g12)
    c: Coincident(g36,g13)
    c: Coincident(g37,g14)
    c: Coincident(g38,g37)
    c: Coincident(g38,g15)
    c: Coincident(g39,g16)
    c: Coincident(g40,g17)
    c: Coincident(g41,g18)
    c: Coincident(g42,g41)
    c: Coincident(g42,g19)
    c: Coincident(g43,g42)
    c: Coincident(g43,g20)
    c: Coincident(g44,g43)
    c: Coincident(g44,g21)
    c: Coincident(g45,g22)
    c: Coincident(g46,g23)
    c: Coincident(g47,g46)
    c: Coincident(g48,g47)
    c: Coincident(g48,g24)
FEATURE [PartDesign::Pad] Pad001
  Direction = (0,0,1)
  Length = 10
  Length2 = 10
  Profile = -> Sketch062
  ReferenceAxis = -> Sketch062 [N_Axis]
  Type = 0
  expr: Length = 10
FEATURE [PartDesign::Body] Body001  label="Body011"
  Group = -> [Sketch062,Pad001]
  Origin = -> Origin020
  Placement = pos=(68,0,55) rot=(0,0,1;0rad)
  Tip = -> Pad001
FEATURE [Part::Cut] Cut024  label="base005"
  Base = -> Fillet006
  Tool = -> Body001
FEATURE [Part::Fillet] Fillet007
  Base = -> Cut024
  Edges = 1 edges r=1: [Edge41]
FEATURE [Part::Fillet] Fillet028
  Base = -> Fillet007
  Edges = 1 edges r=1: [Edge6]
FEATURE [Part::Fillet] Fillet029
  Base = -> Fillet028
  Edges = 1 edges r=1: [Edge17]
FEATURE [Part::Sphere] Sphere001  label="SphereBase"
  Angle1 = 0
  Angle2 = 12
  Angle3 = 360
  AttacherType = Attacher::AttachEngine3D
  Placement = pos=(5,0,74) rot=(0,0,1;0rad)
  Radius = 28.3
FEATURE [Part::Cut] Cut023
  Base = -> Sphere001
  Placement = pos=(131,0,-5) rot=(0,0,1;0rad)
  Tool = -> Cylinder027
FEATURE [Part::MultiFuse] Fusion047  label="Base"
  Placement = pos=(-2,10,0) rot=(0,0,1;0rad)
  Shapes = -> [Cut023,Cylinder026]
FEATURE [Part::MultiFuse] Fusion051  label="base007"
  Shapes = -> [Fusion047,Cylinder048,Cylinder046,Fusion012]
FEATURE [Part::MultiFuse] Fusion030
  Shapes = -> [Fillet029,Fusion051]
FEATURE [Part::Cut] Cut025
  Base = -> Fusion030
  Tool = -> Fusion028
FEATURE [Part::Fillet] Fillet030
  Base = -> Cut025
  Edges = 1 edges r=1: [Edge175]
FEATURE [Part::Fillet] Fillet031
  Base = -> Fillet030
  Edges = 1 edges r=0.5: [Edge7]
FEATURE [Part::Fillet] Fillet032
  Base = -> Fillet031
  Edges = 1 edges r=1: [Edge60]
FEATURE [Part::Fillet] Fillet033
  Base = -> Fillet032
  Edges = 1 edges r=1: [Edge86]
FEATURE [Part::Cut] Cut026
  Base = -> Fillet033
  Tool = -> Box006
FEATURE [Part::Fillet] Fillet034
  Base = -> Cut026
  Edges = 2 edges r=1: [Edge74,Edge75]
FEATURE [Part::Fillet] Fillet035
  Base = -> Fillet034
  Edges = 2 edges r=1: [Edge47,Edge199]
FEATURE [Part::Fillet] Fillet036
  Base = -> Fillet035
  Edges = 4 edges r=1: [Edge63,Edge94,Edge102,Edge105]
FEATURE [Part::Fillet] Fillet037  label="lightModule"
  Base = -> Fillet036
  Edges = 4 edges r=0.5: [Edge16,Edge22,Edge74,Edge75]
FEATURE [Part::Cut] Cut009  label="lightModule001"
  Base = -> Fillet037
  Tool = -> Cylinder050
FEATURE [Part::Cylinder] Cylinder092  label="base008"
  Angle = 360
  AttacherType = Attacher::AttachEngine3D
  FirstAngle = 0
  Height = 4.5
  Placement = pos=(136,0,65) rot=(0,0,1;0rad)
  Radius = 40
  SecondAngle = 0
FEATURE [Part::Cylinder] Cylinder093  label="baseCut001"
  Angle = 360
  AttacherType = Attacher::AttachEngine3D
  FirstAngle = 0
  Height = 7
  Placement = pos=(5,0,74) rot=(0,0,1;0rad)
  Radius = 24
  SecondAngle = 0
FEATURE [Part::Cylinder] Cylinder094
  Angle = 360
  AttacherType = Attacher::AttachEngine3D
  FirstAngle = 0
  Height = 14.5
  Placement = pos=(134,32.6,55) rot=(0,0,1;0rad)
  Radius = 5.5
  SecondAngle = 0
FEATURE [Part::Cylinder] Cylinder096
  Angle = 360
  AttacherType = Attacher::AttachEngine3D
  FirstAngle = 0
  Height = 5.82
  Placement = pos=(0,-21,0) rot=(0,0,1;0rad)
  Radius = 5
  SecondAngle = 0
FEATURE [Part::Cylinder] Cylinder097
  Angle = 360
  AttacherType = Attacher::AttachEngine3D
  FirstAngle = 0
  Height = 5.82
  Placement = pos=(20.5,-21,0) rot=(0,0,1;0rad)
  Radius = 5
  SecondAngle = 0
  expr: Radius = 5
FEATURE [Part::Cylinder] Cylinder098
  Angle = 360
  AttacherType = Attacher::AttachEngine3D
  FirstAngle = 0
  Height = 5.82
  Placement = pos=(0,-21,0) rot=(0,0,1;0rad)
  Radius = 5
  SecondAngle = 0
FEATURE [Part::Cylinder] Cylinder099
  Angle = 360
  AttacherType = Attacher::AttachEngine3D
  FirstAngle = 0
  Height = 5.82
  Placement = pos=(20.5,-21,0) rot=(0,0,1;0rad)
  Radius = 5
  SecondAngle = 0
FEATURE [Part::MultiFuse] Fusion052  label="m3HeatSetCuts006"
  Placement = pos=(-5,39,70) rot=(0,0,1;0rad)
  Shapes = -> [Cylinder097,Cylinder096]
FEATURE [Part::MultiFuse] Fusion053  label="m3HeatSetCuts007"
  Placement = pos=(-5,3,70) rot=(0,0,1;0rad)
  Shapes = -> [Cylinder099,Cylinder098]
FEATURE [Part::MultiFuse] Fusion054  label="m3HeatSetCuts008"
  Placement = pos=(128.75,10,-1) rot=(0,0,1;0rad)
  Shapes = -> [Fusion053,Fusion052]
FEATURE [Part::Sphere] Sphere003  label="SphereBase001"
  Angle1 = 0
  Angle2 = 12
  Angle3 = 360
  AttacherType = Attacher::AttachEngine3D
  Placement = pos=(5,0,74) rot=(0,0,1;0rad)
  Radius = 28.3
FEATURE [Part::Cut] Cut027
  Base = -> Sphere003
  Placement = pos=(131,0,-5) rot=(0,0,1;0rad)
  Tool = -> Cylinder093
FEATURE [Part::MultiFuse] Fusion055  label="Base001"
  Placement = pos=(-2,10,0) rot=(0,0,1;0rad)
  Shapes = -> [Cut027,Cylinder092]
FEATURE [Part::MultiFuse] Fusion056  label="lightModule002"
  Shapes = -> [Fusion055,Cylinder094,Fusion054]
FEATURE [Part::Cylinder] Cylinder100  label="m2HeatSetInsets004"
  Angle = 360
  AttacherType = Attacher::AttachEngine3D
  FirstAngle = 0
  Height = 10
  Placement = pos=(-30,0,65) rot=(0,0,1;0rad)
  Radius = 2
  SecondAngle = 0
  expr: Radius = 2
FEATURE [Part::Cylinder] Cylinder101  label="m2HeatSetInsets005"
  Angle = 360
  AttacherType = Attacher::AttachEngine3D
  FirstAngle = 0
  Height = 10
  Placement = pos=(40,0,65) rot=(0,0,1;0rad)
  Radius = 2
  SecondAngle = 0
FEATURE [Part::Cylinder] Cylinder102  label="m2HeatSetInsets006"
  Angle = 360
  AttacherType = Attacher::AttachEngine3D
  FirstAngle = 0
  Height = 10
  Placement = pos=(5,35,65) rot=(0,0,1;0rad)
  Radius = 2
  SecondAngle = 0
FEATURE [Part::Cylinder] Cylinder103  label="m2HeatSetInsets007"
  Angle = 360
  AttacherType = Attacher::AttachEngine3D
  FirstAngle = 0
  Height = 10
  Placement = pos=(5,-35,65) rot=(0,0,1;0rad)
  Radius = 2
  SecondAngle = 0
  expr: Radius = 2
FEATURE [Part::Cylinder] Cylinder104
  Angle = 360
  AttacherType = Attacher::AttachEngine3D
  FirstAngle = 0
  Height = 10
  Placement = pos=(0,-21,0) rot=(0,0,1;0rad)
  Radius = 2
  SecondAngle = 0
FEATURE [Part::Cylinder] Cylinder105
  Angle = 360
  AttacherType = Attacher::AttachEngine3D
  FirstAngle = 0
  Height = 10
  Placement = pos=(20.5,-21,0) rot=(0,0,1;0rad)
  Radius = 2
  SecondAngle = 0
FEATURE [Part::Cylinder] Cylinder106
  Angle = 360
  AttacherType = Attacher::AttachEngine3D
  FirstAngle = 0
  Height = 10
  Placement = pos=(0,-21,0) rot=(0,0,1;0rad)
  Radius = 2
  SecondAngle = 0
FEATURE [Part::Cylinder] Cylinder107
  Angle = 360
  AttacherType = Attacher::AttachEngine3D
  FirstAngle = 0
  Height = 10
  Placement = pos=(20.5,-21,0) rot=(0,0,1;0rad)
  Radius = 2
  SecondAngle = 0
FEATURE [Part::Cylinder] Cylinder110  label="WireCut001"
  Angle = 360
  AttacherType = Attacher::AttachEngine3D
  FirstAngle = 0
  Height = 60
  Placement = pos=(134,32.6,20) rot=(0,0,1;0rad)
  Radius = 2.5
  SecondAngle = 0
FEATURE [Part::MultiFuse] Fusion057
  Placement = pos=(129,10,0) rot=(0,0,1;0rad)
  Shapes = -> [Cylinder100,Cylinder101,Cylinder102,Cylinder103]
FEATURE [Part::MultiFuse] Fusion060  label="m3HeatSetCuts010"
  Placement = pos=(-5,39,70) rot=(0,0,1;0rad)
  Shapes = -> [Cylinder105,Cylinder104]
FEATURE [Part::MultiFuse] Fusion061  label="m3HeatSetCuts011"
  Placement = pos=(-5,3,70) rot=(0,0,1;0rad)
  Shapes = -> [Cylinder107,Cylinder106]
FEATURE [Part::MultiFuse] Fusion058  label="m3HeatSetCuts009"
  Placement = pos=(128.75,10,-1) rot=(0,0,1;0rad)
  Shapes = -> [Fusion061,Fusion060]
FEATURE [Sketcher::SketchObject] Sketch063
  FullyConstrained = false
  sketch-geometry (7):
    g0: LineSegment StartX=-180 StartY=-72 StartZ=0 EndX=-154.301 EndY=-72 EndZ=0
    g1: LineSegment StartX=-154.301 StartY=-72 StartZ=0 EndX=-154.301 EndY=-111.747 EndZ=0
    g2: ArcOfCircle CenterX=-180 CenterY=-112 CenterZ=0 NormalX=0 NormalY=0 NormalZ=1 AngleXU=0 Radius=40 StartAngle=1.5708 EndAngle=3.14159
    g3: LineSegment StartX=-220 StartY=-112 StartZ=0 EndX=-220 EndY=-176.929 EndZ=0
    g4: LineSegment StartX=-220 StartY=-176.929 StartZ=0 EndX=-201.388 EndY=-176.929 EndZ=0
    g5: LineSegment StartX=-201.388 StartY=-176.929 StartZ=0 EndX=-201.388 EndY=-111.747 EndZ=0
    g6: LineSegment StartX=-201.388 StartY=-111.747 StartZ=0 EndX=-154.301 EndY=-111.747 EndZ=0
  constraints (17):
    c: Horizontal(g0)
    c: Coincident(g1,g0)
    c: Vertical(g1)
    c: Coincident(g2,g0)
    c: Radius(g2) = 40
    c: Angle(g2) = 1.5708
    c: DistanceX(g2) = -180
    c: DistanceY(g2) = -112
    c: Coincident(g3,g2)
    c: Vertical(g3)
    c: Coincident(g4,g3)
    c: Horizontal(g4)
    c: Coincident(g5,g4)
    c: Vertical(g5)
    c: Coincident(g6,g5)
    c: Coincident(g6,g1)
    c: Horizontal(g6)
FEATURE [Sketcher::SketchObject] Sketch064
  FullyConstrained = true
  Placement = pos=(0,0,0) rot=(0.57735,0.57735,0.57735;2.0944rad)
  sketch-geometry (4):
    g0: LineSegment StartX=-112 StartY=-91 StartZ=0 EndX=-108.786 EndY=-94.8302 EndZ=0
    g1: LineSegment StartX=-112 StartY=-91 StartZ=0 EndX=-39.9918 EndY=-30.578 EndZ=0
    g2: LineSegment StartX=-39.9918 StartY=-30.578 StartZ=0 EndX=-36.7779 EndY=-34.4082 EndZ=0
    g3: LineSegment StartX=-36.7779 StartY=-34.4082 StartZ=0 EndX=-108.786 EndY=-94.8302 EndZ=0
  constraints (12):
    c: Coincident(g1,g0)
    c: Coincident(g2,g1)
    c: Coincident(g3,g2)
    c: Coincident(g3,g0)
    c: DistanceX(g0) = -112
    c: Angle(g1) = 0.698132
    c: Parallel(g1,g3)
    c: Angle(g0,g1) = 1.5708
    c: Angle(g1,g2) = 1.5708
    c: Distance(g1) = 94
    c: Distance(g0,g0) = 5
    c: DistanceY(g0) = -91
FEATURE [Part::Extrusion] Extrude018  label="mountStrapLeft"
  Base = -> Sketch064
  Dir = (1,0,0)
  DirMode = 2
  FaceMakerClass = Part::FaceMakerBullseye
  LengthFwd = 15
  LengthRev = 0
  Placement = pos=(123.25,0,0) rot=(0,0,1;0rad)
  Solid = true
  Symmetric = false
FEATURE [Part::MultiFuse] Fusion062
  Shapes = -> [Fusion058,Fusion057,Cylinder110]
FEATURE [Part::Cut] Cut028
  Base = -> Fusion056
  Placement = pos=(0,0,-6) rot=(0,0,1;0rad)
  Tool = -> Fusion062
FEATURE [Sketcher::SketchObject] Sketch065
  FullyConstrained = true
  Placement = pos=(0,0,0) rot=(0.57735,0.57735,0.57735;2.0944rad)
FEATURE [Part::Box] Box  label="Cube"
  AttacherType = Attacher::AttachEngine3D
  Height = 13
  Length = 22
  Placement = pos=(-20.5,-34,56) rot=(0,0,1;0rad)
  Width = 18
FEATURE [Part::Box] Box003  label="Cube001"
  AttacherType = Attacher::AttachEngine3D
  Height = 10
  Length = 17
  Placement = pos=(-10,-24,55) rot=(0,0,1;0rad)
  Width = 10
FEATURE [Part::Cylinder] Cylinder111
  Angle = 360
  AttacherType = Attacher::AttachEngine3D
  FirstAngle = 0
  Height = 13
  Placement = pos=(-20.5,-25,56) rot=(0,0,1;0rad)
  Radius = 9
  SecondAngle = 0
FEATURE [Part::Cylinder] Cylinder112  label="antennaIn002"
  Angle = 360
  AttacherType = Attacher::AttachEngine3D
  FirstAngle = 0
  Height = 10
  Placement = pos=(-23,0,65) rot=(0,0,1;0rad)
  Radius = 3.25
  SecondAngle = 0
FEATURE [Part::Cylinder] Cylinder113  label="antennaIn003"
  Angle = 360
  AttacherType = Attacher::AttachEngine3D
  FirstAngle = 0
  Height = 10
  Placement = pos=(-23,0,69) rot=(0,0,1;0rad)
  Radius = 5.75
  SecondAngle = 0
FEATURE [Part::Cylinder] Cylinder017  label="antennaIn004"
  Angle = 360
  AttacherType = Attacher::AttachEngine3D
  FirstAngle = 0
  Height = 10
  Placement = pos=(-23,0,65) rot=(0,0,1;0rad)
  Radius = 3.25
  SecondAngle = 0
FEATURE [Part::Cylinder] Cylinder018  label="antennaIn005"
  Angle = 360
  AttacherType = Attacher::AttachEngine3D
  FirstAngle = 0
  Height = 10
  Placement = pos=(-23,0,69) rot=(0,0,1;0rad)
  Radius = 5.75
  SecondAngle = 0
FEATURE [Part::Cylinder] Cylinder019  label="m3_5Add"
  Angle = 360
  AttacherType = Attacher::AttachEngine3D
  FirstAngle = 0
  Height = 3
  Placement = pos=(-4.5,-22,62.5) rot=(0,0,1;0rad)
  Radius = 3
  SecondAngle = 0
FEATURE [Part::Cylinder] Cylinder114  label="m3Cut"
  Angle = 360
  AttacherType = Attacher::AttachEngine3D
  FirstAngle = 0
  Height = 7
  Placement = pos=(-4.5,-22,62.5) rot=(0,0,1;0rad)
  Radius = 1.8
  SecondAngle = 0
FEATURE [Part::Cylinder] Cylinder115  label="m3Cut001"
  Angle = 360
  AttacherType = Attacher::AttachEngine3D
  FirstAngle = 0
  Height = 7
  Placement = pos=(-4.5,-22,67.5) rot=(0,0,1;0rad)
  Radius = 3
  SecondAngle = 0
FEATURE [Part::MultiFuse] Fusion063
  Placement = pos=(0,0,-1) rot=(0,0,1;0rad)
  Shapes = -> [Cylinder111,Box]
FEATURE [Part::Fillet] Fillet038
  Base = -> Fusion063
  Edges = 1 edges r=6: [Edge8]
FEATURE [Part::Fillet] Fillet001
  Base = -> Fillet038
  Edges = 9 edges r=1: [Edge1,Edge4,Edge5,Edge8,Edge13,Edge14,Edge15,Edge17,Edge18]
FEATURE [Part::MultiFuse] Fusion064
  Placement = pos=(2.5,-25,-6) rot=(0,0,1;0rad)
  Shapes = -> [Cylinder112,Cylinder113]
FEATURE [Part::MultiFuse] Fusion065
  Placement = pos=(2.5,-25,-19.5) rot=(0,0,1;0rad)
  Shapes = -> [Cylinder017,Cylinder018]
FEATURE [Part::MultiFuse] Fusion006  label="antennaCuts"
  Shapes = -> [Fusion064,Fusion065]
FEATURE [Part::Cut] Cut029
  Base = -> Fillet001
  Tool = -> Fusion006
FEATURE [Part::Fillet] Fillet002
  Base = -> Cut029
  Edges = 2 edges r=1: [Edge68,Edge69]
FEATURE [Part::Fillet] Fillet003
  Base = -> Fillet002
  Edges = 3 edges r=1: [Edge75,Edge76,Edge79]
FEATURE [Part::MultiFuse] Fusion009
  Shapes = -> [Cylinder115,Cylinder114]
FEATURE [Sketcher::SketchObject] Sketch066
  FullyConstrained = true
  MapMode = 5
  Support = -> [XY_Plane021]
  sketch-geometry (24):
    g0: GeomPoint X=-15.8769 Y=6.2818 Z=0
    g1: GeomPoint X=-15.8769 Y=-11.8438 Z=0
    g2: GeomPoint X=-15.5941 Y=-16.3746 Z=0
    g3: GeomPoint X=-15.0711 Y=-20.8575 Z=0
    g4: GeomPoint X=-14.3647 Y=-25.3051 Z=0
    g5: GeomPoint X=-13.8626 Y=-26.7835 Z=0
    g6: GeomPoint X=-13.0815 Y=-28.0945 Z=0
    g7: GeomPoint X=-12.161 Y=-29.1266 Z=0
    g8: GeomPoint X=-10.8221 Y=-30.0192 Z=0
    g9: GeomPoint X=-9.31585 Y=-30.5771 Z=0
    g10: GeomPoint X=-7.72589 Y=-30.6886 Z=0
    g11: GeomPoint X=7.47631 Y=-30.6886 Z=0
    g12: LineSegment StartX=-15.5941 StartY=-16.3746 StartZ=0 EndX=-15.0711 EndY=-20.8575 EndZ=0
    g13: LineSegment StartX=-15.0711 StartY=-20.8575 StartZ=0 EndX=-14.3647 EndY=-25.3051 EndZ=0
    g14: LineSegment StartX=-14.3647 StartY=-25.3051 StartZ=0 EndX=-13.8626 EndY=-26.7835 EndZ=0
    g15: LineSegment StartX=-13.8626 StartY=-26.7835 StartZ=0 EndX=-13.0815 EndY=-28.0945 EndZ=0
    g16: LineSegment StartX=-13.0815 StartY=-28.0945 StartZ=0 EndX=-12.161 EndY=-29.1266 EndZ=0
    g17: LineSegment StartX=-12.161 StartY=-29.1266 StartZ=0 EndX=-10.8221 EndY=-30.0192 EndZ=0
    g18: LineSegment StartX=-10.8221 StartY=-30.0192 StartZ=0 EndX=-9.31585 EndY=-30.5771 EndZ=0
    g19: LineSegment StartX=-9.31585 StartY=-30.5771 StartZ=0 EndX=-7.72589 EndY=-30.6886 EndZ=0
    g20: LineSegment StartX=7.47631 StartY=-30.6886 StartZ=0 EndX=-7.72589 EndY=-30.6886 EndZ=0
    g21: LineSegment StartX=-15.8769 StartY=-11.8438 StartZ=0 EndX=-15.5941 EndY=-16.3746 EndZ=0
    g22: LineSegment StartX=-15.8769 StartY=-11.8438 StartZ=0 EndX=-15.8769 EndY=6.2818 EndZ=0
    g23: LineSegment StartX=-15.8769 StartY=6.2818 StartZ=0 EndX=7.47631 EndY=-30.6886 EndZ=0
  constraints (54):
    c: Coincident(g12,g2)
    c: Coincident(g12,g3)
    c: Coincident(g13,g12)
    c: Coincident(g13,g4)
    c: Coincident(g14,g13)
    c: Coincident(g14,g5)
    c: Coincident(g15,g14)
    c: Coincident(g15,g6)
    c: Coincident(g16,g15)
    c: Coincident(g16,g7)
    c: Coincident(g17,g16)
    c: Coincident(g17,g8)
    c: Coincident(g18,g9)
    c: Coincident(g19,g10)
    c: Coincident(g20,g11)
    c: Coincident(g20,g19)
    c: Coincident(g21,g12)
    c: Coincident(g22,g21)
    c: Coincident(g22,g0)
    c: Coincident(g23,g20)
    c: DistanceX(g0,g11) = 23.3532
    c: DistanceY(g0,g11) = -36.9704
    c: DistanceX(g1,g11) = 23.3532
    c: DistanceY(g1,g11) = -18.8449
    c: DistanceX(g2,g11) = 23.0704
    c: DistanceY(g2,g11) = -14.3141
    c: DistanceX(g3,g11) = 22.5474
    c: DistanceY(g3,g11) = -9.83113
    c: DistanceX(g4,g11) = 21.841
    c: DistanceY(g4,g11) = -5.38353
    c: DistanceX(g5,g11) = 21.3389
    c: DistanceY(g5,g11) = -3.90515
    c: DistanceX(g6,g11) = 20.5578
    c: DistanceY(g6,g11) = -2.59414
    c: DistanceX(g7,g11) = 19.6373
    c: DistanceY(g7,g11) = -1.56206
    c: DistanceX(g8,g11) = 18.2984
    c: DistanceY(g8,g11) = -0.669455
    c: DistanceX(g9,g11) = 16.7922
    c: DistanceY(g9,g11) = -0.111576
    c: DistanceX(g10,g11) = 15.2022
    c: DistanceY(g10,g11) = 0
    c: DistanceX(g-1) = 0
    c: DistanceY(g-1) = 0
    c: DistanceX(g22) = -15.8769
    c: DistanceY(g22) = 6.2818
    c: DistanceX(g18,g22) = -5.05474
    c: DistanceY(g18,g22) = 36.301
    c: DistanceX(g19,g22) = -6.56102
    c: DistanceY(g19,g22) = 36.8589
    c: DistanceX(g21,g22) = 0
    c: DistanceY(g21,g22) = 18.1256
    c: DistanceX(g23,g22) = 0
    c: DistanceY(g23,g22) = 0
FEATURE [PartDesign::Pad] Pad
  Direction = (0,0,1)
  Length = 30
  Length2 = 10
  Profile = -> Sketch066
  ReferenceAxis = -> Sketch066 [N_Axis]
  Type = 0
FEATURE [PartDesign::AdditiveBox] Box002
  AttacherType = Attacher::AttachEngine3D
  BaseFeature = -> Pad
  Height = 10
  Length = 10
  Width = 10
FEATURE [PartDesign::Body] Body  label="Body012"
  Group = -> [Sketch066,Pad,Box002]
  Origin = -> Origin021
  Placement = pos=(0,0,35) rot=(0,0,1;0rad)
  Tip = -> Box002
FEATURE [Part::MultiFuse] Fusion007  label="firstCuts"
  Shapes = -> [Box003,Body]
FEATURE [Part::Cut] Cut001
  Base = -> Fillet003
  Tool = -> Fusion007
FEATURE [Part::MultiFuse] Fusion008
  Shapes = -> [Cylinder019,Cut001]
FEATURE [Part::Cut] Cut002
  Base = -> Fusion008
  Placement = pos=(74.8,0,-176.8) rot=(0,0,1;0rad)
  Tool = -> Fusion009
FEATURE [Part::Fillet] Fillet004  label="antennaHolder"
  Base = -> Cut002
  Edges = 1 edges r=0.4: [Edge105]
  Placement = pos=(400,0,-268.2) rot=(0,0,1;0rad)
FEATURE [Part::Box] Box042  label="Cube030"
  AttacherType = Attacher::AttachEngine3D
  Height = 11
  Length = 21
  Placement = pos=(411.732,157.215,-81) rot=(0,0,1;0.785398rad)
  Width = 45
FEATURE [Part::Box] Box043  label="Cube031"
  AttacherType = Attacher::AttachEngine3D
  Height = 10
  Length = 35
  Placement = pos=(-20.5,-34,56) rot=(0,0,1;0rad)
  Width = 18
FEATURE [Part::Cylinder] Cylinder118  label="antennaIn006"
  Angle = 360
  AttacherType = Attacher::AttachEngine3D
  FirstAngle = 0
  Height = 10
  Placement = pos=(-23,0,65) rot=(0,0,1;0rad)
  Radius = 3.25
  SecondAngle = 0
FEATURE [Part::Cylinder] Cylinder119  label="antennaIn007"
  Angle = 360
  AttacherType = Attacher::AttachEngine3D
  FirstAngle = 0
  Height = 10
  Placement = pos=(-23,0,69) rot=(0,0,1;0rad)
  Radius = 5.75
  SecondAngle = 0
FEATURE [Part::Cylinder] Cylinder120
  Angle = 360
  AttacherType = Attacher::AttachEngine3D
  FirstAngle = 0
  Height = 10
  Placement = pos=(-20.5,-25,56) rot=(0,0,1;0rad)
  Radius = 9
  SecondAngle = 0
FEATURE [Part::Cylinder] Cylinder121  label="antennaIn008"
  Angle = 360
  AttacherType = Attacher::AttachEngine3D
  FirstAngle = 0
  Height = 10
  Placement = pos=(-23,0,65) rot=(0,0,1;0rad)
  Radius = 3.25
  SecondAngle = 0
FEATURE [Part::Cylinder] Cylinder122  label="antennaIn009"
  Angle = 360
  AttacherType = Attacher::AttachEngine3D
  FirstAngle = 0
  Height = 10
  Placement = pos=(-23,0,69) rot=(0,0,1;0rad)
  Radius = 5.75
  SecondAngle = 0
FEATURE [Part::MultiFuse] Fusion067
  Placement = pos=(0,0,-1) rot=(0,0,1;0rad)
  Shapes = -> [Cylinder120,Box043]
FEATURE [Part::FeaturePython] Cutout  # WARN: FeaturePython — macro-defined, semantics opaque (R4)
  Base = -> Fusion034
  Tolerance = 0
  Tool = -> Box042
FEATURE [Part::Cylinder] Cylinder123
  Angle = 360
  AttacherType = Attacher::AttachEngine3D
  FirstAngle = 0
  Height = 10
  Placement = pos=(394.389,189.894,-76) rot=(0,0,-1;0.785398rad)
  Radius = 3
  SecondAngle = 0
FEATURE [Part::Cylinder] Cylinder124
  Angle = 360
  AttacherType = Attacher::AttachEngine3D
  FirstAngle = 0
  Height = 10
  Placement = pos=(407.8,176.35,-76) rot=(0,0,1;0rad)
  Radius = 3
  SecondAngle = 0
FEATURE [Part::FeaturePython] Cutout001  # WARN: FeaturePython — macro-defined, semantics opaque (R4)
  Base = -> Cutout
  Tolerance = 0
  Tool = -> Cylinder123
FEATURE [Part::FeaturePython] Cutout002  label="RainSensor"  # WARN: FeaturePython — macro-defined, semantics opaque (R4)
  Base = -> Cutout001
  Placement = pos=(-144.85,14.25,27.5) rot=(0,0,-1;0.785398rad)
  Tolerance = 0
  Tool = -> Cylinder124
FEATURE [Part::MultiFuse] Fusion069
  Placement = pos=(2.5,-25,-19.5) rot=(0,0,1;0rad)
  Shapes = -> [Cylinder118,Cylinder119]
FEATURE [Part::MultiFuse] Fusion068
  Placement = pos=(2.5,-25,-6) rot=(0,0,1;0rad)
  Shapes = -> [Cylinder121,Cylinder122]
FEATURE [Part::MultiFuse] Fusion066  label="antennaCuts001"
  Shapes = -> [Fusion068,Fusion069]
FEATURE [Mesh::Feature] SoLoNodesMay19_2022_lightModule006__1_  label="SoLoNodesMay19_2022-lightModule006 (1)"
FEATURE [Part::Box] Box044  label="Cube032"
  AttacherType = Attacher::AttachEngine3D
  Height = 10
  Length = 22
  Placement = pos=(-20.5,-34,56) rot=(0,0,1;0rad)
  Width = 18
FEATURE [Part::Cylinder] Cylinder128  label="antennaIn010"
  Angle = 360
  AttacherType = Attacher::AttachEngine3D
  FirstAngle = 0
  Height = 10
  Placement = pos=(-23,0,65) rot=(0,0,1;0rad)
  Radius = 3.25
  SecondAngle = 0
FEATURE [Part::Cylinder] Cylinder129  label="antennaIn011"
  Angle = 360
  AttacherType = Attacher::AttachEngine3D
  FirstAngle = 0
  Height = 10
  Placement = pos=(-23,0,69) rot=(0,0,1;0rad)
  Radius = 5.75
  SecondAngle = 0
FEATURE [Part::Cylinder] Cylinder130
  Angle = 360
  AttacherType = Attacher::AttachEngine3D
  FirstAngle = 0
  Height = 10
  Placement = pos=(-20.5,-25,56) rot=(0,0,1;0rad)
  Radius = 9
  SecondAngle = 0
FEATURE [Part::Cylinder] Cylinder131  label="antennaIn012"
  Angle = 360
  AttacherType = Attacher::AttachEngine3D
  FirstAngle = 0
  Height = 10
  Placement = pos=(-23,0,65) rot=(0,0,1;0rad)
  Radius = 3.25
  SecondAngle = 0
FEATURE [Part::Cylinder] Cylinder132  label="antennaIn013"
  Angle = 360
  AttacherType = Attacher::AttachEngine3D
  FirstAngle = 0
  Height = 10
  Placement = pos=(-23,0,69) rot=(0,0,1;0rad)
  Radius = 5.75
  SecondAngle = 0
FEATURE [Part::Cylinder] Cylinder133
  Angle = 360
  AttacherType = Attacher::AttachEngine3D
  FirstAngle = 0
  Height = 12
  Placement = pos=(-210.17,-163.45,-98.81) rot=(0,0,1;0rad)
  Radius = 3
  SecondAngle = 0
FEATURE [Part::Cylinder] Cylinder134
  Angle = 360
  AttacherType = Attacher::AttachEngine3D
  FirstAngle = 0
  Height = 12
  Placement = pos=(-210.17,-144.95,-98.71) rot=(0,0,1;0rad)
  Radius = 3
  SecondAngle = 0
FEATURE [Part::MultiFuse] Fusion071
  Placement = pos=(0,0,-1) rot=(0,0,1;0rad)
  Shapes = -> [Cylinder130,Box044]
FEATURE [Part::Fillet] Fillet043
  Base = -> Fusion071
  Edges = 1 edges r=5: [Edge8]
FEATURE [Part::Fillet] Fillet042
  Base = -> Fillet043
  Edges = 9 edges r=1: [Edge1,Edge4,Edge5,Edge8,Edge13,Edge14,Edge15,Edge17,Edge18]
FEATURE [Part::MultiFuse] Fusion072
  Placement = pos=(2.5,-25,-6) rot=(0,0,1;0rad)
  Shapes = -> [Cylinder131,Cylinder132]
FEATURE [Part::MultiFuse] Fusion073
  Placement = pos=(2.5,-25,-19.5) rot=(0,0,1;0rad)
  Shapes = -> [Cylinder128,Cylinder129]
FEATURE [Part::MultiFuse] Fusion070  label="antennaCuts002"
  Shapes = -> [Fusion072,Fusion073]
FEATURE [Part::Cut] Cut031
  Base = -> Fillet042
  Placement = pos=(-208.2,-93.9,-152) rot=(0,0,1;0rad)
  Tool = -> Fusion070
FEATURE [Part::FeaturePython] Connect001  # WARN: FeaturePython — macro-defined, semantics opaque (R4)
  Objects = -> [Cut031]
  Tolerance = 0
FEATURE [Part::FeaturePython] Cutout005  # WARN: FeaturePython — macro-defined, semantics opaque (R4)
  Base = -> Connect001
  Tolerance = 0
  Tool = -> Cylinder133
FEATURE [Part::FeaturePython] Cutout006  label="RainModules"  # WARN: FeaturePython — macro-defined, semantics opaque (R4)
  Base = -> Cutout005
  Placement = pos=(30,0,0) rot=(0,0,1;0rad)
  Tolerance = 0
  Tool = -> Cylinder134
FEATURE [Sketcher::SketchObject] Sketch067
  FullyConstrained = false
  sketch-geometry (10):
    g0: LineSegment StartX=-150.173 StartY=-71.5827 StartZ=0 EndX=-123.893 EndY=-71.5827 EndZ=0
    g1: LineSegment StartX=-123.893 StartY=-71.5827 StartZ=0 EndX=-123.893 EndY=-111.583 EndZ=0
    g2: LineSegment StartX=-160.253 StartY=-111.583 StartZ=0 EndX=-123.893 EndY=-111.583 EndZ=0
    g3: ArcOfCircle CenterX=-158.669 CenterY=-124.304 CenterZ=0 NormalX=0 NormalY=0 NormalZ=1 AngleXU=0 Radius=12.82 StartAngle=1.69467 EndAngle=3.10486
    g4: LineSegment StartX=-171.48 StartY=-123.834 StartZ=0 EndX=-171.48 EndY=-162.804 EndZ=0
    g5: LineSegment StartX=-171.48 StartY=-162.804 StartZ=0 EndX=-189.66 EndY=-162.804 EndZ=0
    g6: LineSegment StartX=-189.66 StartY=-162.804 StartZ=0 EndX=-189.66 EndY=-110.084 EndZ=0
    g7: ArcOfCircle CenterX=-149.64 CenterY=-111.629 CenterZ=0 NormalX=0 NormalY=0 NormalZ=1 AngleXU=0 Radius=40.05 StartAngle=1.5841 EndAngle=3.103
    g8: Circle CenterX=-180.57 CenterY=-152.177 CenterZ=0 NormalX=0 NormalY=0 NormalZ=1 AngleXU=0 Radius=3.25
    g9: Circle CenterX=-180.57 CenterY=-133.177 CenterZ=0 NormalX=0 NormalY=0 NormalZ=1 AngleXU=0 Radius=3.25
  constraints (28):
    c: Horizontal(g0)
    c: Coincident(g1,g0)
    c: Vertical(g1)
    c: Coincident(g2,g1)
    c: Horizontal(g2)
    c: Coincident(g3,g2)
    c: Coincident(g4,g3)
    c: Vertical(g4)
    c: Coincident(g5,g4)
    c: Horizontal(g5)
    c: Coincident(g6,g5)
    c: Vertical(g6)
    c: Coincident(g7,g6)
    c: Coincident(g7,g0)
    c: Distance(g2) = 36.36
    c: Distance(g1) = 40
    c: Distance(g0) = 26.28
    c: Radius(g7) = 40.05
    c: Distance(g6) = 52.72
    c: Distance(g5) = 18.18
    c: Distance(g4) = 38.97
    c: Radius(g3) = 12.82
    c: DistanceY(g8,g9) = 19
    c: Radius(g8) = 3.25
    c: Radius(g9) = 3.25
    c: DistanceX(g8,g9) = 0
    c: Distance(g4,g-2) = 171.48
    c: Distance(g8,g-2) = 180.57
FEATURE [Part::Extrusion] Extrude020  label="lightModuleHold001"
  Base = -> Sketch067
  Dir = (0,0,1)
  DirMode = 2
  FaceMakerClass = Part::FaceMakerBullseye
  LengthFwd = 10
  LengthRev = 0
  Placement = pos=(0,-21,-96) rot=(0,0,1;0rad)
  Solid = true
  Symmetric = false
FEATURE [Part::Extrusion] Extrude021
  Base = -> Sketch067
  Dir = (0,0,1)
  DirMode = 2
  FaceMakerClass = Part::FaceMakerBullseye
  LengthFwd = 10
  LengthRev = 0
  Placement = pos=(0,-11.21,-98.7) rot=(0,0,1;0rad)
  Solid = true
  Symmetric = false
FEATURE [Part::Box] Box045  label="Cube033"
  AttacherType = Attacher::AttachEngine3D
  Height = 100
  Length = 100
  Placement = pos=(-239,-160.85,-115.65) rot=(0,0,1;0rad)
  Width = 100
FEATURE [Part::Cylinder] Cylinder135  label="base009"
  Angle = 360
  AttacherType = Attacher::AttachEngine3D
  FirstAngle = 0
  Height = 4.5
  Placement = pos=(136,0,65) rot=(0,0,1;0rad)
  Radius = 40
  SecondAngle = 0
FEATURE [Part::Cylinder] Cylinder136  label="baseCut002"
  Angle = 360
  AttacherType = Attacher::AttachEngine3D
  FirstAngle = 0
  Height = 7
  Placement = pos=(5,0,74) rot=(0,0,1;0rad)
  Radius = 24
  SecondAngle = 0
FEATURE [Part::Cylinder] Cylinder137
  Angle = 360
  AttacherType = Attacher::AttachEngine3D
  FirstAngle = 0
  Height = 14.5
  Placement = pos=(134,32.6,55) rot=(0,0,1;0rad)
  Radius = 5.5
  SecondAngle = 0
FEATURE [Part::Cylinder] Cylinder138
  Angle = 360
  AttacherType = Attacher::AttachEngine3D
  FirstAngle = 0
  Height = 5.82
  Placement = pos=(0,-21,0) rot=(0,0,1;0rad)
  Radius = 5
  SecondAngle = 0
FEATURE [Part::Cylinder] Cylinder139
  Angle = 360
  AttacherType = Attacher::AttachEngine3D
  FirstAngle = 0
  Height = 5.82
  Placement = pos=(20.5,-21,0) rot=(0,0,1;0rad)
  Radius = 5
  SecondAngle = 0
  expr: Radius = 5
FEATURE [Part::Cylinder] Cylinder140
  Angle = 360
  AttacherType = Attacher::AttachEngine3D
  FirstAngle = 0
  Height = 5.82
  Placement = pos=(0,-21,0) rot=(0,0,1;0rad)
  Radius = 5
  SecondAngle = 0
FEATURE [Part::Cylinder] Cylinder141
  Angle = 360
  AttacherType = Attacher::AttachEngine3D
  FirstAngle = 0
  Height = 5.82
  Placement = pos=(20.5,-21,0) rot=(0,0,1;0rad)
  Radius = 5
  SecondAngle = 0
FEATURE [Part::Cylinder] Cylinder142  label="m2HeatSetInsets012"
  Angle = 360
  AttacherType = Attacher::AttachEngine3D
  FirstAngle = 0
  Height = 10
  Placement = pos=(-30,0,65) rot=(0,0,1;0rad)
  Radius = 2
  SecondAngle = 0
  expr: Radius = 2
FEATURE [Part::Cylinder] Cylinder143  label="m2HeatSetInsets013"
  Angle = 360
  AttacherType = Attacher::AttachEngine3D
  FirstAngle = 0
  Height = 10
  Placement = pos=(40,0,65) rot=(0,0,1;0rad)
  Radius = 2
  SecondAngle = 0
FEATURE [Part::Cylinder] Cylinder144  label="m2HeatSetInsets014"
  Angle = 360
  AttacherType = Attacher::AttachEngine3D
  FirstAngle = 0
  Height = 10
  Placement = pos=(5,35,65) rot=(0,0,1;0rad)
  Radius = 2
  SecondAngle = 0
FEATURE [Part::Cylinder] Cylinder145  label="m2HeatSetInsets015"
  Angle = 360
  AttacherType = Attacher::AttachEngine3D
  FirstAngle = 0
  Height = 10
  Placement = pos=(5,-35,65) rot=(0,0,1;0rad)
  Radius = 2
  SecondAngle = 0
  expr: Radius = 2
FEATURE [Part::Cylinder] Cylinder146
  Angle = 360
  AttacherType = Attacher::AttachEngine3D
  FirstAngle = 0
  Height = 10
  Placement = pos=(0,-21,0) rot=(0,0,1;0rad)
  Radius = 2
  SecondAngle = 0
FEATURE [Part::Cylinder] Cylinder147
  Angle = 360
  AttacherType = Attacher::AttachEngine3D
  FirstAngle = 0
  Height = 10
  Placement = pos=(20.5,-21,0) rot=(0,0,1;0rad)
  Radius = 2
  SecondAngle = 0
FEATURE [Part::Cylinder] Cylinder148
  Angle = 360
  AttacherType = Attacher::AttachEngine3D
  FirstAngle = 0
  Height = 10
  Placement = pos=(0,-21,0) rot=(0,0,1;0rad)
  Radius = 2
  SecondAngle = 0
FEATURE [Part::Cylinder] Cylinder149
  Angle = 360
  AttacherType = Attacher::AttachEngine3D
  FirstAngle = 0
  Height = 10
  Placement = pos=(20.5,-21,0) rot=(0,0,1;0rad)
  Radius = 2
  SecondAngle = 0
FEATURE [Part::Cylinder] Cylinder150  label="WireCut003"
  Angle = 360
  AttacherType = Attacher::AttachEngine3D
  FirstAngle = 0
  Height = 60
  Placement = pos=(134,32.6,20) rot=(0,0,1;0rad)
  Radius = 2.5
  SecondAngle = 0
FEATURE [Part::Cylinder] Cylinder151  label="m2HeatSetInsets016"
  Angle = 360
  AttacherType = Attacher::AttachEngine3D
  FirstAngle = 0
  Height = 10
  Placement = pos=(-30,0,65) rot=(0,0,1;0rad)
  Radius = 2
  SecondAngle = 0
  expr: Radius = 2
FEATURE [Part::Cylinder] Cylinder152  label="m2HeatSetInsets017"
  Angle = 360
  AttacherType = Attacher::AttachEngine3D
  FirstAngle = 0
  Height = 10
  Placement = pos=(40,0,65) rot=(0,0,1;0rad)
  Radius = 2
  SecondAngle = 0
FEATURE [Part::Cylinder] Cylinder153  label="m2HeatSetInsets018"
  Angle = 360
  AttacherType = Attacher::AttachEngine3D
  FirstAngle = 0
  Height = 10
  Placement = pos=(5,35,65) rot=(0,0,1;0rad)
  Radius = 2
  SecondAngle = 0
FEATURE [Part::Cylinder] Cylinder154  label="m2HeatSetInsets019"
  Angle = 360
  AttacherType = Attacher::AttachEngine3D
  FirstAngle = 0
  Height = 10
  Placement = pos=(5,-35,65) rot=(0,0,1;0rad)
  Radius = 2
  SecondAngle = 0
  expr: Radius = 2
FEATURE [Part::Cylinder] Cylinder155
  Angle = 360
  AttacherType = Attacher::AttachEngine3D
  FirstAngle = 0
  Height = 10
  Placement = pos=(0,-21,0) rot=(0,0,1;0rad)
  Radius = 2
  SecondAngle = 0
FEATURE [Part::Cylinder] Cylinder156
  Angle = 360
  AttacherType = Attacher::AttachEngine3D
  FirstAngle = 0
  Height = 10
  Placement = pos=(20.5,-21,0) rot=(0,0,1;0rad)
  Radius = 2
  SecondAngle = 0
FEATURE [Part::Cylinder] Cylinder157
  Angle = 360
  AttacherType = Attacher::AttachEngine3D
  FirstAngle = 0
  Height = 10
  Placement = pos=(0,-21,0) rot=(0,0,1;0rad)
  Radius = 2
  SecondAngle = 0
FEATURE [Part::Cylinder] Cylinder158
  Angle = 360
  AttacherType = Attacher::AttachEngine3D
  FirstAngle = 0
  Height = 10
  Placement = pos=(20.5,-21,0) rot=(0,0,1;0rad)
  Radius = 2
  SecondAngle = 0
FEATURE [Part::Cylinder] Cylinder159  label="WireCut004"
  Angle = 360
  AttacherType = Attacher::AttachEngine3D
  FirstAngle = 0
  Height = 60
  Placement = pos=(134,32.6,20) rot=(0,0,1;0rad)
  Radius = 2.5
  SecondAngle = 0
FEATURE [Part::Cylinder] Cylinder160  label="lightin001"
  Angle = 360
  AttacherType = Attacher::AttachEngine3D
  FirstAngle = 0
  Height = 21
  Placement = pos=(-129.35,-97.1,-100) rot=(1,0,0;0.698132rad)
  Radius = 5.25
  SecondAngle = 0
FEATURE [Part::Cylinder] Cylinder161
  Angle = 360
  AttacherType = Attacher::AttachEngine3D
  FirstAngle = 0
  Height = 10
  Placement = pos=(-129.35,-40.01,-39.84) rot=(1,0,0;0.698132rad)
  Radius = 2.75
  SecondAngle = 0
FEATURE [Part::Cylinder] Cylinder162
  Angle = 360
  AttacherType = Attacher::AttachEngine3D
  FirstAngle = 0
  Height = 21
  Placement = pos=(-129.35,-97.1,-100) rot=(1,0,0;0.698132rad)
  Radius = 2.25
  SecondAngle = 0
FEATURE [Part::MultiFuse] Fusion077  label="m3HeatSetCuts015"
  Placement = pos=(-5,39,70) rot=(0,0,1;0rad)
  Shapes = -> [Cylinder139,Cylinder138]
FEATURE [Part::MultiFuse] Fusion078  label="m3HeatSetCuts016"
  Placement = pos=(-5,3,70) rot=(0,0,1;0rad)
  Shapes = -> [Cylinder141,Cylinder140]
FEATURE [Part::MultiFuse] Fusion079  label="m3HeatSetCuts017"
  Placement = pos=(128.75,10,-1) rot=(0,0,1;0rad)
  Shapes = -> [Fusion078,Fusion077]
FEATURE [Part::MultiFuse] Fusion082
  Placement = pos=(129,10,0) rot=(0,0,1;0rad)
  Shapes = -> [Cylinder142,Cylinder143,Cylinder144,Cylinder145]
FEATURE [Part::MultiFuse] Fusion084  label="m3HeatSetCuts019"
  Placement = pos=(-5,39,70) rot=(0,0,1;0rad)
  Shapes = -> [Cylinder147,Cylinder146]
FEATURE [Part::MultiFuse] Fusion085  label="m3HeatSetCuts020"
  Placement = pos=(-5,3,70) rot=(0,0,1;0rad)
  Shapes = -> [Cylinder149,Cylinder148]
FEATURE [Part::MultiFuse] Fusion083  label="m3HeatSetCuts018"
  Placement = pos=(128.75,10,-1) rot=(0,0,1;0rad)
  Shapes = -> [Fusion085,Fusion084]
FEATURE [Part::MultiFuse] Fusion086  label="lightModuleCut005"
  Shapes = -> [Fusion083,Fusion082,Cylinder150]
FEATURE [Part::MultiFuse] Fusion087
  Placement = pos=(129,10,0) rot=(0,0,1;0rad)
  Shapes = -> [Cylinder151,Cylinder152,Cylinder153,Cylinder154]
FEATURE [Part::MultiFuse] Fusion089  label="m3HeatSetCuts022"
  Placement = pos=(-5,39,70) rot=(0,0,1;0rad)
  Shapes = -> [Cylinder156,Cylinder155]
FEATURE [Part::MultiFuse] Fusion090  label="m3HeatSetCuts023"
  Placement = pos=(-5,3,70) rot=(0,0,1;0rad)
  Shapes = -> [Cylinder158,Cylinder157]
FEATURE [Part::MultiFuse] Fusion088  label="m3HeatSetCuts021"
  Placement = pos=(128.75,10,-1) rot=(0,0,1;0rad)
  Shapes = -> [Fusion090,Fusion089]
FEATURE [Part::MultiFuse] Fusion091  label="lightModuleCut006"
  Placement = pos=(-314,-122,-162) rot=(0,0,1;0rad)
  Shapes = -> [Fusion088,Fusion087,Cylinder159]
FEATURE [Part::MultiFuse] Fusion093  label="lightCuts001"
  Shapes = -> [Cylinder162,Cylinder161]
FEATURE [Sketcher::SketchObject] Sketch070
  FullyConstrained = true
  Placement = pos=(0,0,0) rot=(0.57735,0.57735,0.57735;2.0944rad)
  sketch-geometry (4):
    g0: LineSegment StartX=-112 StartY=-91 StartZ=0 EndX=-108.786 EndY=-94.8302 EndZ=0
    g1: LineSegment StartX=-112 StartY=-91 StartZ=0 EndX=-39.9918 EndY=-30.578 EndZ=0
    g2: LineSegment StartX=-39.9918 StartY=-30.578 StartZ=0 EndX=-36.7779 EndY=-34.4082 EndZ=0
    g3: LineSegment StartX=-36.7779 StartY=-34.4082 StartZ=0 EndX=-108.786 EndY=-94.8302 EndZ=0
  constraints (12):
    c: Coincident(g1,g0)
    c: Coincident(g2,g1)
    c: Coincident(g3,g2)
    c: Coincident(g3,g0)
    c: DistanceX(g0) = -112
    c: Angle(g1) = 0.698132
    c: Parallel(g1,g3)
    c: Angle(g0,g1) = 1.5708
    c: Angle(g1,g2) = 1.5708
    c: Distance(g1) = 94
    c: Distance(g0,g0) = 5
    c: DistanceY(g0) = -91
FEATURE [Part::Extrusion] Extrude023  label="lightIn001"
  Base = -> Sketch070
  Dir = (1,0,0)
  DirMode = 2
  FaceMakerClass = Part::FaceMakerBullseye
  LengthFwd = 15
  LengthRev = 0
  Placement = pos=(-138.75,0,0) rot=(0,0,1;0rad)
  Solid = true
  Symmetric = false
FEATURE [Sketcher::SketchObject] Sketch071
  FullyConstrained = false
  sketch-geometry (4):
    g0: LineSegment StartX=-180 StartY=-72 StartZ=0 EndX=-123.748 EndY=-72 EndZ=0
    g1: LineSegment StartX=-123.748 StartY=-72 StartZ=0 EndX=-123.748 EndY=-112 EndZ=0
    g2: LineSegment StartX=-123.748 StartY=-112 StartZ=0 EndX=-220 EndY=-112 EndZ=0
    g3: ArcOfCircle CenterX=-180 CenterY=-112 CenterZ=0 NormalX=0 NormalY=0 NormalZ=1 AngleXU=0 Radius=40 StartAngle=1.5708 EndAngle=3.14159
  constraints (12):
    c: Horizontal(g0)
    c: Coincident(g1,g0)
    c: Vertical(g1)
    c: Coincident(g2,g1)
    c: Horizontal(g2)
    c: PointOnObject(g3,g2)
    c: Coincident(g3,g0)
    c: Coincident(g2,g3)
    c: Radius(g3) = 40
    c: Angle(g3) = 1.5708
    c: DistanceX(g3) = -180
    c: DistanceY(g3) = -112
FEATURE [Part::Extrusion] Extrude024  label="lightModuleHold002"
  Base = -> Sketch071
  Dir = (0,0,1)
  DirMode = 2
  FaceMakerClass = Part::FaceMakerBullseye
  LengthFwd = 4.5
  LengthRev = 0
  Placement = pos=(0,0,-97) rot=(0,0,1;0rad)
  Solid = true
  Symmetric = false
FEATURE [Sketcher::SketchObject] Sketch072
  FullyConstrained = true
  sketch-geometry (4):
    g0: LineSegment StartX=-138.75 StartY=-72 StartZ=0 EndX=-138.75 EndY=-80 EndZ=0
    g1: LineSegment StartX=-138.75 StartY=-80 StartZ=0 EndX=-123.75 EndY=-80 EndZ=0
    g2: LineSegment StartX=-123.75 StartY=-80 StartZ=0 EndX=-123.75 EndY=-72 EndZ=0
    g3: LineSegment StartX=-123.75 StartY=-72 StartZ=0 EndX=-138.75 EndY=-72 EndZ=0
  constraints (12):
    c: Vertical(g0)
    c: Coincident(g1,g0)
    c: Horizontal(g1)
    c: Coincident(g2,g1)
    c: Vertical(g2)
    c: Coincident(g3,g0)
    c: Horizontal(g3)
    c: DistanceY(g0) = -80
    c: DistanceY(g0,g0) = 8
    c: DistanceX(g0,g1) = 15
    c: DistanceX(g0) = -138.75
    c: Coincident(g2,g3)
FEATURE [Part::Extrusion] Extrude025  label="lightBaseSupport001"
  Base = -> Sketch072
  Dir = (0,0,1)
  DirMode = 2
  FaceMakerClass = Part::FaceMakerBullseye
  LengthFwd = 33.5
  LengthRev = 0
  Placement = pos=(0,0,-97) rot=(0,0,1;0rad)
  Solid = true
  Symmetric = false
FEATURE [Sketcher::SketchObject] Sketch073
  FullyConstrained = true
  Placement = pos=(0,0,0) rot=(0.57735,0.57735,0.57735;2.0944rad)
  sketch-geometry (4):
    g0: LineSegment StartX=-112 StartY=-91 StartZ=0 EndX=-108.786 EndY=-94.8302 EndZ=0
    g1: LineSegment StartX=-112 StartY=-91 StartZ=0 EndX=-39.9918 EndY=-30.578 EndZ=0
    g2: LineSegment StartX=-39.9918 StartY=-30.578 StartZ=0 EndX=-36.7779 EndY=-34.4082 EndZ=0
    g3: LineSegment StartX=-36.7779 StartY=-34.4082 StartZ=0 EndX=-108.786 EndY=-94.8302 EndZ=0
  constraints (12):
    c: Coincident(g1,g0)
    c: Coincident(g2,g1)
    c: Coincident(g3,g2)
    c: Coincident(g3,g0)
    c: DistanceX(g0) = -112
    c: Angle(g1) = 0.698132
    c: Parallel(g1,g3)
    c: Angle(g0,g1) = 1.5708
    c: Angle(g1,g2) = 1.5708
    c: Distance(g1) = 94
    c: Distance(g0,g0) = 5
    c: DistanceY(g0) = -91
FEATURE [Part::Extrusion] Extrude026  label="lightModuleCut004"
  Base = -> Sketch073
  Dir = (1,0,0)
  DirMode = 2
  FaceMakerClass = Part::FaceMakerBullseye
  LengthFwd = 15
  LengthRev = 0
  Placement = pos=(-138.75,-7.78,0) rot=(0,0,1;0rad)
  Solid = true
  Symmetric = false
FEATURE [Part::MultiFuse] Fusion094
  Shapes = -> [Fusion093,Extrude026]
FEATURE [Part::MultiFuse] Fusion096  label="lightModuleCut007"
  Shapes = -> [Fusion091,Fusion094]
FEATURE [Sketcher::SketchObject] Sketch074
  FullyConstrained = true
  Placement = pos=(0,0,0) rot=(0.57735,0.57735,0.57735;2.0944rad)
  sketch-geometry (4):
    g0: LineSegment StartX=-112 StartY=-92.5 StartZ=0 EndX=-110.5 EndY=-92.5 EndZ=0
    g1: LineSegment StartX=-110.5 StartY=-92.5 StartZ=0 EndX=-110.5 EndY=-91 EndZ=0
    g2: LineSegment StartX=-110.5 StartY=-91 StartZ=0 EndX=-112 EndY=-91 EndZ=0
    g3: LineSegment StartX=-112 StartY=-91 StartZ=0 EndX=-112 EndY=-92.5 EndZ=0
  constraints (12):
    c: Coincident(g0,g1)
    c: Coincident(g1,g2)
    c: Coincident(g2,g3)
    c: Coincident(g3,g0)
    c: Horizontal(g0)
    c: Horizontal(g2)
    c: Vertical(g1)
    c: Vertical(g3)
    c: DistanceX(g0) = -112
    c: DistanceY(g0) = -92.5
    c: Distance(g3) = 1.5
    c: DistanceX(g0,g0) = 1.5
FEATURE [Part::Extrusion] Extrude027
  Base = -> Sketch074
  Dir = (1,0,0)
  DirMode = 2
  FaceMakerClass = Part::FaceMakerBullseye
  LengthFwd = 15
  LengthRev = 0
  Placement = pos=(-138.75,0,0) rot=(0,0,1;0rad)
  Solid = true
  Symmetric = false
FEATURE [Part::Sphere] Sphere004  label="SphereBase002"
  Angle1 = 0
  Angle2 = 12
  Angle3 = 360
  AttacherType = Attacher::AttachEngine3D
  Placement = pos=(5,0,74) rot=(0,0,1;0rad)
  Radius = 28.3
FEATURE [Part::Cut] Cut032
  Base = -> Sphere004
  Placement = pos=(131,0,-5) rot=(0,0,1;0rad)
  Tool = -> Cylinder136
FEATURE [Part::MultiFuse] Fusion080  label="Base002"
  Placement = pos=(-2,10,0) rot=(0,0,1;0rad)
  Shapes = -> [Cut032,Cylinder135]
FEATURE [Part::MultiFuse] Fusion081  label="lightModule009"
  Shapes = -> [Fusion080,Cylinder137,Fusion079]
FEATURE [Part::Cut] Cut033  label="lightModule007"
  Base = -> Fusion081
  Placement = pos=(-314,-122,-162) rot=(0,0,1;0rad)
  Tool = -> Fusion086
FEATURE [Part::MultiFuse] Fusion092  label="lightModuleHolder001"
  Shapes = -> [Cut033,Extrude024]
FEATURE [Part::MultiFuse] Fusion095  label="lightModule010"
  Shapes = -> [Extrude023,Fusion092,Extrude025,Cylinder160]
FEATURE [Part::Cut] Cut034
  Base = -> Fusion095
  Tool = -> Fusion096
FEATURE [Part::MultiFuse] Fusion097  label="lightModule011"
  Shapes = -> [Cut034,Extrude027]
FEATURE [Part::Fillet] Fillet041
  Base = -> Fusion097
  Edges = 1 edges r=3: [Edge100]
FEATURE [Part::Fillet] Fillet044  label="lightModule008"
  Base = -> Fillet041
  Edges = 3 edges r=5: [Edge34,Edge94,Edge165]
FEATURE [Part::FeaturePython] Cutout007  # WARN: FeaturePython — macro-defined, semantics opaque (R4)
  Base = -> Fillet044
  Placement = pos=(-0.15,-10.79,2.3) rot=(0,0,1;0rad)
  Tolerance = 0
  Tool = -> Box045
FEATURE [Part::Cylinder] Cylinder163
  Angle = 360
  AttacherType = Attacher::AttachEngine3D
  FirstAngle = 0
  Height = 22.17
  Placement = pos=(-129.47,-104.217,-102.07) rot=(1,0,0;0.698132rad)
  Radius = 5.25
  SecondAngle = 0
FEATURE [Part::Cylinder] Cylinder164
  Angle = 360
  AttacherType = Attacher::AttachEngine3D
  FirstAngle = 0
  Height = 25
  Placement = pos=(-129.47,-103.188,-103.296) rot=(1,0,0;0.698132rad)
  Radius = 2.25
  SecondAngle = 0
FEATURE [Part::Fillet] Fillet040
  Base = -> Fusion067
  Edges = 1 edges r=5: [Edge8]
FEATURE [Part::Fillet] Fillet039
  Base = -> Fillet040
  Edges = 9 edges r=1: [Edge1,Edge4,Edge5,Edge8,Edge13,Edge14,Edge15,Edge17,Edge18]
FEATURE [Part::Cut] Cut030  label="Antenna_holder"
  Base = -> Fillet039
  Placement = pos=(-194,-101,-153.71) rot=(0.010017,-0.190324,-0.98167;0.012217rad)
  Tool = -> Fusion066
FEATURE [Part::FeaturePython] Connect  # WARN: FeaturePython — macro-defined, semantics opaque (R4)
  Objects = -> [Extrude021,Cut030]
  Tolerance = 0
FEATURE [Part::FeaturePython] Connect002  # WARN: FeaturePython — macro-defined, semantics opaque (R4)
  Objects = -> [Connect,Cutout007,Cylinder163]
  Tolerance = 0
FEATURE [Part::FeaturePython] Cutout008  # WARN: FeaturePython — macro-defined, semantics opaque (R4)
  Base = -> Connect002
  Tolerance = 0
  Tool = -> Cylinder164
FEATURE [Part::Mirroring] Part__Mirroring  label="RainModuleHolder"
  Base = (0,0,0)
  Normal = (1,0,0)
  Placement = pos=(-0.6,14,-6.1) rot=(0,0,1;0rad)
  Source = -> Cutout008
FEATURE [Part::Fillet] Fillet045  label="Rain_Module_Holder"
  Base = -> Part__Mirroring
  Edges = 8 edges r=1: [Edge14,Edge18,Edge20,Edge65,Edge69,Edge70,Edge75,Edge76]
